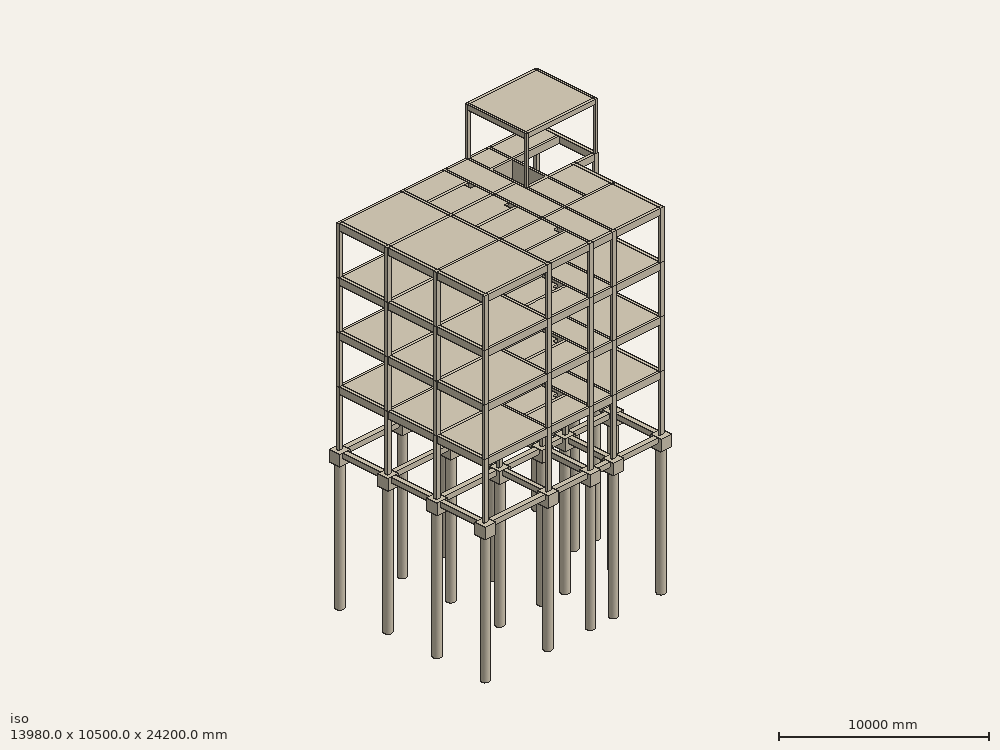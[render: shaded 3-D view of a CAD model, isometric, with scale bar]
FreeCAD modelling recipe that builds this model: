
FCSTD DOCUMENT  (FreeCAD 0.19R24276 (Git))
Label: 2021-02-05 Piloto estructural Metodo 1
License: All rights reserved
objects: Part::FeaturePython×395, Part::Part2DObjectPython×35, App::GeometryPython×28, TechDraw::DrawViewDimension×16, App::DocumentObjectGroup×3, TechDraw::DrawSVGTemplate×3, TechDraw::DrawViewPart×3, TechDraw::DrawPage×3, TechDraw::DrawViewSection×2, Spreadsheet::Sheet×1, App::MaterialObjectPython×1, App::DocumentObjectGroupPython×1, TechDraw::DrawViewAnnotation×1
note: 458 computed .brp shape members not serialized (recipe doc carries the construction recipe); baked Part::Feature solids carry a one-line shape summary decoded from their .brp

FEATURE [Part::FeaturePython] Axis  label="Vertical"  # WARN: FeaturePython — macro-defined, semantics opaque (R4)
  Angles = [0,0,0,0,0,0,0]
  Distances = [1930,4230,2850,1550,1450,1770,1430]
  Length = 11000
  Placement = pos=(0,-500,0) rot=(0,0,1;0rad)
FEATURE [Part::FeaturePython] Axis002  label="Horizontal larga"  # WARN: FeaturePython — macro-defined, semantics opaque (R4)
  Angles = [0,0,0,0,0,0]
  Distances = [100,3250,2620,670,1730,1530]
  Length = 32000
  Placement = pos=(31000,1.077e-12,0) rot=(0,0,1;1.5708rad)
FEATURE [Part::Part2DObjectPython] Rectangle001  label="Lote"  # Draft 2D object (typed FeaturePython)
  Area = 0
  ChamferSize = 0
  Columns = 1
  FilletRadius = 0
  Height = 10000
  Length = 30000
  MakeFace = false
  Rows = 1
FEATURE [Part::Part2DObjectPython] Rectangle002  # Draft 2D object (typed FeaturePython)
  Area = 0
  ChamferSize = 0
  Columns = 1
  FilletRadius = 0
  Height = 700
  Length = 700
  MakeFace = false
  Placement = pos=(14860,9550,0) rot=(0,0,1;0rad)
  Rows = 1
  expr: Height = <<Estructura>>.CabAncho
  expr: Length = <<Estructura>>.CabAncho
FEATURE [Part::Part2DObjectPython] Circle  # Draft 2D object (typed FeaturePython)
  Area = 0
  FirstAngle = 0
  LastAngle = 0
  MakeFace = false
  Placement = pos=(15210,9900,0) rot=(0,0,1;0rad)
  Radius = 250
  expr: Radius = <<Estructura>>.PilRad
FEATURE [Part::FeaturePython] Beam001  # Arch/BIM 7 (typed FeaturePython)
  Chamfer = 0
  DentHeight = 0
  DentLength = 0
  Height = 300
  HorizontalArea = 1059000
  IfcData = attributes={"GlobalId": {"name": "GlobalId", "type": "IfcGloballyUniqueId", "is_enum": false, "enum_values": []}, "Description": {"... (+475 chars omitted),+1 more (map truncated)
  IfcType = 7
  Length = 3530
  MoveBase = false
  MoveWithHost = false
  PerimeterLength = 7660
  Placement = pos=(2280,6490,-800) rot=(0,0,1;0rad)
  PredefinedType = 0
  VerticalArea = 2298000
  Width = 300
FEATURE [Part::FeaturePython] Structure041  label="Beam002"  # Arch/BIM 7 (typed FeaturePython)
  FaceMaker = 0
  Height = 300
  HorizontalArea = 768000
  IfcData = attributes={"GlobalId": {"name": "GlobalId", "type": "IfcGloballyUniqueId", "is_enum": false, "enum_values": []}, "Description": {"... (+475 chars omitted),+1 more (map truncated)
  IfcType = 7
  Length = 2560
  MoveBase = false
  MoveWithHost = false
  Nodes = (2) [(1.2326e-31,-1.51582e-15,5.55112e-16),(2560,-1.51582e-15,5.55112e-16)]
  NodesOffset = 0
  Normal = (0,0,0)
  PerimeterLength = 5720
  Placement = pos=(1930,9550,-650) rot=(0,0,-1;1.5708rad)
  PredefinedType = 0
  VerticalArea = 1.716e+06
  Width = 300
  expr: Height = <<Estructura>>.VRAlto
  expr: Width = <<Estructura>>.VRAncho
FEATURE [Part::FeaturePython] Structure042  label="Beam003"  # Arch/BIM 7 (typed FeaturePython)
  FaceMaker = 0
  Height = 300
  HorizontalArea = 777000
  IfcData = attributes={"GlobalId": {"name": "GlobalId", "type": "IfcGloballyUniqueId", "is_enum": false, "enum_values": []}, "Description": {"... (+475 chars omitted),+1 more (map truncated)
  IfcType = 7
  Length = 2590
  MoveBase = false
  MoveWithHost = false
  Nodes = (2) [(1.2326e-31,-1.51582e-15,5.55112e-16),(2590,-1.51582e-15,5.55112e-16)]
  NodesOffset = 0
  Normal = (0,0,0)
  PerimeterLength = 5780
  Placement = pos=(1930,6290,-650) rot=(0,0,-1;1.5708rad)
  PredefinedType = 0
  VerticalArea = 1.734e+06
  Width = 300
FEATURE [Part::FeaturePython] Structure043  label="Beam004"  # Arch/BIM 7 (typed FeaturePython)
  FaceMaker = 0
  Height = 300
  HorizontalArea = 765000
  IfcData = attributes={"GlobalId": {"name": "GlobalId", "type": "IfcGloballyUniqueId", "is_enum": false, "enum_values": []}, "Description": {"... (+475 chars omitted),+1 more (map truncated)
  IfcType = 7
  Length = 2550
  MoveBase = false
  MoveWithHost = false
  Nodes = (2) [(1.2326e-31,-1.51582e-15,5.55112e-16),(2550,-1.51582e-15,5.55112e-16)]
  NodesOffset = 0
  Normal = (0,0,0)
  PerimeterLength = 5700
  Placement = pos=(1930,3000,-650) rot=(0,0,-1;1.5708rad)
  PredefinedType = 0
  VerticalArea = 1.71e+06
  Width = 300
FEATURE [Part::FeaturePython] Structure044  label="Beam005"  # Arch/BIM 7 (typed FeaturePython)
  FaceMaker = 0
  Height = 300
  HorizontalArea = 768000
  IfcData = attributes={"GlobalId": {"name": "GlobalId", "type": "IfcGloballyUniqueId", "is_enum": false, "enum_values": []}, "Description": {"... (+475 chars omitted),+1 more (map truncated)
  IfcType = 7
  Length = 2560
  MoveBase = false
  MoveWithHost = false
  Nodes = (2) [(1.2326e-31,-1.51582e-15,5.55112e-16),(2560,-1.51582e-15,5.55112e-16)]
  NodesOffset = 0
  Normal = (0,0,0)
  PerimeterLength = 5720
  Placement = pos=(6160.36,9550,-650) rot=(0,0,-1;1.5708rad)
  PredefinedType = 0
  VerticalArea = 1.716e+06
  Width = 300
FEATURE [Part::FeaturePython] Structure045  label="Beam006"  # Arch/BIM 7 (typed FeaturePython)
  FaceMaker = 0
  Height = 300
  HorizontalArea = 777000
  IfcData = attributes={"GlobalId": {"name": "GlobalId", "type": "IfcGloballyUniqueId", "is_enum": false, "enum_values": []}, "Description": {"... (+475 chars omitted),+1 more (map truncated)
  IfcType = 7
  Length = 2590
  MoveBase = false
  MoveWithHost = false
  Nodes = (2) [(1.2326e-31,-1.51582e-15,5.55112e-16),(2590,-1.51582e-15,5.55112e-16)]
  NodesOffset = 0
  Normal = (0,0,0)
  PerimeterLength = 5780
  Placement = pos=(6160.36,6290,-650) rot=(0,0,-1;1.5708rad)
  PredefinedType = 0
  VerticalArea = 1.734e+06
  Width = 300
FEATURE [Part::FeaturePython] Structure046  label="Beam007"  # Arch/BIM 7 (typed FeaturePython)
  FaceMaker = 0
  Height = 300
  HorizontalArea = 765000
  IfcData = attributes={"GlobalId": {"name": "GlobalId", "type": "IfcGloballyUniqueId", "is_enum": false, "enum_values": []}, "Description": {"... (+475 chars omitted),+1 more (map truncated)
  IfcType = 7
  Length = 2550
  MoveBase = false
  MoveWithHost = false
  Nodes = (2) [(1.2326e-31,-1.51582e-15,5.55112e-16),(2550,-1.51582e-15,5.55112e-16)]
  NodesOffset = 0
  Normal = (0,0,0)
  PerimeterLength = 5700
  Placement = pos=(6160.36,3000,-650) rot=(0,0,-1;1.5708rad)
  PredefinedType = 0
  VerticalArea = 1.71e+06
  Width = 300
FEATURE [Part::FeaturePython] Structure048  label="Beam009"  # Arch/BIM 7 (typed FeaturePython)
  FaceMaker = 0
  Height = 300
  HorizontalArea = 777000
  IfcData = attributes={"GlobalId": {"name": "GlobalId", "type": "IfcGloballyUniqueId", "is_enum": false, "enum_values": []}, "Description": {"... (+475 chars omitted),+1 more (map truncated)
  IfcType = 7
  Length = 2590
  MoveBase = false
  MoveWithHost = false
  Nodes = (2) [(1.2326e-31,-1.51582e-15,5.55112e-16),(2590,-1.51582e-15,5.55112e-16)]
  NodesOffset = 0
  Normal = (0,0,0)
  PerimeterLength = 5780
  Placement = pos=(9010.18,6290,-650) rot=(0,0,-1;1.5708rad)
  PredefinedType = 0
  VerticalArea = 1.734e+06
  Width = 300
FEATURE [Part::FeaturePython] Structure049  label="Beam010"  # Arch/BIM 7 (typed FeaturePython)
  FaceMaker = 0
  Height = 300
  HorizontalArea = 765000
  IfcData = attributes={"GlobalId": {"name": "GlobalId", "type": "IfcGloballyUniqueId", "is_enum": false, "enum_values": []}, "Description": {"... (+475 chars omitted),+1 more (map truncated)
  IfcType = 7
  Length = 2550
  MoveBase = false
  MoveWithHost = false
  Nodes = (2) [(1.2326e-31,-1.51582e-15,5.55112e-16),(2550,-1.51582e-15,5.55112e-16)]
  NodesOffset = 0
  Normal = (0,0,0)
  PerimeterLength = 5700
  Placement = pos=(9010.18,3000,-650) rot=(0,0,-1;1.5708rad)
  PredefinedType = 0
  VerticalArea = 1.71e+06
  Width = 300
FEATURE [Part::FeaturePython] Structure053  label="Beam014"  # Arch/BIM 7 (typed FeaturePython)
  FaceMaker = 0
  Height = 300
  HorizontalArea = 765000
  IfcData = attributes={"GlobalId": {"name": "GlobalId", "type": "IfcGloballyUniqueId", "is_enum": false, "enum_values": []}, "Description": {"... (+475 chars omitted),+1 more (map truncated)
  IfcType = 7
  Length = 2550
  MoveBase = false
  MoveWithHost = false
  Nodes = (2) [(1.2326e-31,-1.51582e-15,5.55112e-16),(2550,-1.51582e-15,5.55112e-16)]
  NodesOffset = 0
  Normal = (0,0,0)
  PerimeterLength = 5700
  Placement = pos=(13778.3,3000,-650) rot=(0,0,-1;1.5708rad)
  PredefinedType = 0
  VerticalArea = 1.71e+06
  Width = 300
FEATURE [Part::FeaturePython] Structure056  label="Beam017"  # Arch/BIM 7 (typed FeaturePython)
  FaceMaker = 0
  Height = 300
  HorizontalArea = 765000
  IfcData = attributes={"GlobalId": {"name": "GlobalId", "type": "IfcGloballyUniqueId", "is_enum": false, "enum_values": []}, "Description": {"... (+475 chars omitted),+1 more (map truncated)
  IfcType = 7
  Length = 2550
  MoveBase = false
  MoveWithHost = false
  Nodes = (2) [(1.2326e-31,-1.51582e-15,5.55112e-16),(2550,-1.51582e-15,5.55112e-16)]
  NodesOffset = 0
  Normal = (0,0,0)
  PerimeterLength = 5700
  Placement = pos=(10560,3000,-650) rot=(0,0,-1;1.5708rad)
  PredefinedType = 0
  VerticalArea = 1.71e+06
  Width = 300
FEATURE [Part::FeaturePython] Structure059  label="Beam020"  # Arch/BIM 7 (typed FeaturePython)
  FaceMaker = 0
  Height = 300
  HorizontalArea = 645000
  IfcData = attributes={"GlobalId": {"name": "GlobalId", "type": "IfcGloballyUniqueId", "is_enum": false, "enum_values": []}, "Description": {"... (+475 chars omitted),+1 more (map truncated)
  IfcType = 7
  Length = 2150
  MoveBase = false
  MoveWithHost = false
  Nodes = (2) [(1.2326e-31,-1.51582e-15,5.55112e-16),(2150,-1.51582e-15,5.55112e-16)]
  NodesOffset = 0
  Normal = (0,0,0)
  PerimeterLength = 4900
  Placement = pos=(6510,9900,-650) rot=(0,0,1;0rad)
  PredefinedType = 0
  VerticalArea = 1.47e+06
  Width = 300
FEATURE [Part::FeaturePython] Structure060  label="Beam021"  # Arch/BIM 7 (typed FeaturePython)
  FaceMaker = 0
  Height = 300
  HorizontalArea = 690000
  IfcData = attributes={"GlobalId": {"name": "GlobalId", "type": "IfcGloballyUniqueId", "is_enum": false, "enum_values": []}, "Description": {"... (+475 chars omitted),+1 more (map truncated)
  IfcType = 7
  Length = 2300
  MoveBase = false
  MoveWithHost = false
  Nodes = (2) [(1.2326e-31,-1.51582e-15,5.55112e-16),(2300,-1.51582e-15,5.55112e-16)]
  NodesOffset = 0
  Normal = (0,0,0)
  PerimeterLength = 5200
  Placement = pos=(9360,9900,-650) rot=(0,0,1;0rad)
  PredefinedType = 0
  VerticalArea = 1.56e+06
  Width = 300
FEATURE [Part::FeaturePython] Structure061  label="Beam022"  # Arch/BIM 7 (typed FeaturePython)
  FaceMaker = 0
  Height = 300
  HorizontalArea = 750000
  IfcData = attributes={"GlobalId": {"name": "GlobalId", "type": "IfcGloballyUniqueId", "is_enum": false, "enum_values": []}, "Description": {"... (+475 chars omitted),+1 more (map truncated)
  IfcType = 7
  Length = 2500
  MoveBase = false
  MoveWithHost = false
  Nodes = (2) [(1.2326e-31,-1.51582e-15,5.55112e-16),(2500,-1.51582e-15,5.55112e-16)]
  NodesOffset = 0
  Normal = (0,0,0)
  PerimeterLength = 5600
  Placement = pos=(12360,9900,-650) rot=(0,0,1;0rad)
  PredefinedType = 0
  VerticalArea = 1680000
  Width = 300
FEATURE [Part::FeaturePython] Structure064  label="Beam025"  # Arch/BIM 7 (typed FeaturePython)
  FaceMaker = 0
  Height = 300
  HorizontalArea = 645000
  IfcData = attributes={"GlobalId": {"name": "GlobalId", "type": "IfcGloballyUniqueId", "is_enum": false, "enum_values": []}, "Description": {"... (+475 chars omitted),+1 more (map truncated)
  IfcType = 7
  Length = 2150
  MoveBase = false
  MoveWithHost = false
  Nodes = (2) [(1.2326e-31,-1.51582e-15,5.55112e-16),(2150,-1.51582e-15,5.55112e-16)]
  NodesOffset = 0
  Normal = (0,0,0)
  PerimeterLength = 4900
  Placement = pos=(6510,6640,-650) rot=(0,0,1;0rad)
  PredefinedType = 0
  VerticalArea = 1.47e+06
  Width = 300
FEATURE [Part::FeaturePython] Structure065  label="Beam026"  # Arch/BIM 7 (typed FeaturePython)
  FaceMaker = 0
  Height = 300
  HorizontalArea = 768000
  IfcData = attributes={"GlobalId": {"name": "GlobalId", "type": "IfcGloballyUniqueId", "is_enum": false, "enum_values": []}, "Description": {"... (+475 chars omitted),+1 more (map truncated)
  IfcType = 7
  Length = 2560
  MoveBase = false
  MoveWithHost = false
  Nodes = (2) [(1.2326e-31,-1.51582e-15,5.55112e-16),(2560,-1.51582e-15,5.55112e-16)]
  NodesOffset = 0
  Normal = (0,0,0)
  PerimeterLength = 5720
  Placement = pos=(9010,6990,-650) rot=(0,0,1;1.5708rad)
  PredefinedType = 0
  VerticalArea = 1.716e+06
  Width = 300
FEATURE [Part::FeaturePython] Structure066  label="Beam027"  # Arch/BIM 7 (typed FeaturePython)
  FaceMaker = 0
  Height = 300
  HorizontalArea = 1.059e+06
  IfcData = attributes={"GlobalId": {"name": "GlobalId", "type": "IfcGloballyUniqueId", "is_enum": false, "enum_values": []}, "Description": {"... (+475 chars omitted),+1 more (map truncated)
  IfcType = 7
  Length = 3530
  MoveBase = false
  MoveWithHost = false
  Nodes = (2) [(1.2326e-31,-1.51582e-15,5.55112e-16),(3530,-1.51582e-15,5.55112e-16)]
  NodesOffset = 0
  Normal = (0,0,0)
  PerimeterLength = 7660
  Placement = pos=(2280,3350,-650) rot=(0,0,1;0rad)
  PredefinedType = 0
  VerticalArea = 2.298e+06
  Width = 300
FEATURE [Part::FeaturePython] Structure067  label="Beam028"  # Arch/BIM 7 (typed FeaturePython)
  FaceMaker = 0
  Height = 300
  HorizontalArea = 645000
  IfcData = attributes={"GlobalId": {"name": "GlobalId", "type": "IfcGloballyUniqueId", "is_enum": false, "enum_values": []}, "Description": {"... (+475 chars omitted),+1 more (map truncated)
  IfcType = 7
  Length = 2150
  MoveBase = false
  MoveWithHost = false
  Nodes = (2) [(1.2326e-31,-1.51582e-15,5.55112e-16),(2150,-1.51582e-15,5.55112e-16)]
  NodesOffset = 0
  Normal = (0,0,0)
  PerimeterLength = 4900
  Placement = pos=(6510,3350,-650) rot=(0,0,1;0rad)
  PredefinedType = 0
  VerticalArea = 1.47e+06
  Width = 300
FEATURE [Part::FeaturePython] Structure068  label="Beam029"  # Arch/BIM 7 (typed FeaturePython)
  FaceMaker = 0
  Height = 300
  HorizontalArea = 1.059e+06
  IfcData = attributes={"GlobalId": {"name": "GlobalId", "type": "IfcGloballyUniqueId", "is_enum": false, "enum_values": []}, "Description": {"... (+475 chars omitted),+1 more (map truncated)
  IfcType = 7
  Length = 3530
  MoveBase = false
  MoveWithHost = false
  Nodes = (2) [(1.2326e-31,-1.51582e-15,5.55112e-16),(3530,-1.51582e-15,5.55112e-16)]
  NodesOffset = 0
  Normal = (0,0,0)
  PerimeterLength = 7660
  Placement = pos=(2280,100,-650) rot=(0,0,1;0rad)
  PredefinedType = 0
  VerticalArea = 2.298e+06
  Width = 300
FEATURE [Part::FeaturePython] Structure069  label="Beam030"  # Arch/BIM 7 (typed FeaturePython)
  FaceMaker = 0
  Height = 300
  HorizontalArea = 645000
  IfcData = attributes={"GlobalId": {"name": "GlobalId", "type": "IfcGloballyUniqueId", "is_enum": false, "enum_values": []}, "Description": {"... (+475 chars omitted),+1 more (map truncated)
  IfcType = 7
  Length = 2150
  MoveBase = false
  MoveWithHost = false
  Nodes = (2) [(1.2326e-31,-1.51582e-15,5.55112e-16),(2150,-1.51582e-15,5.55112e-16)]
  NodesOffset = 0
  Normal = (0,0,0)
  PerimeterLength = 4900
  Placement = pos=(6510,100,-650) rot=(0,0,1;0rad)
  PredefinedType = 0
  VerticalArea = 1.47e+06
  Width = 300
FEATURE [Part::FeaturePython] Structure070  label="Beam031"  # Arch/BIM 7 (typed FeaturePython)
  FaceMaker = 0
  Height = 300
  HorizontalArea = 255000
  IfcData = attributes={"GlobalId": {"name": "GlobalId", "type": "IfcGloballyUniqueId", "is_enum": false, "enum_values": []}, "Description": {"... (+475 chars omitted),+1 more (map truncated)
  IfcType = 7
  Length = 850
  MoveBase = false
  MoveWithHost = false
  Nodes = (2) [(1.2326e-31,-1.51582e-15,5.55112e-16),(850,-1.51582e-15,5.55112e-16)]
  NodesOffset = 0
  Normal = (0,0,0)
  PerimeterLength = 2300
  Placement = pos=(9360,100,-650) rot=(0,0,1;0rad)
  PredefinedType = 0
  VerticalArea = 690000
  Width = 300
FEATURE [Part::FeaturePython] Structure071  label="Beam032"  # Arch/BIM 7 (typed FeaturePython)
  FaceMaker = 0
  Height = 300
  HorizontalArea = 756000
  IfcData = attributes={"GlobalId": {"name": "GlobalId", "type": "IfcGloballyUniqueId", "is_enum": false, "enum_values": []}, "Description": {"... (+475 chars omitted),+1 more (map truncated)
  IfcType = 7
  Length = 2520
  MoveBase = false
  MoveWithHost = false
  Nodes = (2) [(1.2326e-31,-1.51582e-15,5.55112e-16),(2520,-1.51582e-15,5.55112e-16)]
  NodesOffset = 0
  Normal = (0,0,0)
  PerimeterLength = 5640
  Placement = pos=(10910,100,-650) rot=(0,0,1;0rad)
  PredefinedType = 0
  VerticalArea = 1.692e+06
  Width = 300
FEATURE [Part::FeaturePython] Structure072  label="Beam033"  # Arch/BIM 7 (typed FeaturePython)
  FaceMaker = 0
  Height = 300
  HorizontalArea = 255000
  IfcData = attributes={"GlobalId": {"name": "GlobalId", "type": "IfcGloballyUniqueId", "is_enum": false, "enum_values": []}, "Description": {"... (+475 chars omitted),+1 more (map truncated)
  IfcType = 7
  Length = 850
  MoveBase = false
  MoveWithHost = false
  Nodes = (2) [(1.2326e-31,-1.51582e-15,5.55112e-16),(850,-1.51582e-15,5.55112e-16)]
  NodesOffset = 0
  Normal = (0,0,0)
  PerimeterLength = 2300
  Placement = pos=(9360,3350,-650) rot=(0,0,1;0rad)
  PredefinedType = 0
  VerticalArea = 690000
  Width = 300
FEATURE [Part::FeaturePython] Structure073  label="Beam034"  # Arch/BIM 7 (typed FeaturePython)
  FaceMaker = 0
  Height = 300
  HorizontalArea = 756000
  IfcData = attributes={"GlobalId": {"name": "GlobalId", "type": "IfcGloballyUniqueId", "is_enum": false, "enum_values": []}, "Description": {"... (+475 chars omitted),+1 more (map truncated)
  IfcType = 7
  Length = 2520
  MoveBase = false
  MoveWithHost = false
  Nodes = (2) [(1.2326e-31,-1.51582e-15,5.55112e-16),(2520,-1.51582e-15,5.55112e-16)]
  NodesOffset = 0
  Normal = (0,0,0)
  PerimeterLength = 5640
  Placement = pos=(10910,3350,-650) rot=(0,0,1;0rad)
  PredefinedType = 0
  VerticalArea = 1.692e+06
  Width = 300
FEATURE [Part::FeaturePython] Structure074  label="Beam035"  # Arch/BIM 7 (typed FeaturePython)
  FaceMaker = 0
  Height = 300
  HorizontalArea = 969000
  IfcData = attributes={"GlobalId": {"name": "GlobalId", "type": "IfcGloballyUniqueId", "is_enum": false, "enum_values": []}, "Description": {"... (+475 chars omitted),+1 more (map truncated)
  IfcType = 7
  Length = 3230
  MoveBase = false
  MoveWithHost = false
  Nodes = (2) [(1.2326e-31,-1.51582e-15,5.55112e-16),(3230,-1.51582e-15,5.55112e-16)]
  NodesOffset = 0
  Normal = (0,0,0)
  PerimeterLength = 7060
  Placement = pos=(15210,9550,-650) rot=(0,0,-1;1.5708rad)
  PredefinedType = 0
  VerticalArea = 2.118e+06
  Width = 300
FEATURE [Part::FeaturePython] Structure075  label="Beam036"  # Arch/BIM 7 (typed FeaturePython)
  FaceMaker = 0
  Height = 300
  HorizontalArea = 576000
  IfcData = attributes={"GlobalId": {"name": "GlobalId", "type": "IfcGloballyUniqueId", "is_enum": false, "enum_values": []}, "Description": {"... (+475 chars omitted),+1 more (map truncated)
  IfcType = 7
  Length = 1920
  MoveBase = false
  MoveWithHost = false
  Nodes = (2) [(1.2326e-31,-1.51582e-15,5.55112e-16),(1920,-1.51582e-15,5.55112e-16)]
  NodesOffset = 0
  Normal = (0,0,0)
  PerimeterLength = 4440
  Placement = pos=(13780,3700,-650) rot=(0,0,1;1.5708rad)
  PredefinedType = 0
  VerticalArea = 1.332e+06
  Width = 300
FEATURE [Part::FeaturePython] Structure076  label="Beam037"  # Arch/BIM 7 (typed FeaturePython)
  FaceMaker = 0
  Height = 300
  HorizontalArea = 219000
  IfcData = attributes={"GlobalId": {"name": "GlobalId", "type": "IfcGloballyUniqueId", "is_enum": false, "enum_values": []}, "Description": {"... (+475 chars omitted),+1 more (map truncated)
  IfcType = 7
  Length = 730
  MoveBase = false
  MoveWithHost = false
  Nodes = (2) [(1.2326e-31,-1.51582e-15,5.55112e-16),(730,-1.51582e-15,5.55112e-16)]
  NodesOffset = 0
  Normal = (0,0,0)
  PerimeterLength = 2060
  Placement = pos=(14130,5970,-650) rot=(0,0,1;0rad)
  PredefinedType = 0
  VerticalArea = 618000
  Width = 300
FEATURE [Part::FeaturePython] Structure077  label="Beam038"  # Arch/BIM 7 (typed FeaturePython)
  FaceMaker = 0
  Height = 300
  HorizontalArea = 681000
  IfcData = attributes={"GlobalId": {"name": "GlobalId", "type": "IfcGloballyUniqueId", "is_enum": false, "enum_values": []}, "Description": {"... (+475 chars omitted),+1 more (map truncated)
  IfcType = 7
  Length = 2270
  MoveBase = false
  MoveWithHost = false
  Nodes = (2) [(1.2326e-31,-1.51582e-15,5.55112e-16),(2270,-1.51582e-15,5.55112e-16)]
  NodesOffset = 0
  Normal = (0,0,0)
  PerimeterLength = 5140
  Placement = pos=(10560,3700,-650) rot=(0,0,1;1.5708rad)
  PredefinedType = 0
  VerticalArea = 1.542e+06
  Width = 300
FEATURE [Part::FeaturePython] Structure078  label="Beam039"  # Arch/BIM 7 (typed FeaturePython)
  FaceMaker = 0
  Height = 300
  HorizontalArea = 414000
  IfcData = attributes={"GlobalId": {"name": "GlobalId", "type": "IfcGloballyUniqueId", "is_enum": false, "enum_values": []}, "Description": {"... (+475 chars omitted),+1 more (map truncated)
  IfcType = 7
  Length = 1380
  MoveBase = false
  MoveWithHost = false
  Nodes = (2) [(1.2326e-31,-1.51582e-15,5.55112e-16),(1380,-1.51582e-15,5.55112e-16)]
  NodesOffset = 0
  Normal = (0,0,0)
  PerimeterLength = 3360
  Placement = pos=(10560,9750,-650) rot=(0,0,-1;1.5708rad)
  PredefinedType = 0
  VerticalArea = 1.008e+06
  Width = 300
FEATURE [Part::FeaturePython] Structure079  label="Beam040"  # Arch/BIM 7 (typed FeaturePython)
  FaceMaker = 0
  Height = 300
  HorizontalArea = 354000
  IfcData = attributes={"GlobalId": {"name": "GlobalId", "type": "IfcGloballyUniqueId", "is_enum": false, "enum_values": []}, "Description": {"... (+475 chars omitted),+1 more (map truncated)
  IfcType = 7
  Length = 1180
  MoveBase = false
  MoveWithHost = false
  Nodes = (2) [(1.2326e-31,-1.51582e-15,5.55112e-16),(1180,-1.51582e-15,5.55112e-16)]
  NodesOffset = 0
  Normal = (0,0,0)
  PerimeterLength = 2960
  Placement = pos=(12010,9550,-650) rot=(0,0,-1;1.5708rad)
  PredefinedType = 0
  VerticalArea = 888000
  Width = 300
FEATURE [Part::FeaturePython] Structure080  label="Beam041"  # Arch/BIM 7 (typed FeaturePython)
  FaceMaker = 0
  Height = 300
  HorizontalArea = 426000
  IfcData = attributes={"GlobalId": {"name": "GlobalId", "type": "IfcGloballyUniqueId", "is_enum": false, "enum_values": []}, "Description": {"... (+475 chars omitted),+1 more (map truncated)
  IfcType = 7
  Length = 1420
  MoveBase = false
  MoveWithHost = false
  Nodes = (2) [(1.2326e-31,-1.51582e-15,5.55112e-16),(1420,-1.51582e-15,5.55112e-16)]
  NodesOffset = 0
  Normal = (0,0,0)
  PerimeterLength = 3440
  Placement = pos=(13430,5970,-650) rot=(0,0,1;3.14159rad)
  PredefinedType = 0
  VerticalArea = 1.032e+06
  Width = 300
FEATURE [Part::Part2DObjectPython] Rectangle  # Draft 2D object (typed FeaturePython)
  Area = 0
  ChamferSize = 0
  Columns = 1
  FilletRadius = 0
  Height = 2550
  Length = 1600
  MakeFace = false
  Placement = pos=(10485,5895,0) rot=(0,0,1;0rad)
  Rows = 1
FEATURE [Spreadsheet::Sheet] Spreadsheet  label="Estructura"
  cells = A1=MODELO ESTRUCTURAL; A2=Descripcion; B2=Alias; C2=Valor; D2=Unidad; A3=Cabezal Ancho; B3=CabAncho; C3(CabAncho)=700; D3=mm; A4=Cabezal Espesor; B4=CabEsp; C4(CabEsp)=700; D4=mm; A5=Pilote Radio; B5=PilRad; C5(PilRad)=250; D5=mm; A6=Pilote Profundidad; B6=PilProf; C6(PilProf)=8000; D6=mm; A7=Viga Riostra Ancho; B7=VRAncho; C7(VRAncho)=300; D7=mm; A8=Viga Riostra Alto; B8=VRAlto; C8(VRAlto)=300; D8=mm
FEATURE [Part::FeaturePython] Beam  # Arch/BIM 7 (typed FeaturePython)
  Chamfer = 0
  DentHeight = 0
  DentLength = 0
  Height = 300
  HorizontalArea = 1059000
  IfcData = attributes={"GlobalId": {"name": "GlobalId", "type": "IfcGloballyUniqueId", "is_enum": false, "enum_values": []}, "Description": {"... (+475 chars omitted),+1 more (map truncated)
  IfcType = 7
  Length = 3530
  MoveBase = false
  MoveWithHost = false
  PerimeterLength = 7660
  Placement = pos=(2280,9750,-800) rot=(0,0,1;0rad)
  PredefinedType = 0
  VerticalArea = 2298000
  Width = 300
FEATURE [Part::Part2DObjectPython] Rectangle003  # Draft 2D object (typed FeaturePython)
  Area = 0
  ChamferSize = 0
  Columns = 1
  FilletRadius = 0
  Height = 2550
  Length = 1600
  MakeFace = false
  Placement = pos=(10485,5895,0) rot=(0,0,1;0rad)
  Rows = 1
FEATURE [Part::FeaturePython] Structure142  label="V15x40 V133"  # Arch/BIM 7 (typed FeaturePython)
  FaceMaker = 0
  Height = 400
  HorizontalArea = 597000
  IfcData = attributes={"GlobalId": {"name": "GlobalId", "type": "IfcGloballyUniqueId", "is_enum": false, "enum_values": []}, "Description": {"... (+475 chars omitted),+1 more (map truncated)
  IfcType = 7
  Length = 3980
  MoveBase = false
  MoveWithHost = false
  Nodes = (2) [(-1.72563e-31,-1.42109e-15,-7.77156e-16),(3980,-1.42109e-15,-7.77156e-16)]
  NodesOffset = 0
  Normal = (0,0,0)
  PerimeterLength = 8260
  Placement = pos=(2055,9900,5800) rot=(0,0,1;0rad)
  PredefinedType = 0
  VerticalArea = 3.304e+06
  Width = 150
FEATURE [Part::FeaturePython] Structure143  label="V15x40 V134"  # Arch/BIM 7 (typed FeaturePython)
  FaceMaker = 0
  Height = 400
  HorizontalArea = 390000
  IfcData = attributes={"GlobalId": {"name": "GlobalId", "type": "IfcGloballyUniqueId", "is_enum": false, "enum_values": []}, "Description": {"... (+475 chars omitted),+1 more (map truncated)
  IfcType = 7
  Length = 2600
  MoveBase = false
  MoveWithHost = false
  Nodes = (2) [(-1.72563e-31,-1.42109e-15,-7.77156e-16),(2600,-1.42109e-15,-7.77156e-16)]
  NodesOffset = 0
  Normal = (0,0,0)
  PerimeterLength = 5500
  Placement = pos=(6285,9900,5800) rot=(0,0,1;0rad)
  PredefinedType = 0
  VerticalArea = 2200000
  Width = 150
FEATURE [Part::FeaturePython] Structure144  label="V15x40 V135"  # Arch/BIM 7 (typed FeaturePython)
  FaceMaker = 0
  Height = 400
  HorizontalArea = 412500
  IfcData = attributes={"GlobalId": {"name": "GlobalId", "type": "IfcGloballyUniqueId", "is_enum": false, "enum_values": []}, "Description": {"... (+475 chars omitted),+1 more (map truncated)
  IfcType = 7
  Length = 2750
  MoveBase = false
  MoveWithHost = false
  Nodes = (2) [(-1.72563e-31,-1.42109e-15,-7.77156e-16),(2750,-1.42109e-15,-7.77156e-16)]
  NodesOffset = 0
  Normal = (0,0,0)
  PerimeterLength = 5800
  Placement = pos=(9135,9900,5800) rot=(0,0,1;0rad)
  PredefinedType = 0
  VerticalArea = 2320000
  Width = 150
FEATURE [Part::FeaturePython] Structure145  label="V15x40 V136"  # Arch/BIM 7 (typed FeaturePython)
  FaceMaker = 0
  Height = 400
  HorizontalArea = 442500
  IfcData = attributes={"GlobalId": {"name": "GlobalId", "type": "IfcGloballyUniqueId", "is_enum": false, "enum_values": []}, "Description": {"... (+475 chars omitted),+1 more (map truncated)
  IfcType = 7
  Length = 2950
  MoveBase = false
  MoveWithHost = false
  Nodes = (2) [(-1.72563e-31,-1.42109e-15,-7.77156e-16),(2950,-1.42109e-15,-7.77156e-16)]
  NodesOffset = 0
  Normal = (0,0,0)
  PerimeterLength = 6200
  Placement = pos=(12135,9900,5800) rot=(0,0,1;0rad)
  PredefinedType = 0
  VerticalArea = 2.48e+06
  Width = 150
FEATURE [Part::FeaturePython] Structure146  label="V15x40 V137"  # Arch/BIM 7 (typed FeaturePython)
  FaceMaker = 0
  Height = 400
  HorizontalArea = 453750
  IfcData = attributes={"GlobalId": {"name": "GlobalId", "type": "IfcGloballyUniqueId", "is_enum": false, "enum_values": []}, "Description": {"... (+475 chars omitted),+1 more (map truncated)
  IfcType = 7
  Length = 3025
  MoveBase = false
  MoveWithHost = false
  Nodes = (2) [(-1.72563e-31,-1.42109e-15,-7.77156e-16),(3025,-1.42109e-15,-7.77156e-16)]
  NodesOffset = 0
  Normal = (0,0,0)
  PerimeterLength = 6350
  Placement = pos=(12085,8370,5800) rot=(0,0,1;0rad)
  PredefinedType = 0
  VerticalArea = 2.54e+06
  Width = 150
FEATURE [Part::FeaturePython] Structure147  label="V15x40 V138"  # Arch/BIM 7 (typed FeaturePython)
  FaceMaker = 0
  Height = 400
  HorizontalArea = 597000
  IfcData = attributes={"GlobalId": {"name": "GlobalId", "type": "IfcGloballyUniqueId", "is_enum": false, "enum_values": []}, "Description": {"... (+475 chars omitted),+1 more (map truncated)
  IfcType = 7
  Length = 3980
  MoveBase = false
  MoveWithHost = false
  Nodes = (2) [(-1.72563e-31,-1.42109e-15,-7.77156e-16),(3980,-1.42109e-15,-7.77156e-16)]
  NodesOffset = 0
  Normal = (0,0,0)
  PerimeterLength = 8260
  Placement = pos=(2055,6640,5800) rot=(0,0,1;0rad)
  PredefinedType = 0
  VerticalArea = 3.304e+06
  Width = 150
FEATURE [Part::FeaturePython] Structure148  label="V15x40 V139"  # Arch/BIM 7 (typed FeaturePython)
  FaceMaker = 0
  Height = 400
  HorizontalArea = 397500
  IfcData = attributes={"GlobalId": {"name": "GlobalId", "type": "IfcGloballyUniqueId", "is_enum": false, "enum_values": []}, "Description": {"... (+475 chars omitted),+1 more (map truncated)
  IfcType = 7
  Length = 2650
  MoveBase = false
  MoveWithHost = false
  Nodes = (2) [(-1.72563e-31,-1.42109e-15,-7.77156e-16),(2650,-1.42109e-15,-7.77156e-16)]
  NodesOffset = 0
  Normal = (0,0,0)
  PerimeterLength = 5600
  Placement = pos=(6285,6640,5800) rot=(0,0,1;0rad)
  PredefinedType = 0
  VerticalArea = 2240000
  Width = 150
FEATURE [Part::FeaturePython] Structure149  label="V15x40 V140"  # Arch/BIM 7 (typed FeaturePython)
  FaceMaker = 0
  Height = 400
  HorizontalArea = 210000
  IfcData = attributes={"GlobalId": {"name": "GlobalId", "type": "IfcGloballyUniqueId", "is_enum": false, "enum_values": []}, "Description": {"... (+475 chars omitted),+1 more (map truncated)
  IfcType = 7
  Length = 1400
  MoveBase = false
  MoveWithHost = false
  Nodes = (2) [(-1.72563e-31,-1.42109e-15,-7.77156e-16),(1400,-1.42109e-15,-7.77156e-16)]
  NodesOffset = 0
  Normal = (0,0,0)
  PerimeterLength = 3100
  Placement = pos=(9085,6640,5800) rot=(0,0,1;0rad)
  PredefinedType = 0
  VerticalArea = 1240000
  Width = 150
FEATURE [Part::FeaturePython] Structure150  label="V15x40 V141"  # Arch/BIM 7 (typed FeaturePython)
  FaceMaker = 0
  Height = 400
  HorizontalArea = 235500
  IfcData = attributes={"GlobalId": {"name": "GlobalId", "type": "IfcGloballyUniqueId", "is_enum": false, "enum_values": []}, "Description": {"... (+475 chars omitted),+1 more (map truncated)
  IfcType = 7
  Length = 1570
  MoveBase = false
  MoveWithHost = false
  Nodes = (2) [(-1.72563e-31,-1.42109e-15,-7.77156e-16),(1570,-1.42109e-15,-7.77156e-16)]
  NodesOffset = 0
  Normal = (0,0,0)
  PerimeterLength = 3440
  Placement = pos=(13655,5970,5800) rot=(0,0,1;3.14159rad)
  PredefinedType = 0
  VerticalArea = 1.376e+06
  Width = 150
FEATURE [Part::FeaturePython] Structure151  label="V15x40 V142"  # Arch/BIM 7 (typed FeaturePython)
  FaceMaker = 0
  Height = 400
  HorizontalArea = 177000
  IfcData = attributes={"GlobalId": {"name": "GlobalId", "type": "IfcGloballyUniqueId", "is_enum": false, "enum_values": []}, "Description": {"... (+475 chars omitted),+1 more (map truncated)
  IfcType = 7
  Length = 1180
  MoveBase = false
  MoveWithHost = false
  Nodes = (2) [(-1.72563e-31,-1.42109e-15,-7.77156e-16),(1180,-1.42109e-15,-7.77156e-16)]
  NodesOffset = 0
  Normal = (0,0,0)
  PerimeterLength = 2660
  Placement = pos=(13905,5970,5800) rot=(0,0,1;0rad)
  PredefinedType = 0
  VerticalArea = 1064000
  Width = 150
FEATURE [Part::FeaturePython] Structure152  label="V15x40 V143"  # Arch/BIM 7 (typed FeaturePython)
  FaceMaker = 0
  Height = 400
  HorizontalArea = 597000
  IfcData = attributes={"GlobalId": {"name": "GlobalId", "type": "IfcGloballyUniqueId", "is_enum": false, "enum_values": []}, "Description": {"... (+475 chars omitted),+1 more (map truncated)
  IfcType = 7
  Length = 3980
  MoveBase = false
  MoveWithHost = false
  Nodes = (2) [(-1.72563e-31,-1.42109e-15,-7.77156e-16),(3980,-1.42109e-15,-7.77156e-16)]
  NodesOffset = 0
  Normal = (0,0,0)
  PerimeterLength = 8260
  Placement = pos=(2055,3350,5800) rot=(0,0,1;0rad)
  PredefinedType = 0
  VerticalArea = 3.304e+06
  Width = 150
FEATURE [Part::FeaturePython] Structure153  label="V15x40 V144"  # Arch/BIM 7 (typed FeaturePython)
  FaceMaker = 0
  Height = 400
  HorizontalArea = 397500
  IfcData = attributes={"GlobalId": {"name": "GlobalId", "type": "IfcGloballyUniqueId", "is_enum": false, "enum_values": []}, "Description": {"... (+475 chars omitted),+1 more (map truncated)
  IfcType = 7
  Length = 2650
  MoveBase = false
  MoveWithHost = false
  Nodes = (2) [(-1.72563e-31,-1.42109e-15,-7.77156e-16),(2650,-1.42109e-15,-7.77156e-16)]
  NodesOffset = 0
  Normal = (0,0,0)
  PerimeterLength = 5600
  Placement = pos=(6285,3350,5800) rot=(0,0,1;0rad)
  PredefinedType = 0
  VerticalArea = 2240000
  Width = 150
FEATURE [Part::FeaturePython] Structure154  label="V15x40 V145"  # Arch/BIM 7 (typed FeaturePython)
  FaceMaker = 0
  Height = 400
  HorizontalArea = 210000
  IfcData = attributes={"GlobalId": {"name": "GlobalId", "type": "IfcGloballyUniqueId", "is_enum": false, "enum_values": []}, "Description": {"... (+475 chars omitted),+1 more (map truncated)
  IfcType = 7
  Length = 1400
  MoveBase = false
  MoveWithHost = false
  Nodes = (2) [(-1.72563e-31,-1.42109e-15,-7.77156e-16),(1400,-1.42109e-15,-7.77156e-16)]
  NodesOffset = 0
  Normal = (0,0,0)
  PerimeterLength = 3100
  Placement = pos=(9085,3350,5800) rot=(0,0,1;0rad)
  PredefinedType = 0
  VerticalArea = 1240000
  Width = 150
FEATURE [Part::FeaturePython] Structure155  label="V15x40 V146"  # Arch/BIM 7 (typed FeaturePython)
  FaceMaker = 0
  Height = 400
  HorizontalArea = 460500
  IfcData = attributes={"GlobalId": {"name": "GlobalId", "type": "IfcGloballyUniqueId", "is_enum": false, "enum_values": []}, "Description": {"... (+475 chars omitted),+1 more (map truncated)
  IfcType = 7
  Length = 3070
  MoveBase = false
  MoveWithHost = false
  Nodes = (2) [(-1.72563e-31,-1.42109e-15,-7.77156e-16),(3070,-1.42109e-15,-7.77156e-16)]
  NodesOffset = 0
  Normal = (0,0,0)
  PerimeterLength = 6440
  Placement = pos=(10635,3350,5800) rot=(0,0,1;0rad)
  PredefinedType = 0
  VerticalArea = 2.576e+06
  Width = 150
FEATURE [Part::FeaturePython] Structure156  label="V15x40 V147"  # Arch/BIM 7 (typed FeaturePython)
  FaceMaker = 0
  Height = 400
  HorizontalArea = 597000
  IfcData = attributes={"GlobalId": {"name": "GlobalId", "type": "IfcGloballyUniqueId", "is_enum": false, "enum_values": []}, "Description": {"... (+475 chars omitted),+1 more (map truncated)
  IfcType = 7
  Length = 3980
  MoveBase = false
  MoveWithHost = false
  Nodes = (2) [(-1.72563e-31,-1.42109e-15,-7.77156e-16),(3980,-1.42109e-15,-7.77156e-16)]
  NodesOffset = 0
  Normal = (0,0,0)
  PerimeterLength = 8260
  Placement = pos=(2055,100,5800) rot=(0,0,1;0rad)
  PredefinedType = 0
  VerticalArea = 3.304e+06
  Width = 150
FEATURE [Part::FeaturePython] Structure157  label="V15x40 V148"  # Arch/BIM 7 (typed FeaturePython)
  FaceMaker = 0
  Height = 400
  HorizontalArea = 390000
  IfcData = attributes={"GlobalId": {"name": "GlobalId", "type": "IfcGloballyUniqueId", "is_enum": false, "enum_values": []}, "Description": {"... (+475 chars omitted),+1 more (map truncated)
  IfcType = 7
  Length = 2600
  MoveBase = false
  MoveWithHost = false
  Nodes = (2) [(-1.72563e-31,-1.42109e-15,-7.77156e-16),(2600,-1.42109e-15,-7.77156e-16)]
  NodesOffset = 0
  Normal = (0,0,0)
  PerimeterLength = 5500
  Placement = pos=(6285,100,5800) rot=(0,0,1;0rad)
  PredefinedType = 0
  VerticalArea = 2200000
  Width = 150
FEATURE [Part::FeaturePython] Structure158  label="V15x40 V149"  # Arch/BIM 7 (typed FeaturePython)
  FaceMaker = 0
  Height = 400
  HorizontalArea = 195000
  IfcData = attributes={"GlobalId": {"name": "GlobalId", "type": "IfcGloballyUniqueId", "is_enum": false, "enum_values": []}, "Description": {"... (+475 chars omitted),+1 more (map truncated)
  IfcType = 7
  Length = 1300
  MoveBase = false
  MoveWithHost = false
  Nodes = (2) [(-1.72563e-31,-1.42109e-15,-7.77156e-16),(1300,-1.42109e-15,-7.77156e-16)]
  NodesOffset = 0
  Normal = (0,0,0)
  PerimeterLength = 2900
  Placement = pos=(9135,100,5800) rot=(0,0,1;0rad)
  PredefinedType = 0
  VerticalArea = 1160000
  Width = 150
FEATURE [Part::FeaturePython] Structure159  label="V15x40 V150"  # Arch/BIM 7 (typed FeaturePython)
  FaceMaker = 0
  Height = 400
  HorizontalArea = 445500
  IfcData = attributes={"GlobalId": {"name": "GlobalId", "type": "IfcGloballyUniqueId", "is_enum": false, "enum_values": []}, "Description": {"... (+475 chars omitted),+1 more (map truncated)
  IfcType = 7
  Length = 2970
  MoveBase = false
  MoveWithHost = false
  Nodes = (2) [(-1.72563e-31,-1.42109e-15,-7.77156e-16),(2970,-1.42109e-15,-7.77156e-16)]
  NodesOffset = 0
  Normal = (0,0,0)
  PerimeterLength = 6240
  Placement = pos=(10685,100,5800) rot=(0,0,1;0rad)
  PredefinedType = 0
  VerticalArea = 2.496e+06
  Width = 150
FEATURE [Part::FeaturePython] Structure160  label="V15x40 V151"  # Arch/BIM 7 (typed FeaturePython)
  FaceMaker = 0
  Height = 400
  HorizontalArea = 465000
  IfcData = attributes={"GlobalId": {"name": "GlobalId", "type": "IfcGloballyUniqueId", "is_enum": false, "enum_values": []}, "Description": {"... (+475 chars omitted),+1 more (map truncated)
  IfcType = 7
  Length = 3100
  MoveBase = false
  MoveWithHost = false
  Nodes = (2) [(-1.72563e-31,-1.42109e-15,-7.77156e-16),(3100,-1.42109e-15,-7.77156e-16)]
  NodesOffset = 0
  Normal = (0,0,0)
  PerimeterLength = 6500
  Placement = pos=(6160,3275,5800) rot=(0,0,-1;1.5708rad)
  PredefinedType = 0
  VerticalArea = 2.6e+06
  Width = 150
FEATURE [Part::FeaturePython] Structure161  label="V15x40 V152"  # Arch/BIM 7 (typed FeaturePython)
  FaceMaker = 0
  Height = 400
  HorizontalArea = 471000
  IfcData = attributes={"GlobalId": {"name": "GlobalId", "type": "IfcGloballyUniqueId", "is_enum": false, "enum_values": []}, "Description": {"... (+475 chars omitted),+1 more (map truncated)
  IfcType = 7
  Length = 3140
  MoveBase = false
  MoveWithHost = false
  Nodes = (2) [(-1.72563e-31,-1.42109e-15,-7.77156e-16),(3140,-1.42109e-15,-7.77156e-16)]
  NodesOffset = 0
  Normal = (0,0,0)
  PerimeterLength = 6580
  Placement = pos=(6160,6565,5800) rot=(0,0,-1;1.5708rad)
  PredefinedType = 0
  VerticalArea = 2.632e+06
  Width = 150
FEATURE [Part::FeaturePython] Structure162  label="V15x40 V153"  # Arch/BIM 7 (typed FeaturePython)
  FaceMaker = 0
  Height = 400
  HorizontalArea = 466500
  IfcData = attributes={"GlobalId": {"name": "GlobalId", "type": "IfcGloballyUniqueId", "is_enum": false, "enum_values": []}, "Description": {"... (+475 chars omitted),+1 more (map truncated)
  IfcType = 7
  Length = 3110
  MoveBase = false
  MoveWithHost = false
  Nodes = (2) [(-1.72563e-31,-1.42109e-15,-7.77156e-16),(3110,-1.42109e-15,-7.77156e-16)]
  NodesOffset = 0
  Normal = (0,0,0)
  PerimeterLength = 6520
  Placement = pos=(6160,9825,5800) rot=(0,0,-1;1.5708rad)
  PredefinedType = 0
  VerticalArea = 2.608e+06
  Width = 150
FEATURE [Part::FeaturePython] Structure163  label="V15x40 V154"  # Arch/BIM 7 (typed FeaturePython)
  FaceMaker = 0
  Height = 400
  HorizontalArea = 457500
  IfcData = attributes={"GlobalId": {"name": "GlobalId", "type": "IfcGloballyUniqueId", "is_enum": false, "enum_values": []}, "Description": {"... (+475 chars omitted),+1 more (map truncated)
  IfcType = 7
  Length = 3050
  MoveBase = false
  MoveWithHost = false
  Nodes = (2) [(-1.72563e-31,-1.42109e-15,-7.77156e-16),(3050,-1.42109e-15,-7.77156e-16)]
  NodesOffset = 0
  Normal = (0,0,0)
  PerimeterLength = 6400
  Placement = pos=(9010,3225,5800) rot=(0,0,-1;1.5708rad)
  PredefinedType = 0
  VerticalArea = 2.56e+06
  Width = 150
FEATURE [Part::FeaturePython] Structure164  label="V15x40 V155"  # Arch/BIM 7 (typed FeaturePython)
  FaceMaker = 0
  Height = 400
  HorizontalArea = 456000
  IfcData = attributes={"GlobalId": {"name": "GlobalId", "type": "IfcGloballyUniqueId", "is_enum": false, "enum_values": []}, "Description": {"... (+475 chars omitted),+1 more (map truncated)
  IfcType = 7
  Length = 3040
  MoveBase = false
  MoveWithHost = false
  Nodes = (2) [(-1.72563e-31,-1.42109e-15,-7.77156e-16),(3040,-1.42109e-15,-7.77156e-16)]
  NodesOffset = 0
  Normal = (0,0,0)
  PerimeterLength = 6380
  Placement = pos=(9010,6515,5800) rot=(0,0,-1;1.5708rad)
  PredefinedType = 0
  VerticalArea = 2.552e+06
  Width = 150
FEATURE [Part::FeaturePython] Structure165  label="V15x40 V156"  # Arch/BIM 7 (typed FeaturePython)
  FaceMaker = 0
  Height = 400
  HorizontalArea = 459000
  IfcData = attributes={"GlobalId": {"name": "GlobalId", "type": "IfcGloballyUniqueId", "is_enum": false, "enum_values": []}, "Description": {"... (+475 chars omitted),+1 more (map truncated)
  IfcType = 7
  Length = 3060
  MoveBase = false
  MoveWithHost = false
  Nodes = (2) [(-1.72563e-31,-1.42109e-15,-7.77156e-16),(3060,-1.42109e-15,-7.77156e-16)]
  NodesOffset = 0
  Normal = (0,0,0)
  PerimeterLength = 6420
  Placement = pos=(9010,9825,5800) rot=(0,0,-1;1.5708rad)
  PredefinedType = 0
  VerticalArea = 2.568e+06
  Width = 150
FEATURE [Part::FeaturePython] Structure166  label="V15x40 V157"  # Arch/BIM 7 (typed FeaturePython)
  FaceMaker = 0
  Height = 400
  HorizontalArea = 457500
  IfcData = attributes={"GlobalId": {"name": "GlobalId", "type": "IfcGloballyUniqueId", "is_enum": false, "enum_values": []}, "Description": {"... (+475 chars omitted),+1 more (map truncated)
  IfcType = 7
  Length = 3050
  MoveBase = false
  MoveWithHost = false
  Nodes = (2) [(-1.72563e-31,-1.42109e-15,-7.77156e-16),(3050,-1.42109e-15,-7.77156e-16)]
  NodesOffset = 0
  Normal = (0,0,0)
  PerimeterLength = 6400
  Placement = pos=(10560,3225,5800) rot=(0,0,-1;1.5708rad)
  PredefinedType = 0
  VerticalArea = 2.56e+06
  Width = 150
FEATURE [Part::FeaturePython] Structure167  label="V15x40 V158"  # Arch/BIM 7 (typed FeaturePython)
  FaceMaker = 0
  Height = 400
  HorizontalArea = 363000
  IfcData = attributes={"GlobalId": {"name": "GlobalId", "type": "IfcGloballyUniqueId", "is_enum": false, "enum_values": []}, "Description": {"... (+475 chars omitted),+1 more (map truncated)
  IfcType = 7
  Length = 2420
  MoveBase = false
  MoveWithHost = false
  Nodes = (2) [(-1.72563e-31,-1.42109e-15,-7.77156e-16),(2420,-1.42109e-15,-7.77156e-16)]
  NodesOffset = 0
  Normal = (0,0,0)
  PerimeterLength = 5140
  Placement = pos=(10560,3475,5800) rot=(0,0,1;1.5708rad)
  PredefinedType = 0
  VerticalArea = 2056000
  Width = 150
FEATURE [Part::FeaturePython] Structure168  label="V15x40 V159"  # Arch/BIM 7 (typed FeaturePython)
  FaceMaker = 0
  Height = 400
  HorizontalArea = 207000
  IfcData = attributes={"GlobalId": {"name": "GlobalId", "type": "IfcGloballyUniqueId", "is_enum": false, "enum_values": []}, "Description": {"... (+475 chars omitted),+1 more (map truncated)
  IfcType = 7
  Length = 1380
  MoveBase = false
  MoveWithHost = false
  Nodes = (2) [(-1.72563e-31,-1.42109e-15,-7.77156e-16),(1380,-1.42109e-15,-7.77156e-16)]
  NodesOffset = 0
  Normal = (0,0,0)
  PerimeterLength = 3060
  Placement = pos=(10560,8445,5800) rot=(0,0,1;1.5708rad)
  PredefinedType = 0
  VerticalArea = 1224000
  Width = 150
FEATURE [Part::FeaturePython] Structure169  label="V15x40 V160"  # Arch/BIM 7 (typed FeaturePython)
  FaceMaker = 0
  Height = 400
  HorizontalArea = 207000
  IfcData = attributes={"GlobalId": {"name": "GlobalId", "type": "IfcGloballyUniqueId", "is_enum": false, "enum_values": []}, "Description": {"... (+475 chars omitted),+1 more (map truncated)
  IfcType = 7
  Length = 1380
  MoveBase = false
  MoveWithHost = false
  Nodes = (2) [(-1.72563e-31,-1.42109e-15,-7.77156e-16),(1380,-1.42109e-15,-7.77156e-16)]
  NodesOffset = 0
  Normal = (0,0,0)
  PerimeterLength = 3060
  Placement = pos=(12010,9825,5800) rot=(0,0,-1;1.5708rad)
  PredefinedType = 0
  VerticalArea = 1224000
  Width = 150
FEATURE [Part::FeaturePython] Structure170  label="V20x40 V136"  # Arch/BIM 7 (typed FeaturePython)
  FaceMaker = 0
  Height = 400
  HorizontalArea = 615000
  IfcData = attributes={"GlobalId": {"name": "GlobalId", "type": "IfcGloballyUniqueId", "is_enum": false, "enum_values": []}, "Description": {"... (+475 chars omitted),+1 more (map truncated)
  IfcType = 7
  Length = 3075
  MoveBase = false
  MoveWithHost = false
  Nodes = (2) [(-1.72563e-31,0,-7.77156e-16),(3075,0,-7.77156e-16)]
  NodesOffset = 0
  Normal = (0,0,0)
  PerimeterLength = 6550
  Placement = pos=(1930,3250,5800) rot=(0,0,-1;1.5708rad)
  PredefinedType = 0
  VerticalArea = 2.62e+06
  Width = 200
FEATURE [Part::FeaturePython] Structure171  label="V20x40 V137"  # Arch/BIM 7 (typed FeaturePython)
  FaceMaker = 0
  Height = 400
  HorizontalArea = 618000
  IfcData = attributes={"GlobalId": {"name": "GlobalId", "type": "IfcGloballyUniqueId", "is_enum": false, "enum_values": []}, "Description": {"... (+475 chars omitted),+1 more (map truncated)
  IfcType = 7
  Length = 3090
  MoveBase = false
  MoveWithHost = false
  Nodes = (2) [(-1.72563e-31,0,-7.77156e-16),(3090,0,-7.77156e-16)]
  NodesOffset = 0
  Normal = (0,0,0)
  PerimeterLength = 6580
  Placement = pos=(1930,6540,5800) rot=(0,0,-1;1.5708rad)
  PredefinedType = 0
  VerticalArea = 2.632e+06
  Width = 200
FEATURE [Part::FeaturePython] Structure172  label="V20x40 V138"  # Arch/BIM 7 (typed FeaturePython)
  FaceMaker = 0
  Height = 400
  HorizontalArea = 617000
  IfcData = attributes={"GlobalId": {"name": "GlobalId", "type": "IfcGloballyUniqueId", "is_enum": false, "enum_values": []}, "Description": {"... (+475 chars omitted),+1 more (map truncated)
  IfcType = 7
  Length = 3085
  MoveBase = false
  MoveWithHost = false
  Nodes = (2) [(-1.72563e-31,0,-7.77156e-16),(3085,0,-7.77156e-16)]
  NodesOffset = 0
  Normal = (0,0,0)
  PerimeterLength = 6570
  Placement = pos=(1930,9825,5800) rot=(0,0,-1;1.5708rad)
  PredefinedType = 0
  VerticalArea = 2.628e+06
  Width = 200
FEATURE [Part::FeaturePython] Structure173  label="V20x40 V139"  # Arch/BIM 7 (typed FeaturePython)
  FaceMaker = 0
  Height = 400
  HorizontalArea = 635000
  IfcData = attributes={"GlobalId": {"name": "GlobalId", "type": "IfcGloballyUniqueId", "is_enum": false, "enum_values": []}, "Description": {"... (+475 chars omitted),+1 more (map truncated)
  IfcType = 7
  Length = 3175
  MoveBase = false
  MoveWithHost = false
  Nodes = (2) [(-1.72563e-31,0,-7.77156e-16),(3175,0,-7.77156e-16)]
  NodesOffset = 0
  Normal = (0,0,0)
  PerimeterLength = 6750
  Placement = pos=(13780,175,5800) rot=(0,0,1;1.5708rad)
  PredefinedType = 0
  VerticalArea = 2.7e+06
  Width = 200
FEATURE [Part::FeaturePython] Structure174  label="V20x40 V140"  # Arch/BIM 7 (typed FeaturePython)
  FaceMaker = 0
  Height = 400
  HorizontalArea = 509000
  IfcData = attributes={"GlobalId": {"name": "GlobalId", "type": "IfcGloballyUniqueId", "is_enum": false, "enum_values": []}, "Description": {"... (+475 chars omitted),+1 more (map truncated)
  IfcType = 7
  Length = 2545
  MoveBase = false
  MoveWithHost = false
  Nodes = (2) [(-1.72563e-31,0,-7.77156e-16),(2545,0,-7.77156e-16)]
  NodesOffset = 0
  Normal = (0,0,0)
  PerimeterLength = 5490
  Placement = pos=(13780,3350,5800) rot=(0,0,1;1.5708rad)
  PredefinedType = 0
  VerticalArea = 2196000
  Width = 200
FEATURE [Part::FeaturePython] Structure175  label="V20x40 V141"  # Arch/BIM 7 (typed FeaturePython)
  FaceMaker = 0
  Height = 400
  HorizontalArea = 756000
  IfcData = attributes={"GlobalId": {"name": "GlobalId", "type": "IfcGloballyUniqueId", "is_enum": false, "enum_values": []}, "Description": {"... (+475 chars omitted),+1 more (map truncated)
  IfcType = 7
  Length = 3780
  MoveBase = false
  MoveWithHost = false
  Nodes = (2) [(-1.72563e-31,0,-7.77156e-16),(3780,0,-7.77156e-16)]
  NodesOffset = 0
  Normal = (0,0,0)
  PerimeterLength = 7960
  Placement = pos=(15210,6045,5800) rot=(0,0,1;1.5708rad)
  PredefinedType = 0
  VerticalArea = 3.184e+06
  Width = 200
FEATURE [Part::FeaturePython] Structure176  label="25x15 C026"  # Arch/BIM 24 (typed FeaturePython)
  FaceMaker = 0
  Height = 3000
  HorizontalArea = 37500
  IfcData = attributes={"GlobalId": {"name": "GlobalId", "type": "IfcGloballyUniqueId", "is_enum": false, "enum_values": []}, "Description": {"... (+438 chars omitted),+1 more (map truncated)
  IfcType = 24
  Length = 250
  MoveBase = false
  MoveWithHost = false
  Nodes = (2) [(-1.05471e-15,1.36424e-15,0),(-1.05471e-15,1.36424e-15,3000)]
  NodesOffset = 0
  Normal = (0,0,0)
  PerimeterLength = 800
  Placement = pos=(1930,9900,3000) rot=(0,0,1;0rad)
  PredefinedType = 0
  VerticalArea = 2400000
  Width = 150
FEATURE [Part::FeaturePython] Structure177  label="25x15 C027"  # Arch/BIM 172 (typed FeaturePython)
  FaceMaker = 0
  Height = 3000
  HorizontalArea = 37500
  IfcData = attributes={"GlobalId": {"name": "GlobalId", "type": "IfcGloballyUniqueId", "is_enum": false, "enum_values": []}, "Description": {"... (+484 chars omitted),+1 more (map truncated)
  IfcType = 172
  Length = 250
  MoveBase = false
  MoveWithHost = false
  Nodes = (2) [(-1.05471e-15,1.36424e-15,0),(-1.05471e-15,1.36424e-15,3000)]
  NodesOffset = 0
  Normal = (0,0,0)
  PerimeterLength = 800
  Placement = pos=(1930,100,3000) rot=(0,0,1;0rad)
  PredefinedType = 0
  VerticalArea = 2400000
  Width = 150
FEATURE [Part::FeaturePython] Structure178  label="25x20 C008"  # Arch/BIM 24 (typed FeaturePython)
  FaceMaker = 0
  Height = 3000
  HorizontalArea = 50000
  IfcData = attributes={"GlobalId": {"name": "GlobalId", "type": "IfcGloballyUniqueId", "is_enum": false, "enum_values": []}, "Description": {"... (+438 chars omitted),+1 more (map truncated)
  IfcType = 24
  Length = 250
  MoveBase = false
  MoveWithHost = false
  Nodes = (2) [(-1.05471e-15,-1.81899e-15,0),(-1.05471e-15,-1.81899e-15,3000)]
  NodesOffset = 0
  Normal = (0,0,0)
  PerimeterLength = 900
  Placement = pos=(1930,6640,3000) rot=(0,0,1;0rad)
  PredefinedType = 0
  VerticalArea = 2700000
  Width = 200
FEATURE [Part::FeaturePython] Structure180  label="25x15 C028"  # Arch/BIM 24 (typed FeaturePython)
  FaceMaker = 0
  Height = 3000
  HorizontalArea = 37500
  IfcData = attributes={"GlobalId": {"name": "GlobalId", "type": "IfcGloballyUniqueId", "is_enum": false, "enum_values": []}, "Description": {"... (+438 chars omitted),+1 more (map truncated)
  IfcType = 24
  Length = 250
  MoveBase = false
  MoveWithHost = false
  Nodes = (2) [(-1.05471e-15,1.36424e-15,0),(-1.05471e-15,1.36424e-15,3000)]
  NodesOffset = 0
  Normal = (0,0,0)
  PerimeterLength = 800
  Placement = pos=(6160,6640,3000) rot=(0,0,1;0rad)
  PredefinedType = 0
  VerticalArea = 2400000
  Width = 150
FEATURE [Part::FeaturePython] Structure181  label="25x15 C029"  # Arch/BIM 24 (typed FeaturePython)
  FaceMaker = 0
  Height = 3000
  HorizontalArea = 37500
  IfcData = attributes={"GlobalId": {"name": "GlobalId", "type": "IfcGloballyUniqueId", "is_enum": false, "enum_values": []}, "Description": {"... (+438 chars omitted),+1 more (map truncated)
  IfcType = 24
  Length = 250
  MoveBase = false
  MoveWithHost = false
  Nodes = (2) [(-1.05471e-15,1.36424e-15,0),(-1.05471e-15,1.36424e-15,3000)]
  NodesOffset = 0
  Normal = (0,0,0)
  PerimeterLength = 800
  Placement = pos=(6160,3350,3000) rot=(0,0,1;0rad)
  PredefinedType = 0
  VerticalArea = 2400000
  Width = 150
FEATURE [Part::FeaturePython] Structure182  label="25x15 C030"  # Arch/BIM 24 (typed FeaturePython)
  FaceMaker = 0
  Height = 3000
  HorizontalArea = 37500
  IfcData = attributes={"GlobalId": {"name": "GlobalId", "type": "IfcGloballyUniqueId", "is_enum": false, "enum_values": []}, "Description": {"... (+438 chars omitted),+1 more (map truncated)
  IfcType = 24
  Length = 250
  MoveBase = false
  MoveWithHost = false
  Nodes = (2) [(-1.05471e-15,1.36424e-15,0),(-1.05471e-15,1.36424e-15,3000)]
  NodesOffset = 0
  Normal = (0,0,0)
  PerimeterLength = 800
  Placement = pos=(6160,100,3000) rot=(0,0,1;0rad)
  PredefinedType = 0
  VerticalArea = 2400000
  Width = 150
FEATURE [Part::FeaturePython] Structure183  label="25x15 C031"  # Arch/BIM 24 (typed FeaturePython)
  FaceMaker = 0
  Height = 3000
  HorizontalArea = 37500
  IfcData = attributes={"GlobalId": {"name": "GlobalId", "type": "IfcGloballyUniqueId", "is_enum": false, "enum_values": []}, "Description": {"... (+438 chars omitted),+1 more (map truncated)
  IfcType = 24
  Length = 250
  MoveBase = false
  MoveWithHost = false
  Nodes = (2) [(-1.05471e-15,1.36424e-15,0),(-1.05471e-15,1.36424e-15,3000)]
  NodesOffset = 0
  Normal = (0,0,0)
  PerimeterLength = 800
  Placement = pos=(9010,100,3000) rot=(0,0,1;0rad)
  PredefinedType = 0
  VerticalArea = 2400000
  Width = 150
FEATURE [Part::FeaturePython] Structure184  label="25x15 C032"  # Arch/BIM 24 (typed FeaturePython)
  FaceMaker = 0
  Height = 3000
  HorizontalArea = 37500
  IfcData = attributes={"GlobalId": {"name": "GlobalId", "type": "IfcGloballyUniqueId", "is_enum": false, "enum_values": []}, "Description": {"... (+438 chars omitted),+1 more (map truncated)
  IfcType = 24
  Length = 250
  MoveBase = false
  MoveWithHost = false
  Nodes = (2) [(-1.05471e-15,1.36424e-15,0),(-1.05471e-15,1.36424e-15,3000)]
  NodesOffset = 0
  Normal = (0,0,0)
  PerimeterLength = 800
  Placement = pos=(10560,100,3000) rot=(0,0,1;0rad)
  PredefinedType = 0
  VerticalArea = 2400000
  Width = 150
FEATURE [Part::FeaturePython] Structure185  label="25x15 C033"  # Arch/BIM 24 (typed FeaturePython)
  FaceMaker = 0
  Height = 3000
  HorizontalArea = 37500
  IfcData = attributes={"GlobalId": {"name": "GlobalId", "type": "IfcGloballyUniqueId", "is_enum": false, "enum_values": []}, "Description": {"... (+438 chars omitted),+1 more (map truncated)
  IfcType = 24
  Length = 250
  MoveBase = false
  MoveWithHost = false
  Nodes = (2) [(-1.05471e-15,1.36424e-15,0),(-1.05471e-15,1.36424e-15,3000)]
  NodesOffset = 0
  Normal = (0,0,0)
  PerimeterLength = 800
  Placement = pos=(13780,100,3000) rot=(0,0,1;0rad)
  PredefinedType = 0
  VerticalArea = 2400000
  Width = 150
FEATURE [Part::FeaturePython] Structure186  label="25x15 C034"  # Arch/BIM 24 (typed FeaturePython)
  FaceMaker = 0
  Height = 3000
  HorizontalArea = 37500
  IfcData = attributes={"GlobalId": {"name": "GlobalId", "type": "IfcGloballyUniqueId", "is_enum": false, "enum_values": []}, "Description": {"... (+438 chars omitted),+1 more (map truncated)
  IfcType = 24
  Length = 250
  MoveBase = false
  MoveWithHost = false
  Nodes = (2) [(-1.05471e-15,1.36424e-15,0),(-1.05471e-15,1.36424e-15,3000)]
  NodesOffset = 0
  Normal = (0,0,0)
  PerimeterLength = 800
  Placement = pos=(15210,5970,3000) rot=(0,0,1;0rad)
  PredefinedType = 0
  VerticalArea = 2400000
  Width = 150
FEATURE [Part::FeaturePython] Structure187  label="25x15 C035"  # Arch/BIM 24 (typed FeaturePython)
  FaceMaker = 0
  Height = 3000
  HorizontalArea = 37500
  IfcData = attributes={"GlobalId": {"name": "GlobalId", "type": "IfcGloballyUniqueId", "is_enum": false, "enum_values": []}, "Description": {"... (+438 chars omitted),+1 more (map truncated)
  IfcType = 24
  Length = 250
  MoveBase = false
  MoveWithHost = false
  Nodes = (2) [(-1.05471e-15,1.36424e-15,0),(-1.05471e-15,1.36424e-15,3000)]
  NodesOffset = 0
  Normal = (0,0,0)
  PerimeterLength = 800
  Placement = pos=(13780,5970,3000) rot=(0,0,1;0rad)
  PredefinedType = 0
  VerticalArea = 2400000
  Width = 150
FEATURE [Part::FeaturePython] Structure188  label="25x15 C036"  # Arch/BIM 172 (typed FeaturePython)
  FaceMaker = 0
  Height = 3000
  HorizontalArea = 37500
  IfcData = attributes={"GlobalId": {"name": "GlobalId", "type": "IfcGloballyUniqueId", "is_enum": false, "enum_values": []}, "Description": {"... (+484 chars omitted),+1 more (map truncated)
  IfcType = 172
  Length = 250
  MoveBase = false
  MoveWithHost = false
  Nodes = (2) [(-1.05471e-15,1.36424e-15,0),(-1.05471e-15,1.36424e-15,3000)]
  NodesOffset = 0
  Normal = (0,0,0)
  PerimeterLength = 800
  Placement = pos=(1930,9900,3000) rot=(0,0,1;0rad)
  PredefinedType = 0
  VerticalArea = 2400000
  Width = 150
FEATURE [Part::FeaturePython] Structure189  label="25x15 C037"  # Arch/BIM 172 (typed FeaturePython)
  FaceMaker = 0
  Height = 3000
  HorizontalArea = 37500
  IfcData = attributes={"GlobalId": {"name": "GlobalId", "type": "IfcGloballyUniqueId", "is_enum": false, "enum_values": []}, "Description": {"... (+484 chars omitted),+1 more (map truncated)
  IfcType = 172
  Length = 250
  MoveBase = false
  MoveWithHost = false
  Nodes = (2) [(-1.05471e-15,1.36424e-15,0),(-1.05471e-15,1.36424e-15,3000)]
  NodesOffset = 0
  Normal = (0,0,0)
  PerimeterLength = 800
  Placement = pos=(9010,6640,3000) rot=(0,0,1;1.5708rad)
  PredefinedType = 0
  VerticalArea = 2400000
  Width = 150
FEATURE [Part::FeaturePython] Structure190  label="25x15 C038"  # Arch/BIM 172 (typed FeaturePython)
  FaceMaker = 0
  Height = 3000
  HorizontalArea = 37500
  IfcData = attributes={"GlobalId": {"name": "GlobalId", "type": "IfcGloballyUniqueId", "is_enum": false, "enum_values": []}, "Description": {"... (+484 chars omitted),+1 more (map truncated)
  IfcType = 172
  Length = 250
  MoveBase = false
  MoveWithHost = false
  Nodes = (2) [(-1.05471e-15,1.36424e-15,0),(-1.05471e-15,1.36424e-15,3000)]
  NodesOffset = 0
  Normal = (0,0,0)
  PerimeterLength = 800
  Placement = pos=(9010,3350,3000) rot=(0,0,1;1.5708rad)
  PredefinedType = 0
  VerticalArea = 2400000
  Width = 150
FEATURE [Part::FeaturePython] Structure191  label="25x15 C039"  # Arch/BIM 172 (typed FeaturePython)
  FaceMaker = 0
  Height = 3000
  HorizontalArea = 37500
  IfcData = attributes={"GlobalId": {"name": "GlobalId", "type": "IfcGloballyUniqueId", "is_enum": false, "enum_values": []}, "Description": {"... (+484 chars omitted),+1 more (map truncated)
  IfcType = 172
  Length = 250
  MoveBase = false
  MoveWithHost = false
  Nodes = (2) [(-1.05471e-15,1.36424e-15,0),(-1.05471e-15,1.36424e-15,3000)]
  NodesOffset = 0
  Normal = (0,0,0)
  PerimeterLength = 800
  Placement = pos=(10560,3350,3000) rot=(0,0,1;1.5708rad)
  PredefinedType = 0
  VerticalArea = 2400000
  Width = 150
FEATURE [Part::FeaturePython] Structure192  label="25x15 C040"  # Arch/BIM 172 (typed FeaturePython)
  FaceMaker = 0
  Height = 3000
  HorizontalArea = 37500
  IfcData = attributes={"GlobalId": {"name": "GlobalId", "type": "IfcGloballyUniqueId", "is_enum": false, "enum_values": []}, "Description": {"... (+484 chars omitted),+1 more (map truncated)
  IfcType = 172
  Length = 250
  MoveBase = false
  MoveWithHost = false
  Nodes = (2) [(-1.05471e-15,1.36424e-15,0),(-1.05471e-15,1.36424e-15,3000)]
  NodesOffset = 0
  Normal = (0,0,0)
  PerimeterLength = 800
  Placement = pos=(13780,3350,3000) rot=(0,0,1;1.5708rad)
  PredefinedType = 0
  VerticalArea = 2400000
  Width = 150
FEATURE [Part::FeaturePython] Structure193  label="25x15 C041"  # Arch/BIM 172 (typed FeaturePython)
  FaceMaker = 0
  Height = 3000
  HorizontalArea = 37500
  IfcData = attributes={"GlobalId": {"name": "GlobalId", "type": "IfcGloballyUniqueId", "is_enum": false, "enum_values": []}, "Description": {"... (+484 chars omitted),+1 more (map truncated)
  IfcType = 172
  Length = 250
  MoveBase = false
  MoveWithHost = false
  Nodes = (2) [(-1.05471e-15,1.36424e-15,0),(-1.05471e-15,1.36424e-15,3000)]
  NodesOffset = 0
  Normal = (0,0,0)
  PerimeterLength = 800
  Placement = pos=(9010,9900,3000) rot=(0,0,1;0rad)
  PredefinedType = 0
  VerticalArea = 2400000
  Width = 150
FEATURE [Part::FeaturePython] Structure194  label="25x15 C042"  # Arch/BIM 172 (typed FeaturePython)
  FaceMaker = 0
  Height = 3000
  HorizontalArea = 37500
  IfcData = attributes={"GlobalId": {"name": "GlobalId", "type": "IfcGloballyUniqueId", "is_enum": false, "enum_values": []}, "Description": {"... (+484 chars omitted),+1 more (map truncated)
  IfcType = 172
  Length = 250
  MoveBase = false
  MoveWithHost = false
  Nodes = (2) [(-1.05471e-15,1.36424e-15,0),(-1.05471e-15,1.36424e-15,3000)]
  NodesOffset = 0
  Normal = (0,0,0)
  PerimeterLength = 800
  Placement = pos=(6160,9900,3000) rot=(0,0,1;0rad)
  PredefinedType = 0
  VerticalArea = 2400000
  Width = 150
FEATURE [Part::FeaturePython] Structure195  label="25x15 C043"  # Arch/BIM 172 (typed FeaturePython)
  FaceMaker = 0
  Height = 3000
  HorizontalArea = 37500
  IfcData = attributes={"GlobalId": {"name": "GlobalId", "type": "IfcGloballyUniqueId", "is_enum": false, "enum_values": []}, "Description": {"... (+484 chars omitted),+1 more (map truncated)
  IfcType = 172
  Length = 250
  MoveBase = false
  MoveWithHost = false
  Nodes = (2) [(-1.05471e-15,1.36424e-15,0),(-1.05471e-15,1.36424e-15,3000)]
  NodesOffset = 0
  Normal = (0,0,0)
  PerimeterLength = 800
  Placement = pos=(12010,9900,3000) rot=(0,0,1;0rad)
  PredefinedType = 0
  VerticalArea = 2400000
  Width = 150
FEATURE [Part::FeaturePython] Structure196  label="25x15 C044"  # Arch/BIM 172 (typed FeaturePython)
  FaceMaker = 0
  Height = 3000
  HorizontalArea = 37500
  IfcData = attributes={"GlobalId": {"name": "GlobalId", "type": "IfcGloballyUniqueId", "is_enum": false, "enum_values": []}, "Description": {"... (+484 chars omitted),+1 more (map truncated)
  IfcType = 172
  Length = 250
  MoveBase = false
  MoveWithHost = false
  Nodes = (2) [(-1.05471e-15,1.36424e-15,0),(-1.05471e-15,1.36424e-15,3000)]
  NodesOffset = 0
  Normal = (0,0,0)
  PerimeterLength = 800
  Placement = pos=(15210,9900,3000) rot=(0,0,1;0rad)
  PredefinedType = 0
  VerticalArea = 2400000
  Width = 150
FEATURE [Part::FeaturePython] Structure179  label="25x20 C009"  # Arch/BIM 172 (typed FeaturePython)
  FaceMaker = 0
  Height = 3000
  HorizontalArea = 50000
  IfcData = attributes={"GlobalId": {"name": "GlobalId", "type": "IfcGloballyUniqueId", "is_enum": false, "enum_values": []}, "Description": {"... (+484 chars omitted),+1 more (map truncated)
  IfcType = 172
  Length = 250
  MoveBase = false
  MoveWithHost = false
  Nodes = (2) [(-1.05471e-15,-1.81899e-15,0),(-1.05471e-15,-1.81899e-15,3000)]
  NodesOffset = 0
  Normal = (0,0,0)
  PerimeterLength = 900
  Placement = pos=(1930,3350,3000) rot=(0,0,1;0rad)
  PredefinedType = 0
  VerticalArea = 2700000
  Width = 200
FEATURE [App::GeometryPython] BuildingPart012  label="Columnas P1"  # Arch/BIM 172 (typed FeaturePython)
  Area = 0
  Group = -> [Structure176,Structure177,Structure180,Structure181,Structure182,Structure183,Structure184,Structure185,Structure186,Structure187,Structure188,Structure189,Structure190,Structure191,Structure192,Structure193,Structure194,Structure195,Structure196,Structure178,Structure179]
  Height = 0
  HeightPropagate = true
  IfcData = attributes={"GlobalId": {"name": "GlobalId", "type": "IfcGloballyUniqueId", "is_enum": false, "enum_values": []}, "Description": {"... (+484 chars omitted),+1 more (map truncated)
  IfcType = 172
  LevelOffset = 0
  PredefinedType = 0
FEATURE [Part::FeaturePython] Wall002  label="Tabique Ascensor P1"  # Arch/BIM 166 (typed FeaturePython)
  Align = 1
  Area = 24900000
  Base = -> Rectangle003
  BlockHeight = 0
  BlockLength = 0
  CountBroken = 0
  CountEntire = 0
  Face = 0
  Height = 3000
  HorizontalArea = 1155000
  IfcData = attributes={"GlobalId": {"name": "GlobalId", "type": "IfcGloballyUniqueId", "is_enum": false, "enum_values": []}, "Description": {"... (+533 chars omitted),+1 more (map truncated)
  IfcType = 166
  Joint = 0
  Length = 8300
  MakeBlocks = false
  MoveBase = false
  MoveWithHost = false
  Normal = (0,0,0)
  OffsetFirst = 0
  OffsetSecond = 0
  PerimeterLength = 8300
  Placement = pos=(0,0,3000) rot=(0,0,1;0rad)
  PredefinedType = 0
  VerticalArea = 46200000
  Width = 150
FEATURE [Part::Part2DObjectPython] Rectangle004  # Draft 2D object (typed FeaturePython)
  Area = 12611050
  ChamferSize = 0
  Columns = 1
  FilletRadius = 0
  Height = 3110
  Length = 4055
  MakeFace = true
  Placement = pos=(2030,6715,3000) rot=(0,0,1;0rad)
  Rows = 1
FEATURE [Part::Part2DObjectPython] Rectangle005  # Draft 2D object (typed FeaturePython)
  Area = 12732700
  ChamferSize = 0
  Columns = 1
  FilletRadius = 0
  Height = 3140
  Length = 4055
  MakeFace = true
  Placement = pos=(2030,3425,3000) rot=(0,0,1;0rad)
  Rows = 1
FEATURE [Part::Part2DObjectPython] Rectangle006  # Draft 2D object (typed FeaturePython)
  Area = 1.25705e+07
  ChamferSize = 0
  Columns = 1
  FilletRadius = 0
  Height = 3100
  Length = 4055
  MakeFace = true
  Placement = pos=(2030,175,3000) rot=(0,0,1;0rad)
  Rows = 1
FEATURE [Part::Part2DObjectPython] Rectangle008  # Draft 2D object (typed FeaturePython)
  Area = 4354000
  ChamferSize = 0
  Columns = 1
  FilletRadius = 0
  Height = 3110
  Length = 1400
  MakeFace = true
  Placement = pos=(9085,6715,3000) rot=(0,0,1;0rad)
  Rows = 1
FEATURE [Part::Part2DObjectPython] Rectangle009  # Draft 2D object (typed FeaturePython)
  Area = 1.794e+06
  ChamferSize = 0
  Columns = 1
  FilletRadius = 0
  Height = 1380
  Length = 1300
  MakeFace = true
  Placement = pos=(10635,8445,3000) rot=(0,0,1;0rad)
  Rows = 1
FEATURE [Part::Part2DObjectPython] Rectangle011  # Draft 2D object (typed FeaturePython)
  Area = 4396000
  ChamferSize = 0
  Columns = 1
  FilletRadius = 0
  Height = 3140
  Length = 1400
  MakeFace = true
  Placement = pos=(9085,3425,3000) rot=(0,0,1;0rad)
  Rows = 1
FEATURE [Part::Part2DObjectPython] Rectangle013  # Draft 2D object (typed FeaturePython)
  Area = 4.34e+06
  ChamferSize = 0
  Columns = 1
  FilletRadius = 0
  Height = 3100
  Length = 1400
  MakeFace = true
  Placement = pos=(9085,175,3000) rot=(0,0,1;0rad)
  Rows = 1
FEATURE [Part::Part2DObjectPython] Rectangle014  # Draft 2D object (typed FeaturePython)
  Area = 3928500
  ChamferSize = 0
  Columns = 1
  FilletRadius = 0
  Height = 1455
  Length = 2700
  MakeFace = true
  Placement = pos=(6235,8370,3000) rot=(0,0,1;0rad)
  Rows = 1
FEATURE [Part::Part2DObjectPython] Rectangle015  # Draft 2D object (typed FeaturePython)
  Area = 4.0365e+06
  ChamferSize = 0
  Columns = 1
  FilletRadius = 0
  Height = 1495
  Length = 2700
  MakeFace = true
  Placement = pos=(6235,3425,3000) rot=(0,0,1;0rad)
  Rows = 1
FEATURE [Part::Part2DObjectPython] Rectangle016  # Draft 2D object (typed FeaturePython)
  Area = 3.915e+06
  ChamferSize = 0
  Columns = 1
  FilletRadius = 0
  Height = 1450
  Length = 2700
  MakeFace = true
  Placement = pos=(6235,175,3000) rot=(0,0,1;0rad)
  Rows = 1
FEATURE [Part::Part2DObjectPython] Wire  # Draft 2D object (typed FeaturePython)
  Area = 3.9285e+06
  ChamferSize = 0
  Closed = true
  End = (8935,6715,3000)
  FilletRadius = 0
  Length = 8410
  MakeFace = true
  Placement = pos=(6235,6715,3000) rot=(0,0,1;0rad)
  Points = (6) [(0,0,0),(0,1505,0),(2400,1505,0),(2400,1055,0),(2700,1055,0),(2700,9.09495e-13,0)]
  Start = (6235,6715,3000)
  Subdivisions = 0
FEATURE [Part::Part2DObjectPython] Wire001  # Draft 2D object (typed FeaturePython)
  Area = 3.90134e+06
  ChamferSize = 0
  Closed = true
  End = (6235,5070,3000)
  FilletRadius = 0
  Length = 8389.89
  MakeFace = true
  Placement = pos=(6235,6565,3000) rot=(0,0,1;0rad)
  Points = (6) [(0,0,0),(2700,0,0),(2700,-1044.89,0),(2400,-1044.89,0),(2400,-1494.89,0),(0,-1495,0)]
  Start = (6235,6565,3000)
  Subdivisions = 0
FEATURE [Part::Part2DObjectPython] Wire002  # Draft 2D object (typed FeaturePython)
  Area = 3.91484e+06
  ChamferSize = 0
  Closed = true
  End = (6235,1775,3000)
  FilletRadius = 0
  Length = 8399.89
  MakeFace = true
  Placement = pos=(6235,3275,3000) rot=(0,0,1;0rad)
  Points = (6) [(0,0,0),(2700,-4.54747e-13,0),(2700,-1049.89,0),(2400,-1049.89,0),(2400,-1499.89,0),(0,-1500,0)]
  Start = (6235,3275,3000)
  Subdivisions = 0
FEATURE [Part::Part2DObjectPython] Rectangle017  # Draft 2D object (typed FeaturePython)
  Area = 4174500
  ChamferSize = 0
  Columns = 1
  FilletRadius = 0
  Height = 1380
  Length = 3025
  MakeFace = true
  Placement = pos=(12085,8445,3000) rot=(0,0,1;0rad)
  Rows = 1
FEATURE [Part::Part2DObjectPython] Rectangle018  # Draft 2D object (typed FeaturePython)
  Area = 3.211e+06
  ChamferSize = 0
  Columns = 1
  FilletRadius = 0
  Height = 2470
  Length = 1300
  MakeFace = true
  Placement = pos=(10635,3425,3000) rot=(0,0,1;0rad)
  Rows = 1
FEATURE [Part::Part2DObjectPython] Rectangle019  # Draft 2D object (typed FeaturePython)
  Area = 3.93965e+06
  ChamferSize = 0
  Columns = 1
  FilletRadius = 0
  Height = 2470
  Length = 1595
  MakeFace = true
  Placement = pos=(12085,3425,3000) rot=(0,0,1;0rad)
  Rows = 1
FEATURE [Part::Part2DObjectPython] Rectangle020  # Draft 2D object (typed FeaturePython)
  Area = 9439500
  ChamferSize = 0
  Columns = 1
  FilletRadius = 0
  Height = 3100
  Length = 3045
  MakeFace = true
  Placement = pos=(10635,175,3000) rot=(0,0,1;0rad)
  Rows = 1
FEATURE [Part::FeaturePython] Structure219  label="L118"  # Arch/BIM 172 (typed FeaturePython)
  Base = -> Rectangle004
  FaceMaker = 0
  Height = 150
  HorizontalArea = 12611050
  IfcData = attributes={"GlobalId": {"name": "GlobalId", "type": "IfcGloballyUniqueId", "is_enum": false, "enum_values": []}, "Description": {"... (+484 chars omitted),+1 more (map truncated)
  IfcType = 172
  Length = 0
  MoveBase = false
  MoveWithHost = false
  Nodes = (2) [(4057.5,8270,3000),(4057.5,8270,2850)]
  NodesOffset = 0
  Normal = (0,0,-1)
  PerimeterLength = 14330
  Placement = pos=(0,0,3000) rot=(0,0,1;0rad)
  PredefinedType = 0
  VerticalArea = 2149500
  Width = 150
FEATURE [Part::FeaturePython] Structure220  label="L119"  # Arch/BIM 172 (typed FeaturePython)
  Base = -> Rectangle005
  FaceMaker = 0
  Height = 150
  HorizontalArea = 12732700
  IfcData = attributes={"GlobalId": {"name": "GlobalId", "type": "IfcGloballyUniqueId", "is_enum": false, "enum_values": []}, "Description": {"... (+484 chars omitted),+1 more (map truncated)
  IfcType = 172
  Length = 0
  MoveBase = false
  MoveWithHost = false
  Nodes = (2) [(4057.5,4995,3000),(4057.5,4995,2850)]
  NodesOffset = 0
  Normal = (0,0,-1)
  PerimeterLength = 14390
  Placement = pos=(0,0,3000) rot=(0,0,1;0rad)
  PredefinedType = 0
  VerticalArea = 2158500
  Width = 150
FEATURE [Part::FeaturePython] Structure221  label="L120"  # Arch/BIM 172 (typed FeaturePython)
  Base = -> Rectangle006
  FaceMaker = 0
  Height = 150
  HorizontalArea = 1.25705e+07
  IfcData = attributes={"GlobalId": {"name": "GlobalId", "type": "IfcGloballyUniqueId", "is_enum": false, "enum_values": []}, "Description": {"... (+484 chars omitted),+1 more (map truncated)
  IfcType = 172
  Length = 0
  MoveBase = false
  MoveWithHost = false
  Nodes = (2) [(4057.5,1725,3000),(4057.5,1725,2850)]
  NodesOffset = 0
  Normal = (0,0,-1)
  PerimeterLength = 14310
  Placement = pos=(0,0,3000) rot=(0,0,1;0rad)
  PredefinedType = 0
  VerticalArea = 2146500
  Width = 150
FEATURE [Part::FeaturePython] Structure222  label="V15x40 V102a001"  # Arch/BIM 7 (typed FeaturePython)
  FaceMaker = 0
  Height = 400
  HorizontalArea = 405000
  IfcData = attributes={"GlobalId": {"name": "GlobalId", "type": "IfcGloballyUniqueId", "is_enum": false, "enum_values": []}, "Description": {"... (+475 chars omitted),+1 more (map truncated)
  IfcType = 7
  Length = 2700
  MoveBase = false
  MoveWithHost = false
  Nodes = (2) [(-1.72563e-31,-1.42109e-15,-7.77156e-16),(2700,-1.42109e-15,-7.77156e-16)]
  NodesOffset = 0
  Normal = (0,0,0)
  PerimeterLength = 5700
  Placement = pos=(8935,8295,5800) rot=(0,0,1;3.14159rad)
  PredefinedType = 0
  VerticalArea = 2.28e+06
  Width = 150
FEATURE [Part::FeaturePython] Structure223  label="V15x40 V107a001"  # Arch/BIM 7 (typed FeaturePython)
  FaceMaker = 0
  Height = 400
  HorizontalArea = 405000
  IfcData = attributes={"GlobalId": {"name": "GlobalId", "type": "IfcGloballyUniqueId", "is_enum": false, "enum_values": []}, "Description": {"... (+475 chars omitted),+1 more (map truncated)
  IfcType = 7
  Length = 2700
  MoveBase = false
  MoveWithHost = false
  Nodes = (2) [(-1.72563e-31,-1.42109e-15,-7.77156e-16),(2700,-1.42109e-15,-7.77156e-16)]
  NodesOffset = 0
  Normal = (0,0,0)
  PerimeterLength = 5700
  Placement = pos=(8935,4995,5800) rot=(0,0,1;3.14159rad)
  PredefinedType = 0
  VerticalArea = 2.28e+06
  Width = 150
FEATURE [Part::FeaturePython] Structure224  label="V15x40 V112a001"  # Arch/BIM 7 (typed FeaturePython)
  FaceMaker = 0
  Height = 400
  HorizontalArea = 405000
  IfcData = attributes={"GlobalId": {"name": "GlobalId", "type": "IfcGloballyUniqueId", "is_enum": false, "enum_values": []}, "Description": {"... (+475 chars omitted),+1 more (map truncated)
  IfcType = 7
  Length = 2700
  MoveBase = false
  MoveWithHost = false
  Nodes = (2) [(-1.72563e-31,-1.42109e-15,-7.77156e-16),(2700,-1.42109e-15,-7.77156e-16)]
  NodesOffset = 0
  Normal = (0,0,0)
  PerimeterLength = 5700
  Placement = pos=(8935,1700,5800) rot=(0,0,1;3.14159rad)
  PredefinedType = 0
  VerticalArea = 2.28e+06
  Width = 150
FEATURE [Part::FeaturePython] Structure225  label="V15x40 V130a001"  # Arch/BIM 7 (typed FeaturePython)
  FaceMaker = 0
  Height = 400
  HorizontalArea = 370500
  IfcData = attributes={"GlobalId": {"name": "GlobalId", "type": "IfcGloballyUniqueId", "is_enum": false, "enum_values": []}, "Description": {"... (+475 chars omitted),+1 more (map truncated)
  IfcType = 7
  Length = 2470
  MoveBase = false
  MoveWithHost = false
  Nodes = (2) [(-1.72563e-31,-1.42109e-15,-7.77156e-16),(2470,-1.42109e-15,-7.77156e-16)]
  NodesOffset = 0
  Normal = (0,0,0)
  PerimeterLength = 5240
  Placement = pos=(12010,3425,5800) rot=(0,0,1;1.5708rad)
  PredefinedType = 0
  VerticalArea = 2096000
  Width = 150
FEATURE [App::GeometryPython] BuildingPart011  label="Vigas sobre P1"  # Arch/BIM 172 (typed FeaturePython)
  Area = 0
  Group = -> [Structure222,Structure223,Structure224,Structure225,Structure142,Structure143,Structure144,Structure145,Structure146,Structure147,Structure148,Structure149,Structure150,Structure151,Structure152,Structure153,Structure154,Structure155,Structure156,Structure157,Structure158,Structure159,Structure160,Structure161,Structure162,Structure163,Structure164,Structure165,Structure166,Structure167,+8 more]
  Height = 0
  HeightPropagate = true
  IfcData = attributes={"GlobalId": {"name": "GlobalId", "type": "IfcGloballyUniqueId", "is_enum": false, "enum_values": []}, "Description": {"... (+484 chars omitted),+1 more (map truncated)
  IfcType = 172
  LevelOffset = 0
  PredefinedType = 0
FEATURE [Part::FeaturePython] Structure226  label="L121"  # Arch/BIM 172 (typed FeaturePython)
  Base = -> Rectangle014
  FaceMaker = 0
  Height = 150
  HorizontalArea = 3928500
  IfcData = attributes={"GlobalId": {"name": "GlobalId", "type": "IfcGloballyUniqueId", "is_enum": false, "enum_values": []}, "Description": {"... (+484 chars omitted),+1 more (map truncated)
  IfcType = 172
  Length = 0
  MoveBase = false
  MoveWithHost = false
  Nodes = (2) [(7585,9097.5,3000),(7585,9097.5,2850)]
  NodesOffset = 0
  Normal = (0,0,-1)
  PerimeterLength = 8310
  Placement = pos=(0,0,3000) rot=(0,0,1;0rad)
  PredefinedType = 0
  VerticalArea = 1246500
  Width = 150
FEATURE [Part::FeaturePython] Structure227  label="L122"  # Arch/BIM 172 (typed FeaturePython)
  Base = -> Wire
  FaceMaker = 0
  Height = 150
  HorizontalArea = 3.9285e+06
  IfcData = attributes={"GlobalId": {"name": "GlobalId", "type": "IfcGloballyUniqueId", "is_enum": false, "enum_values": []}, "Description": {"... (+484 chars omitted),+1 more (map truncated)
  IfcType = 172
  Length = 0
  MoveBase = false
  MoveWithHost = false
  Nodes = (2) [(7543.76,7449.37,3000),(7543.76,7449.37,2850)]
  NodesOffset = 0
  Normal = (0,0,-1)
  PerimeterLength = 8410
  Placement = pos=(0,0,2850) rot=(0,0,1;0rad)
  PredefinedType = 0
  VerticalArea = 1261500
  Width = 150
FEATURE [Part::FeaturePython] Structure228  label="L123"  # Arch/BIM 172 (typed FeaturePython)
  Base = -> Wire001
  FaceMaker = 0
  Height = 150
  HorizontalArea = 3.90134e+06
  IfcData = attributes={"GlobalId": {"name": "GlobalId", "type": "IfcGloballyUniqueId", "is_enum": false, "enum_values": []}, "Description": {"... (+484 chars omitted),+1 more (map truncated)
  IfcType = 172
  Length = 0
  MoveBase = false
  MoveWithHost = false
  Nodes = (2) [(7543.46,5835.61,3000),(7543.46,5835.61,2850)]
  NodesOffset = 0
  Normal = (0,0,-1)
  PerimeterLength = 8389.89
  Placement = pos=(0,0,2850) rot=(0,0,1;0rad)
  PredefinedType = 0
  VerticalArea = 1.25848e+06
  Width = 150
FEATURE [Part::FeaturePython] Structure229  label="L124"  # Arch/BIM 172 (typed FeaturePython)
  Base = -> Rectangle015
  FaceMaker = 0
  Height = 150
  HorizontalArea = 4.0365e+06
  IfcData = attributes={"GlobalId": {"name": "GlobalId", "type": "IfcGloballyUniqueId", "is_enum": false, "enum_values": []}, "Description": {"... (+484 chars omitted),+1 more (map truncated)
  IfcType = 172
  Length = 0
  MoveBase = false
  MoveWithHost = false
  Nodes = (2) [(7585,4172.5,3000),(7585,4172.5,2850)]
  NodesOffset = 0
  Normal = (0,0,-1)
  PerimeterLength = 8390
  Placement = pos=(0,0,3000) rot=(0,0,1;0rad)
  PredefinedType = 0
  VerticalArea = 1258500
  Width = 150
FEATURE [Part::FeaturePython] Structure230  label="L125"  # Arch/BIM 172 (typed FeaturePython)
  Base = -> Wire002
  FaceMaker = 0
  Height = 150
  HorizontalArea = 3.91484e+06
  IfcData = attributes={"GlobalId": {"name": "GlobalId", "type": "IfcGloballyUniqueId", "is_enum": false, "enum_values": []}, "Description": {"... (+484 chars omitted),+1 more (map truncated)
  IfcType = 172
  Length = 0
  MoveBase = false
  MoveWithHost = false
  Nodes = (2) [(7543.6,2543.13,3000),(7543.6,2543.13,2850)]
  NodesOffset = 0
  Normal = (0,0,-1)
  PerimeterLength = 8399.89
  Placement = pos=(0,0,2850) rot=(0,0,1;0rad)
  PredefinedType = 0
  VerticalArea = 1.25998e+06
  Width = 150
FEATURE [Part::FeaturePython] Structure231  label="L126"  # Arch/BIM 172 (typed FeaturePython)
  Base = -> Rectangle016
  FaceMaker = 0
  Height = 150
  HorizontalArea = 3.915e+06
  IfcData = attributes={"GlobalId": {"name": "GlobalId", "type": "IfcGloballyUniqueId", "is_enum": false, "enum_values": []}, "Description": {"... (+484 chars omitted),+1 more (map truncated)
  IfcType = 172
  Length = 0
  MoveBase = false
  MoveWithHost = false
  Nodes = (2) [(7585,900,3000),(7585,900,2850)]
  NodesOffset = 0
  Normal = (0,0,-1)
  PerimeterLength = 8300
  Placement = pos=(0,0,3000) rot=(0,0,1;0rad)
  PredefinedType = 0
  VerticalArea = 1.245e+06
  Width = 150
FEATURE [Part::FeaturePython] Structure232  label="L127"  # Arch/BIM 172 (typed FeaturePython)
  Base = -> Rectangle008
  FaceMaker = 0
  Height = 150
  HorizontalArea = 4354000
  IfcData = attributes={"GlobalId": {"name": "GlobalId", "type": "IfcGloballyUniqueId", "is_enum": false, "enum_values": []}, "Description": {"... (+484 chars omitted),+1 more (map truncated)
  IfcType = 172
  Length = 0
  MoveBase = false
  MoveWithHost = false
  Nodes = (2) [(9785,8270,3000),(9785,8270,2850)]
  NodesOffset = 0
  Normal = (0,0,-1)
  PerimeterLength = 9020
  Placement = pos=(0,0,3000) rot=(0,0,1;0rad)
  PredefinedType = 0
  VerticalArea = 1353000
  Width = 150
FEATURE [Part::FeaturePython] Structure233  label="L128"  # Arch/BIM 172 (typed FeaturePython)
  Base = -> Rectangle011
  FaceMaker = 0
  Height = 150
  HorizontalArea = 4396000
  IfcData = attributes={"GlobalId": {"name": "GlobalId", "type": "IfcGloballyUniqueId", "is_enum": false, "enum_values": []}, "Description": {"... (+484 chars omitted),+1 more (map truncated)
  IfcType = 172
  Length = 0
  MoveBase = false
  MoveWithHost = false
  Nodes = (2) [(9785,4995,3000),(9785,4995,2850)]
  NodesOffset = 0
  Normal = (0,0,-1)
  PerimeterLength = 9080
  Placement = pos=(0,0,3000) rot=(0,0,1;0rad)
  PredefinedType = 0
  VerticalArea = 1362000
  Width = 150
FEATURE [Part::FeaturePython] Structure234  label="L129"  # Arch/BIM 172 (typed FeaturePython)
  Base = -> Rectangle013
  FaceMaker = 0
  Height = 150
  HorizontalArea = 4.34e+06
  IfcData = attributes={"GlobalId": {"name": "GlobalId", "type": "IfcGloballyUniqueId", "is_enum": false, "enum_values": []}, "Description": {"... (+484 chars omitted),+1 more (map truncated)
  IfcType = 172
  Length = 0
  MoveBase = false
  MoveWithHost = false
  Nodes = (2) [(9785,1725,3000),(9785,1725,2850)]
  NodesOffset = 0
  Normal = (0,0,-1)
  PerimeterLength = 9000
  Placement = pos=(0,0,3000) rot=(0,0,1;0rad)
  PredefinedType = 0
  VerticalArea = 1350000
  Width = 150
FEATURE [Part::FeaturePython] Structure235  label="L130"  # Arch/BIM 172 (typed FeaturePython)
  Base = -> Rectangle009
  FaceMaker = 0
  Height = 150
  HorizontalArea = 1.794e+06
  IfcData = attributes={"GlobalId": {"name": "GlobalId", "type": "IfcGloballyUniqueId", "is_enum": false, "enum_values": []}, "Description": {"... (+484 chars omitted),+1 more (map truncated)
  IfcType = 172
  Length = 0
  MoveBase = false
  MoveWithHost = false
  Nodes = (2) [(11285,9135,3000),(11285,9135,2850)]
  NodesOffset = 0
  Normal = (0,0,-1)
  PerimeterLength = 5360
  Placement = pos=(0,0,3000) rot=(0,0,1;0rad)
  PredefinedType = 0
  VerticalArea = 804000
  Width = 150
FEATURE [Part::FeaturePython] Structure236  label="L131"  # Arch/BIM 172 (typed FeaturePython)
  Base = -> Rectangle018
  FaceMaker = 0
  Height = 150
  HorizontalArea = 3.211e+06
  IfcData = attributes={"GlobalId": {"name": "GlobalId", "type": "IfcGloballyUniqueId", "is_enum": false, "enum_values": []}, "Description": {"... (+484 chars omitted),+1 more (map truncated)
  IfcType = 172
  Length = 0
  MoveBase = false
  MoveWithHost = false
  Nodes = (2) [(11285,4660,3000),(11285,4660,2850)]
  NodesOffset = 0
  Normal = (0,0,-1)
  PerimeterLength = 7540
  Placement = pos=(0,0,3000) rot=(0,0,1;0rad)
  PredefinedType = 0
  VerticalArea = 1.131e+06
  Width = 150
FEATURE [Part::FeaturePython] Structure237  label="L132"  # Arch/BIM 172 (typed FeaturePython)
  Base = -> Rectangle020
  FaceMaker = 0
  Height = 150
  HorizontalArea = 9439500
  IfcData = attributes={"GlobalId": {"name": "GlobalId", "type": "IfcGloballyUniqueId", "is_enum": false, "enum_values": []}, "Description": {"... (+484 chars omitted),+1 more (map truncated)
  IfcType = 172
  Length = 0
  MoveBase = false
  MoveWithHost = false
  Nodes = (2) [(12157.5,1725,3000),(12157.5,1725,2850)]
  NodesOffset = 0
  Normal = (0,0,-1)
  PerimeterLength = 12290
  Placement = pos=(0,0,3000) rot=(0,0,1;0rad)
  PredefinedType = 0
  VerticalArea = 1843500
  Width = 150
FEATURE [Part::FeaturePython] Structure238  label="L133"  # Arch/BIM 172 (typed FeaturePython)
  Base = -> Rectangle019
  FaceMaker = 0
  Height = 150
  HorizontalArea = 3.93965e+06
  IfcData = attributes={"GlobalId": {"name": "GlobalId", "type": "IfcGloballyUniqueId", "is_enum": false, "enum_values": []}, "Description": {"... (+484 chars omitted),+1 more (map truncated)
  IfcType = 172
  Length = 0
  MoveBase = false
  MoveWithHost = false
  Nodes = (2) [(12882.5,4660,3000),(12882.5,4660,2850)]
  NodesOffset = 0
  Normal = (0,0,-1)
  PerimeterLength = 8130
  Placement = pos=(0,0,2850) rot=(0,0,1;0rad)
  PredefinedType = 0
  VerticalArea = 1.2195e+06
  Width = 150
FEATURE [Part::FeaturePython] Structure239  label="L134"  # Arch/BIM 172 (typed FeaturePython)
  Base = -> Rectangle017
  FaceMaker = 0
  Height = 150
  HorizontalArea = 4174500
  IfcData = attributes={"GlobalId": {"name": "GlobalId", "type": "IfcGloballyUniqueId", "is_enum": false, "enum_values": []}, "Description": {"... (+484 chars omitted),+1 more (map truncated)
  IfcType = 172
  Length = 0
  MoveBase = false
  MoveWithHost = false
  Nodes = (2) [(13597.5,9135,3000),(13597.5,9135,2850)]
  NodesOffset = 0
  Normal = (0,0,-1)
  PerimeterLength = 8810
  Placement = pos=(0,0,3000) rot=(0,0,1;0rad)
  PredefinedType = 0
  VerticalArea = 1321500
  Width = 150
FEATURE [App::GeometryPython] BuildingPart015  label="Losas sobre P1"  # Arch/BIM 172 (typed FeaturePython)
  Area = 0
  Group = -> [Structure219,Structure220,Structure221,Structure226,Structure227,Structure228,Structure229,Structure230,Structure231,Structure232,Structure233,Structure234,Structure235,Structure236,Structure237,Structure238,Structure239]
  Height = 0
  HeightPropagate = true
  IfcData = attributes={"GlobalId": {"name": "GlobalId", "type": "IfcGloballyUniqueId", "is_enum": false, "enum_values": []}, "Description": {"... (+484 chars omitted),+1 more (map truncated)
  IfcType = 172
  LevelOffset = 0
  PredefinedType = 0
FEATURE [App::GeometryPython] BuildingPart003  label="Piso 1"  # Arch/BIM 172 (typed FeaturePython)
  Area = 24900000
  Group = -> [BuildingPart012,BuildingPart015,Wall002,BuildingPart011]
  Height = 0
  HeightPropagate = true
  IfcData = attributes={"GlobalId": {"name": "GlobalId", "type": "IfcGloballyUniqueId", "is_enum": false, "enum_values": []}, "Description": {"... (+484 chars omitted),+1 more (map truncated)
  IfcType = 172
  LevelOffset = 0
  Placement = pos=(0,0,3000) rot=(0,0,1;0rad)
  PredefinedType = 0
FEATURE [Part::FeaturePython] Structure240  label="25x15 C045"  # Arch/BIM 24 (typed FeaturePython)
  FaceMaker = 0
  Height = 3000
  HorizontalArea = 37500
  IfcData = attributes={"GlobalId": {"name": "GlobalId", "type": "IfcGloballyUniqueId", "is_enum": false, "enum_values": []}, "Description": {"... (+438 chars omitted),+1 more (map truncated)
  IfcType = 24
  Length = 250
  MoveBase = false
  MoveWithHost = false
  Nodes = (2) [(-1.05471e-15,1.36424e-15,0),(-1.05471e-15,1.36424e-15,3000)]
  NodesOffset = 0
  Normal = (0,0,0)
  PerimeterLength = 800
  Placement = pos=(1930,9900,6000) rot=(0,0,1;0rad)
  PredefinedType = 0
  VerticalArea = 2400000
  Width = 150
FEATURE [Part::FeaturePython] Structure241  label="25x15 C046"  # Arch/BIM 172 (typed FeaturePython)
  FaceMaker = 0
  Height = 3000
  HorizontalArea = 37500
  IfcData = attributes={"GlobalId": {"name": "GlobalId", "type": "IfcGloballyUniqueId", "is_enum": false, "enum_values": []}, "Description": {"... (+484 chars omitted),+1 more (map truncated)
  IfcType = 172
  Length = 250
  MoveBase = false
  MoveWithHost = false
  Nodes = (2) [(-1.05471e-15,1.36424e-15,0),(-1.05471e-15,1.36424e-15,3000)]
  NodesOffset = 0
  Normal = (0,0,0)
  PerimeterLength = 800
  Placement = pos=(1930,100,6000) rot=(0,0,1;0rad)
  PredefinedType = 0
  VerticalArea = 2400000
  Width = 150
FEATURE [Part::FeaturePython] Structure242  label="25x20 C010"  # Arch/BIM 24 (typed FeaturePython)
  FaceMaker = 0
  Height = 3000
  HorizontalArea = 50000
  IfcData = attributes={"GlobalId": {"name": "GlobalId", "type": "IfcGloballyUniqueId", "is_enum": false, "enum_values": []}, "Description": {"... (+438 chars omitted),+1 more (map truncated)
  IfcType = 24
  Length = 250
  MoveBase = false
  MoveWithHost = false
  Nodes = (2) [(-1.05471e-15,-1.81899e-15,0),(-1.05471e-15,-1.81899e-15,3000)]
  NodesOffset = 0
  Normal = (0,0,0)
  PerimeterLength = 900
  Placement = pos=(1930,6640,6000) rot=(0,0,1;0rad)
  PredefinedType = 0
  VerticalArea = 2700000
  Width = 200
FEATURE [Part::FeaturePython] Structure243  label="25x20 C011"  # Arch/BIM 172 (typed FeaturePython)
  FaceMaker = 0
  Height = 3000
  HorizontalArea = 50000
  IfcData = attributes={"GlobalId": {"name": "GlobalId", "type": "IfcGloballyUniqueId", "is_enum": false, "enum_values": []}, "Description": {"... (+484 chars omitted),+1 more (map truncated)
  IfcType = 172
  Length = 250
  MoveBase = false
  MoveWithHost = false
  Nodes = (2) [(-1.05471e-15,-1.81899e-15,0),(-1.05471e-15,-1.81899e-15,3000)]
  NodesOffset = 0
  Normal = (0,0,0)
  PerimeterLength = 900
  Placement = pos=(1930,3350,6000) rot=(0,0,1;0rad)
  PredefinedType = 0
  VerticalArea = 2700000
  Width = 200
FEATURE [Part::FeaturePython] Structure244  label="25x15 C047"  # Arch/BIM 24 (typed FeaturePython)
  FaceMaker = 0
  Height = 3000
  HorizontalArea = 37500
  IfcData = attributes={"GlobalId": {"name": "GlobalId", "type": "IfcGloballyUniqueId", "is_enum": false, "enum_values": []}, "Description": {"... (+438 chars omitted),+1 more (map truncated)
  IfcType = 24
  Length = 250
  MoveBase = false
  MoveWithHost = false
  Nodes = (2) [(-1.05471e-15,1.36424e-15,0),(-1.05471e-15,1.36424e-15,3000)]
  NodesOffset = 0
  Normal = (0,0,0)
  PerimeterLength = 800
  Placement = pos=(6160,6640,6000) rot=(0,0,1;0rad)
  PredefinedType = 0
  VerticalArea = 2400000
  Width = 150
FEATURE [Part::FeaturePython] Structure245  label="25x15 C048"  # Arch/BIM 24 (typed FeaturePython)
  FaceMaker = 0
  Height = 3000
  HorizontalArea = 37500
  IfcData = attributes={"GlobalId": {"name": "GlobalId", "type": "IfcGloballyUniqueId", "is_enum": false, "enum_values": []}, "Description": {"... (+438 chars omitted),+1 more (map truncated)
  IfcType = 24
  Length = 250
  MoveBase = false
  MoveWithHost = false
  Nodes = (2) [(-1.05471e-15,1.36424e-15,0),(-1.05471e-15,1.36424e-15,3000)]
  NodesOffset = 0
  Normal = (0,0,0)
  PerimeterLength = 800
  Placement = pos=(6160,3350,6000) rot=(0,0,1;0rad)
  PredefinedType = 0
  VerticalArea = 2400000
  Width = 150
FEATURE [Part::FeaturePython] Structure246  label="25x15 C049"  # Arch/BIM 24 (typed FeaturePython)
  FaceMaker = 0
  Height = 3000
  HorizontalArea = 37500
  IfcData = attributes={"GlobalId": {"name": "GlobalId", "type": "IfcGloballyUniqueId", "is_enum": false, "enum_values": []}, "Description": {"... (+438 chars omitted),+1 more (map truncated)
  IfcType = 24
  Length = 250
  MoveBase = false
  MoveWithHost = false
  Nodes = (2) [(-1.05471e-15,1.36424e-15,0),(-1.05471e-15,1.36424e-15,3000)]
  NodesOffset = 0
  Normal = (0,0,0)
  PerimeterLength = 800
  Placement = pos=(6160,100,6000) rot=(0,0,1;0rad)
  PredefinedType = 0
  VerticalArea = 2400000
  Width = 150
FEATURE [Part::FeaturePython] Structure247  label="25x15 C050"  # Arch/BIM 24 (typed FeaturePython)
  FaceMaker = 0
  Height = 3000
  HorizontalArea = 37500
  IfcData = attributes={"GlobalId": {"name": "GlobalId", "type": "IfcGloballyUniqueId", "is_enum": false, "enum_values": []}, "Description": {"... (+438 chars omitted),+1 more (map truncated)
  IfcType = 24
  Length = 250
  MoveBase = false
  MoveWithHost = false
  Nodes = (2) [(-1.05471e-15,1.36424e-15,0),(-1.05471e-15,1.36424e-15,3000)]
  NodesOffset = 0
  Normal = (0,0,0)
  PerimeterLength = 800
  Placement = pos=(9010,100,6000) rot=(0,0,1;0rad)
  PredefinedType = 0
  VerticalArea = 2400000
  Width = 150
FEATURE [Part::FeaturePython] Structure248  label="25x15 C051"  # Arch/BIM 24 (typed FeaturePython)
  FaceMaker = 0
  Height = 3000
  HorizontalArea = 37500
  IfcData = attributes={"GlobalId": {"name": "GlobalId", "type": "IfcGloballyUniqueId", "is_enum": false, "enum_values": []}, "Description": {"... (+438 chars omitted),+1 more (map truncated)
  IfcType = 24
  Length = 250
  MoveBase = false
  MoveWithHost = false
  Nodes = (2) [(-1.05471e-15,1.36424e-15,0),(-1.05471e-15,1.36424e-15,3000)]
  NodesOffset = 0
  Normal = (0,0,0)
  PerimeterLength = 800
  Placement = pos=(10560,100,6000) rot=(0,0,1;0rad)
  PredefinedType = 0
  VerticalArea = 2400000
  Width = 150
FEATURE [Part::FeaturePython] Structure249  label="25x15 C052"  # Arch/BIM 24 (typed FeaturePython)
  FaceMaker = 0
  Height = 3000
  HorizontalArea = 37500
  IfcData = attributes={"GlobalId": {"name": "GlobalId", "type": "IfcGloballyUniqueId", "is_enum": false, "enum_values": []}, "Description": {"... (+438 chars omitted),+1 more (map truncated)
  IfcType = 24
  Length = 250
  MoveBase = false
  MoveWithHost = false
  Nodes = (2) [(-1.05471e-15,1.36424e-15,0),(-1.05471e-15,1.36424e-15,3000)]
  NodesOffset = 0
  Normal = (0,0,0)
  PerimeterLength = 800
  Placement = pos=(13780,100,6000) rot=(0,0,1;0rad)
  PredefinedType = 0
  VerticalArea = 2400000
  Width = 150
FEATURE [Part::FeaturePython] Structure250  label="25x15 C053"  # Arch/BIM 24 (typed FeaturePython)
  FaceMaker = 0
  Height = 3000
  HorizontalArea = 37500
  IfcData = attributes={"GlobalId": {"name": "GlobalId", "type": "IfcGloballyUniqueId", "is_enum": false, "enum_values": []}, "Description": {"... (+438 chars omitted),+1 more (map truncated)
  IfcType = 24
  Length = 250
  MoveBase = false
  MoveWithHost = false
  Nodes = (2) [(-1.05471e-15,1.36424e-15,0),(-1.05471e-15,1.36424e-15,3000)]
  NodesOffset = 0
  Normal = (0,0,0)
  PerimeterLength = 800
  Placement = pos=(15210,5970,6000) rot=(0,0,1;0rad)
  PredefinedType = 0
  VerticalArea = 2400000
  Width = 150
FEATURE [Part::FeaturePython] Structure251  label="25x15 C054"  # Arch/BIM 24 (typed FeaturePython)
  FaceMaker = 0
  Height = 3000
  HorizontalArea = 37500
  IfcData = attributes={"GlobalId": {"name": "GlobalId", "type": "IfcGloballyUniqueId", "is_enum": false, "enum_values": []}, "Description": {"... (+438 chars omitted),+1 more (map truncated)
  IfcType = 24
  Length = 250
  MoveBase = false
  MoveWithHost = false
  Nodes = (2) [(-1.05471e-15,1.36424e-15,0),(-1.05471e-15,1.36424e-15,3000)]
  NodesOffset = 0
  Normal = (0,0,0)
  PerimeterLength = 800
  Placement = pos=(13780,5970,6000) rot=(0,0,1;0rad)
  PredefinedType = 0
  VerticalArea = 2400000
  Width = 150
FEATURE [Part::FeaturePython] Structure252  label="25x15 C055"  # Arch/BIM 172 (typed FeaturePython)
  FaceMaker = 0
  Height = 3000
  HorizontalArea = 37500
  IfcData = attributes={"GlobalId": {"name": "GlobalId", "type": "IfcGloballyUniqueId", "is_enum": false, "enum_values": []}, "Description": {"... (+484 chars omitted),+1 more (map truncated)
  IfcType = 172
  Length = 250
  MoveBase = false
  MoveWithHost = false
  Nodes = (2) [(-1.05471e-15,1.36424e-15,0),(-1.05471e-15,1.36424e-15,3000)]
  NodesOffset = 0
  Normal = (0,0,0)
  PerimeterLength = 800
  Placement = pos=(1930,9900,6000) rot=(0,0,1;0rad)
  PredefinedType = 0
  VerticalArea = 2400000
  Width = 150
FEATURE [Part::FeaturePython] Structure253  label="25x15 C056"  # Arch/BIM 172 (typed FeaturePython)
  FaceMaker = 0
  Height = 3000
  HorizontalArea = 37500
  IfcData = attributes={"GlobalId": {"name": "GlobalId", "type": "IfcGloballyUniqueId", "is_enum": false, "enum_values": []}, "Description": {"... (+484 chars omitted),+1 more (map truncated)
  IfcType = 172
  Length = 250
  MoveBase = false
  MoveWithHost = false
  Nodes = (2) [(-1.05471e-15,1.36424e-15,0),(-1.05471e-15,1.36424e-15,3000)]
  NodesOffset = 0
  Normal = (0,0,0)
  PerimeterLength = 800
  Placement = pos=(9010,6640,6000) rot=(0,0,1;1.5708rad)
  PredefinedType = 0
  VerticalArea = 2400000
  Width = 150
FEATURE [Part::FeaturePython] Structure254  label="25x15 C057"  # Arch/BIM 172 (typed FeaturePython)
  FaceMaker = 0
  Height = 3000
  HorizontalArea = 37500
  IfcData = attributes={"GlobalId": {"name": "GlobalId", "type": "IfcGloballyUniqueId", "is_enum": false, "enum_values": []}, "Description": {"... (+484 chars omitted),+1 more (map truncated)
  IfcType = 172
  Length = 250
  MoveBase = false
  MoveWithHost = false
  Nodes = (2) [(-1.05471e-15,1.36424e-15,0),(-1.05471e-15,1.36424e-15,3000)]
  NodesOffset = 0
  Normal = (0,0,0)
  PerimeterLength = 800
  Placement = pos=(9010,3350,6000) rot=(0,0,1;1.5708rad)
  PredefinedType = 0
  VerticalArea = 2400000
  Width = 150
FEATURE [Part::FeaturePython] Structure255  label="25x15 C058"  # Arch/BIM 172 (typed FeaturePython)
  FaceMaker = 0
  Height = 3000
  HorizontalArea = 37500
  IfcData = attributes={"GlobalId": {"name": "GlobalId", "type": "IfcGloballyUniqueId", "is_enum": false, "enum_values": []}, "Description": {"... (+484 chars omitted),+1 more (map truncated)
  IfcType = 172
  Length = 250
  MoveBase = false
  MoveWithHost = false
  Nodes = (2) [(-1.05471e-15,1.36424e-15,0),(-1.05471e-15,1.36424e-15,3000)]
  NodesOffset = 0
  Normal = (0,0,0)
  PerimeterLength = 800
  Placement = pos=(10560,3350,6000) rot=(0,0,1;1.5708rad)
  PredefinedType = 0
  VerticalArea = 2400000
  Width = 150
FEATURE [Part::FeaturePython] Structure256  label="25x15 C059"  # Arch/BIM 172 (typed FeaturePython)
  FaceMaker = 0
  Height = 3000
  HorizontalArea = 37500
  IfcData = attributes={"GlobalId": {"name": "GlobalId", "type": "IfcGloballyUniqueId", "is_enum": false, "enum_values": []}, "Description": {"... (+484 chars omitted),+1 more (map truncated)
  IfcType = 172
  Length = 250
  MoveBase = false
  MoveWithHost = false
  Nodes = (2) [(-1.05471e-15,1.36424e-15,0),(-1.05471e-15,1.36424e-15,3000)]
  NodesOffset = 0
  Normal = (0,0,0)
  PerimeterLength = 800
  Placement = pos=(13780,3350,6000) rot=(0,0,1;1.5708rad)
  PredefinedType = 0
  VerticalArea = 2400000
  Width = 150
FEATURE [Part::FeaturePython] Structure257  label="25x15 C060"  # Arch/BIM 172 (typed FeaturePython)
  FaceMaker = 0
  Height = 3000
  HorizontalArea = 37500
  IfcData = attributes={"GlobalId": {"name": "GlobalId", "type": "IfcGloballyUniqueId", "is_enum": false, "enum_values": []}, "Description": {"... (+484 chars omitted),+1 more (map truncated)
  IfcType = 172
  Length = 250
  MoveBase = false
  MoveWithHost = false
  Nodes = (2) [(-1.05471e-15,1.36424e-15,0),(-1.05471e-15,1.36424e-15,3000)]
  NodesOffset = 0
  Normal = (0,0,0)
  PerimeterLength = 800
  Placement = pos=(9010,9900,6000) rot=(0,0,1;0rad)
  PredefinedType = 0
  VerticalArea = 2400000
  Width = 150
FEATURE [Part::FeaturePython] Structure258  label="25x15 C061"  # Arch/BIM 172 (typed FeaturePython)
  FaceMaker = 0
  Height = 3000
  HorizontalArea = 37500
  IfcData = attributes={"GlobalId": {"name": "GlobalId", "type": "IfcGloballyUniqueId", "is_enum": false, "enum_values": []}, "Description": {"... (+484 chars omitted),+1 more (map truncated)
  IfcType = 172
  Length = 250
  MoveBase = false
  MoveWithHost = false
  Nodes = (2) [(-1.05471e-15,1.36424e-15,0),(-1.05471e-15,1.36424e-15,3000)]
  NodesOffset = 0
  Normal = (0,0,0)
  PerimeterLength = 800
  Placement = pos=(6160,9900,6000) rot=(0,0,1;0rad)
  PredefinedType = 0
  VerticalArea = 2400000
  Width = 150
FEATURE [Part::FeaturePython] Structure259  label="25x15 C062"  # Arch/BIM 172 (typed FeaturePython)
  FaceMaker = 0
  Height = 3000
  HorizontalArea = 37500
  IfcData = attributes={"GlobalId": {"name": "GlobalId", "type": "IfcGloballyUniqueId", "is_enum": false, "enum_values": []}, "Description": {"... (+484 chars omitted),+1 more (map truncated)
  IfcType = 172
  Length = 250
  MoveBase = false
  MoveWithHost = false
  Nodes = (2) [(-1.05471e-15,1.36424e-15,0),(-1.05471e-15,1.36424e-15,3000)]
  NodesOffset = 0
  Normal = (0,0,0)
  PerimeterLength = 800
  Placement = pos=(12010,9900,6000) rot=(0,0,1;0rad)
  PredefinedType = 0
  VerticalArea = 2400000
  Width = 150
FEATURE [Part::FeaturePython] Structure260  label="25x15 C063"  # Arch/BIM 172 (typed FeaturePython)
  FaceMaker = 0
  Height = 3000
  HorizontalArea = 37500
  IfcData = attributes={"GlobalId": {"name": "GlobalId", "type": "IfcGloballyUniqueId", "is_enum": false, "enum_values": []}, "Description": {"... (+484 chars omitted),+1 more (map truncated)
  IfcType = 172
  Length = 250
  MoveBase = false
  MoveWithHost = false
  Nodes = (2) [(-1.05471e-15,1.36424e-15,0),(-1.05471e-15,1.36424e-15,3000)]
  NodesOffset = 0
  Normal = (0,0,0)
  PerimeterLength = 800
  Placement = pos=(15210,9900,6000) rot=(0,0,1;0rad)
  PredefinedType = 0
  VerticalArea = 2400000
  Width = 150
FEATURE [App::GeometryPython] BuildingPart016  label="Columnas P2"  # Arch/BIM 172 (typed FeaturePython)
  Area = 0
  Group = -> [Structure240,Structure241,Structure244,Structure245,Structure246,Structure247,Structure248,Structure249,Structure250,Structure251,Structure252,Structure253,Structure254,Structure255,Structure256,Structure257,Structure258,Structure259,Structure260,Structure242,Structure243]
  Height = 0
  HeightPropagate = true
  IfcData = attributes={"GlobalId": {"name": "GlobalId", "type": "IfcGloballyUniqueId", "is_enum": false, "enum_values": []}, "Description": {"... (+484 chars omitted),+1 more (map truncated)
  IfcType = 172
  LevelOffset = 0
  PredefinedType = 0
FEATURE [Part::FeaturePython] Wall003  label="Tabique Ascensor P2"  # Arch/BIM 166 (typed FeaturePython)
  Align = 1
  Area = 24900000
  Base = -> Rectangle003
  BlockHeight = 0
  BlockLength = 0
  CountBroken = 0
  CountEntire = 0
  Face = 0
  Height = 3000
  HorizontalArea = 1155000
  IfcData = attributes={"GlobalId": {"name": "GlobalId", "type": "IfcGloballyUniqueId", "is_enum": false, "enum_values": []}, "Description": {"... (+533 chars omitted),+1 more (map truncated)
  IfcType = 166
  Joint = 0
  Length = 8300
  MakeBlocks = false
  MoveBase = false
  MoveWithHost = false
  Normal = (0,0,0)
  OffsetFirst = 0
  OffsetSecond = 0
  PerimeterLength = 8300
  Placement = pos=(0,0,6000) rot=(0,0,1;0rad)
  PredefinedType = 0
  VerticalArea = 46200000
  Width = 150
FEATURE [Part::FeaturePython] Structure261  label="V15x40 V161"  # Arch/BIM 7 (typed FeaturePython)
  FaceMaker = 0
  Height = 400
  HorizontalArea = 597000
  IfcData = attributes={"GlobalId": {"name": "GlobalId", "type": "IfcGloballyUniqueId", "is_enum": false, "enum_values": []}, "Description": {"... (+475 chars omitted),+1 more (map truncated)
  IfcType = 7
  Length = 3980
  MoveBase = false
  MoveWithHost = false
  Nodes = (2) [(-1.72563e-31,-1.42109e-15,-7.77156e-16),(3980,-1.42109e-15,-7.77156e-16)]
  NodesOffset = 0
  Normal = (0,0,0)
  PerimeterLength = 8260
  Placement = pos=(2055,9900,8800) rot=(0,0,1;0rad)
  PredefinedType = 0
  VerticalArea = 3.304e+06
  Width = 150
FEATURE [Part::FeaturePython] Structure262  label="V15x40 V162"  # Arch/BIM 7 (typed FeaturePython)
  FaceMaker = 0
  Height = 400
  HorizontalArea = 390000
  IfcData = attributes={"GlobalId": {"name": "GlobalId", "type": "IfcGloballyUniqueId", "is_enum": false, "enum_values": []}, "Description": {"... (+475 chars omitted),+1 more (map truncated)
  IfcType = 7
  Length = 2600
  MoveBase = false
  MoveWithHost = false
  Nodes = (2) [(-1.72563e-31,-1.42109e-15,-7.77156e-16),(2600,-1.42109e-15,-7.77156e-16)]
  NodesOffset = 0
  Normal = (0,0,0)
  PerimeterLength = 5500
  Placement = pos=(6285,9900,8800) rot=(0,0,1;0rad)
  PredefinedType = 0
  VerticalArea = 2200000
  Width = 150
FEATURE [Part::FeaturePython] Structure263  label="V15x40 V163"  # Arch/BIM 7 (typed FeaturePython)
  FaceMaker = 0
  Height = 400
  HorizontalArea = 412500
  IfcData = attributes={"GlobalId": {"name": "GlobalId", "type": "IfcGloballyUniqueId", "is_enum": false, "enum_values": []}, "Description": {"... (+475 chars omitted),+1 more (map truncated)
  IfcType = 7
  Length = 2750
  MoveBase = false
  MoveWithHost = false
  Nodes = (2) [(-1.72563e-31,-1.42109e-15,-7.77156e-16),(2750,-1.42109e-15,-7.77156e-16)]
  NodesOffset = 0
  Normal = (0,0,0)
  PerimeterLength = 5800
  Placement = pos=(9135,9900,8800) rot=(0,0,1;0rad)
  PredefinedType = 0
  VerticalArea = 2320000
  Width = 150
FEATURE [Part::FeaturePython] Structure264  label="V15x40 V164"  # Arch/BIM 7 (typed FeaturePython)
  FaceMaker = 0
  Height = 400
  HorizontalArea = 442500
  IfcData = attributes={"GlobalId": {"name": "GlobalId", "type": "IfcGloballyUniqueId", "is_enum": false, "enum_values": []}, "Description": {"... (+475 chars omitted),+1 more (map truncated)
  IfcType = 7
  Length = 2950
  MoveBase = false
  MoveWithHost = false
  Nodes = (2) [(-1.72563e-31,-1.42109e-15,-7.77156e-16),(2950,-1.42109e-15,-7.77156e-16)]
  NodesOffset = 0
  Normal = (0,0,0)
  PerimeterLength = 6200
  Placement = pos=(12135,9900,8800) rot=(0,0,1;0rad)
  PredefinedType = 0
  VerticalArea = 2.48e+06
  Width = 150
FEATURE [Part::FeaturePython] Structure265  label="V15x40 V165"  # Arch/BIM 7 (typed FeaturePython)
  FaceMaker = 0
  Height = 400
  HorizontalArea = 453750
  IfcData = attributes={"GlobalId": {"name": "GlobalId", "type": "IfcGloballyUniqueId", "is_enum": false, "enum_values": []}, "Description": {"... (+475 chars omitted),+1 more (map truncated)
  IfcType = 7
  Length = 3025
  MoveBase = false
  MoveWithHost = false
  Nodes = (2) [(-1.72563e-31,-1.42109e-15,-7.77156e-16),(3025,-1.42109e-15,-7.77156e-16)]
  NodesOffset = 0
  Normal = (0,0,0)
  PerimeterLength = 6350
  Placement = pos=(12085,8370,8800) rot=(0,0,1;0rad)
  PredefinedType = 0
  VerticalArea = 2.54e+06
  Width = 150
FEATURE [Part::FeaturePython] Structure266  label="V15x40 V166"  # Arch/BIM 7 (typed FeaturePython)
  FaceMaker = 0
  Height = 400
  HorizontalArea = 597000
  IfcData = attributes={"GlobalId": {"name": "GlobalId", "type": "IfcGloballyUniqueId", "is_enum": false, "enum_values": []}, "Description": {"... (+475 chars omitted),+1 more (map truncated)
  IfcType = 7
  Length = 3980
  MoveBase = false
  MoveWithHost = false
  Nodes = (2) [(-1.72563e-31,-1.42109e-15,-7.77156e-16),(3980,-1.42109e-15,-7.77156e-16)]
  NodesOffset = 0
  Normal = (0,0,0)
  PerimeterLength = 8260
  Placement = pos=(2055,6640,8800) rot=(0,0,1;0rad)
  PredefinedType = 0
  VerticalArea = 3.304e+06
  Width = 150
FEATURE [Part::FeaturePython] Structure267  label="V15x40 V167"  # Arch/BIM 7 (typed FeaturePython)
  FaceMaker = 0
  Height = 400
  HorizontalArea = 397500
  IfcData = attributes={"GlobalId": {"name": "GlobalId", "type": "IfcGloballyUniqueId", "is_enum": false, "enum_values": []}, "Description": {"... (+475 chars omitted),+1 more (map truncated)
  IfcType = 7
  Length = 2650
  MoveBase = false
  MoveWithHost = false
  Nodes = (2) [(-1.72563e-31,-1.42109e-15,-7.77156e-16),(2650,-1.42109e-15,-7.77156e-16)]
  NodesOffset = 0
  Normal = (0,0,0)
  PerimeterLength = 5600
  Placement = pos=(6285,6640,8800) rot=(0,0,1;0rad)
  PredefinedType = 0
  VerticalArea = 2240000
  Width = 150
FEATURE [Part::FeaturePython] Structure268  label="V15x40 V168"  # Arch/BIM 7 (typed FeaturePython)
  FaceMaker = 0
  Height = 400
  HorizontalArea = 210000
  IfcData = attributes={"GlobalId": {"name": "GlobalId", "type": "IfcGloballyUniqueId", "is_enum": false, "enum_values": []}, "Description": {"... (+475 chars omitted),+1 more (map truncated)
  IfcType = 7
  Length = 1400
  MoveBase = false
  MoveWithHost = false
  Nodes = (2) [(-1.72563e-31,-1.42109e-15,-7.77156e-16),(1400,-1.42109e-15,-7.77156e-16)]
  NodesOffset = 0
  Normal = (0,0,0)
  PerimeterLength = 3100
  Placement = pos=(9085,6640,8800) rot=(0,0,1;0rad)
  PredefinedType = 0
  VerticalArea = 1240000
  Width = 150
FEATURE [Part::FeaturePython] Structure269  label="V15x40 V169"  # Arch/BIM 7 (typed FeaturePython)
  FaceMaker = 0
  Height = 400
  HorizontalArea = 235500
  IfcData = attributes={"GlobalId": {"name": "GlobalId", "type": "IfcGloballyUniqueId", "is_enum": false, "enum_values": []}, "Description": {"... (+475 chars omitted),+1 more (map truncated)
  IfcType = 7
  Length = 1570
  MoveBase = false
  MoveWithHost = false
  Nodes = (2) [(-1.72563e-31,-1.42109e-15,-7.77156e-16),(1570,-1.42109e-15,-7.77156e-16)]
  NodesOffset = 0
  Normal = (0,0,0)
  PerimeterLength = 3440
  Placement = pos=(13655,5970,8800) rot=(0,0,1;3.14159rad)
  PredefinedType = 0
  VerticalArea = 1.376e+06
  Width = 150
FEATURE [Part::FeaturePython] Structure270  label="V15x40 V170"  # Arch/BIM 7 (typed FeaturePython)
  FaceMaker = 0
  Height = 400
  HorizontalArea = 177000
  IfcData = attributes={"GlobalId": {"name": "GlobalId", "type": "IfcGloballyUniqueId", "is_enum": false, "enum_values": []}, "Description": {"... (+475 chars omitted),+1 more (map truncated)
  IfcType = 7
  Length = 1180
  MoveBase = false
  MoveWithHost = false
  Nodes = (2) [(-1.72563e-31,-1.42109e-15,-7.77156e-16),(1180,-1.42109e-15,-7.77156e-16)]
  NodesOffset = 0
  Normal = (0,0,0)
  PerimeterLength = 2660
  Placement = pos=(13905,5970,8800) rot=(0,0,1;0rad)
  PredefinedType = 0
  VerticalArea = 1064000
  Width = 150
FEATURE [Part::FeaturePython] Structure271  label="V15x40 V171"  # Arch/BIM 7 (typed FeaturePython)
  FaceMaker = 0
  Height = 400
  HorizontalArea = 597000
  IfcData = attributes={"GlobalId": {"name": "GlobalId", "type": "IfcGloballyUniqueId", "is_enum": false, "enum_values": []}, "Description": {"... (+475 chars omitted),+1 more (map truncated)
  IfcType = 7
  Length = 3980
  MoveBase = false
  MoveWithHost = false
  Nodes = (2) [(-1.72563e-31,-1.42109e-15,-7.77156e-16),(3980,-1.42109e-15,-7.77156e-16)]
  NodesOffset = 0
  Normal = (0,0,0)
  PerimeterLength = 8260
  Placement = pos=(2055,3350,8800) rot=(0,0,1;0rad)
  PredefinedType = 0
  VerticalArea = 3.304e+06
  Width = 150
FEATURE [Part::FeaturePython] Structure272  label="V15x40 V172"  # Arch/BIM 7 (typed FeaturePython)
  FaceMaker = 0
  Height = 400
  HorizontalArea = 397500
  IfcData = attributes={"GlobalId": {"name": "GlobalId", "type": "IfcGloballyUniqueId", "is_enum": false, "enum_values": []}, "Description": {"... (+475 chars omitted),+1 more (map truncated)
  IfcType = 7
  Length = 2650
  MoveBase = false
  MoveWithHost = false
  Nodes = (2) [(-1.72563e-31,-1.42109e-15,-7.77156e-16),(2650,-1.42109e-15,-7.77156e-16)]
  NodesOffset = 0
  Normal = (0,0,0)
  PerimeterLength = 5600
  Placement = pos=(6285,3350,8800) rot=(0,0,1;0rad)
  PredefinedType = 0
  VerticalArea = 2240000
  Width = 150
FEATURE [Part::FeaturePython] Structure273  label="V15x40 V173"  # Arch/BIM 7 (typed FeaturePython)
  FaceMaker = 0
  Height = 400
  HorizontalArea = 210000
  IfcData = attributes={"GlobalId": {"name": "GlobalId", "type": "IfcGloballyUniqueId", "is_enum": false, "enum_values": []}, "Description": {"... (+475 chars omitted),+1 more (map truncated)
  IfcType = 7
  Length = 1400
  MoveBase = false
  MoveWithHost = false
  Nodes = (2) [(-1.72563e-31,-1.42109e-15,-7.77156e-16),(1400,-1.42109e-15,-7.77156e-16)]
  NodesOffset = 0
  Normal = (0,0,0)
  PerimeterLength = 3100
  Placement = pos=(9085,3350,8800) rot=(0,0,1;0rad)
  PredefinedType = 0
  VerticalArea = 1240000
  Width = 150
FEATURE [Part::FeaturePython] Structure274  label="V15x40 V174"  # Arch/BIM 7 (typed FeaturePython)
  FaceMaker = 0
  Height = 400
  HorizontalArea = 460500
  IfcData = attributes={"GlobalId": {"name": "GlobalId", "type": "IfcGloballyUniqueId", "is_enum": false, "enum_values": []}, "Description": {"... (+475 chars omitted),+1 more (map truncated)
  IfcType = 7
  Length = 3070
  MoveBase = false
  MoveWithHost = false
  Nodes = (2) [(-1.72563e-31,-1.42109e-15,-7.77156e-16),(3070,-1.42109e-15,-7.77156e-16)]
  NodesOffset = 0
  Normal = (0,0,0)
  PerimeterLength = 6440
  Placement = pos=(10635,3350,8800) rot=(0,0,1;0rad)
  PredefinedType = 0
  VerticalArea = 2.576e+06
  Width = 150
FEATURE [Part::FeaturePython] Structure275  label="V15x40 V175"  # Arch/BIM 7 (typed FeaturePython)
  FaceMaker = 0
  Height = 400
  HorizontalArea = 597000
  IfcData = attributes={"GlobalId": {"name": "GlobalId", "type": "IfcGloballyUniqueId", "is_enum": false, "enum_values": []}, "Description": {"... (+475 chars omitted),+1 more (map truncated)
  IfcType = 7
  Length = 3980
  MoveBase = false
  MoveWithHost = false
  Nodes = (2) [(-1.72563e-31,-1.42109e-15,-7.77156e-16),(3980,-1.42109e-15,-7.77156e-16)]
  NodesOffset = 0
  Normal = (0,0,0)
  PerimeterLength = 8260
  Placement = pos=(2055,100,8800) rot=(0,0,1;0rad)
  PredefinedType = 0
  VerticalArea = 3.304e+06
  Width = 150
FEATURE [Part::FeaturePython] Structure276  label="V15x40 V176"  # Arch/BIM 7 (typed FeaturePython)
  FaceMaker = 0
  Height = 400
  HorizontalArea = 390000
  IfcData = attributes={"GlobalId": {"name": "GlobalId", "type": "IfcGloballyUniqueId", "is_enum": false, "enum_values": []}, "Description": {"... (+475 chars omitted),+1 more (map truncated)
  IfcType = 7
  Length = 2600
  MoveBase = false
  MoveWithHost = false
  Nodes = (2) [(-1.72563e-31,-1.42109e-15,-7.77156e-16),(2600,-1.42109e-15,-7.77156e-16)]
  NodesOffset = 0
  Normal = (0,0,0)
  PerimeterLength = 5500
  Placement = pos=(6285,100,8800) rot=(0,0,1;0rad)
  PredefinedType = 0
  VerticalArea = 2200000
  Width = 150
FEATURE [Part::FeaturePython] Structure277  label="V15x40 V177"  # Arch/BIM 7 (typed FeaturePython)
  FaceMaker = 0
  Height = 400
  HorizontalArea = 195000
  IfcData = attributes={"GlobalId": {"name": "GlobalId", "type": "IfcGloballyUniqueId", "is_enum": false, "enum_values": []}, "Description": {"... (+475 chars omitted),+1 more (map truncated)
  IfcType = 7
  Length = 1300
  MoveBase = false
  MoveWithHost = false
  Nodes = (2) [(-1.72563e-31,-1.42109e-15,-7.77156e-16),(1300,-1.42109e-15,-7.77156e-16)]
  NodesOffset = 0
  Normal = (0,0,0)
  PerimeterLength = 2900
  Placement = pos=(9135,100,8800) rot=(0,0,1;0rad)
  PredefinedType = 0
  VerticalArea = 1160000
  Width = 150
FEATURE [Part::FeaturePython] Structure278  label="V15x40 V178"  # Arch/BIM 7 (typed FeaturePython)
  FaceMaker = 0
  Height = 400
  HorizontalArea = 445500
  IfcData = attributes={"GlobalId": {"name": "GlobalId", "type": "IfcGloballyUniqueId", "is_enum": false, "enum_values": []}, "Description": {"... (+475 chars omitted),+1 more (map truncated)
  IfcType = 7
  Length = 2970
  MoveBase = false
  MoveWithHost = false
  Nodes = (2) [(-1.72563e-31,-1.42109e-15,-7.77156e-16),(2970,-1.42109e-15,-7.77156e-16)]
  NodesOffset = 0
  Normal = (0,0,0)
  PerimeterLength = 6240
  Placement = pos=(10685,100,8800) rot=(0,0,1;0rad)
  PredefinedType = 0
  VerticalArea = 2.496e+06
  Width = 150
FEATURE [Part::FeaturePython] Structure279  label="V15x40 V179"  # Arch/BIM 7 (typed FeaturePython)
  FaceMaker = 0
  Height = 400
  HorizontalArea = 465000
  IfcData = attributes={"GlobalId": {"name": "GlobalId", "type": "IfcGloballyUniqueId", "is_enum": false, "enum_values": []}, "Description": {"... (+475 chars omitted),+1 more (map truncated)
  IfcType = 7
  Length = 3100
  MoveBase = false
  MoveWithHost = false
  Nodes = (2) [(-1.72563e-31,-1.42109e-15,-7.77156e-16),(3100,-1.42109e-15,-7.77156e-16)]
  NodesOffset = 0
  Normal = (0,0,0)
  PerimeterLength = 6500
  Placement = pos=(6160,3275,8800) rot=(0,0,-1;1.5708rad)
  PredefinedType = 0
  VerticalArea = 2.6e+06
  Width = 150
FEATURE [Part::FeaturePython] Structure280  label="V15x40 V180"  # Arch/BIM 7 (typed FeaturePython)
  FaceMaker = 0
  Height = 400
  HorizontalArea = 471000
  IfcData = attributes={"GlobalId": {"name": "GlobalId", "type": "IfcGloballyUniqueId", "is_enum": false, "enum_values": []}, "Description": {"... (+475 chars omitted),+1 more (map truncated)
  IfcType = 7
  Length = 3140
  MoveBase = false
  MoveWithHost = false
  Nodes = (2) [(-1.72563e-31,-1.42109e-15,-7.77156e-16),(3140,-1.42109e-15,-7.77156e-16)]
  NodesOffset = 0
  Normal = (0,0,0)
  PerimeterLength = 6580
  Placement = pos=(6160,6565,8800) rot=(0,0,-1;1.5708rad)
  PredefinedType = 0
  VerticalArea = 2.632e+06
  Width = 150
FEATURE [Part::FeaturePython] Structure281  label="V15x40 V181"  # Arch/BIM 7 (typed FeaturePython)
  FaceMaker = 0
  Height = 400
  HorizontalArea = 466500
  IfcData = attributes={"GlobalId": {"name": "GlobalId", "type": "IfcGloballyUniqueId", "is_enum": false, "enum_values": []}, "Description": {"... (+475 chars omitted),+1 more (map truncated)
  IfcType = 7
  Length = 3110
  MoveBase = false
  MoveWithHost = false
  Nodes = (2) [(-1.72563e-31,-1.42109e-15,-7.77156e-16),(3110,-1.42109e-15,-7.77156e-16)]
  NodesOffset = 0
  Normal = (0,0,0)
  PerimeterLength = 6520
  Placement = pos=(6160,9825,8800) rot=(0,0,-1;1.5708rad)
  PredefinedType = 0
  VerticalArea = 2.608e+06
  Width = 150
FEATURE [Part::FeaturePython] Structure282  label="V15x40 V182"  # Arch/BIM 7 (typed FeaturePython)
  FaceMaker = 0
  Height = 400
  HorizontalArea = 457500
  IfcData = attributes={"GlobalId": {"name": "GlobalId", "type": "IfcGloballyUniqueId", "is_enum": false, "enum_values": []}, "Description": {"... (+475 chars omitted),+1 more (map truncated)
  IfcType = 7
  Length = 3050
  MoveBase = false
  MoveWithHost = false
  Nodes = (2) [(-1.72563e-31,-1.42109e-15,-7.77156e-16),(3050,-1.42109e-15,-7.77156e-16)]
  NodesOffset = 0
  Normal = (0,0,0)
  PerimeterLength = 6400
  Placement = pos=(9010,3225,8800) rot=(0,0,-1;1.5708rad)
  PredefinedType = 0
  VerticalArea = 2.56e+06
  Width = 150
FEATURE [Part::FeaturePython] Structure283  label="V15x40 V183"  # Arch/BIM 7 (typed FeaturePython)
  FaceMaker = 0
  Height = 400
  HorizontalArea = 456000
  IfcData = attributes={"GlobalId": {"name": "GlobalId", "type": "IfcGloballyUniqueId", "is_enum": false, "enum_values": []}, "Description": {"... (+475 chars omitted),+1 more (map truncated)
  IfcType = 7
  Length = 3040
  MoveBase = false
  MoveWithHost = false
  Nodes = (2) [(-1.72563e-31,-1.42109e-15,-7.77156e-16),(3040,-1.42109e-15,-7.77156e-16)]
  NodesOffset = 0
  Normal = (0,0,0)
  PerimeterLength = 6380
  Placement = pos=(9010,6515,8800) rot=(0,0,-1;1.5708rad)
  PredefinedType = 0
  VerticalArea = 2.552e+06
  Width = 150
FEATURE [Part::FeaturePython] Structure284  label="V15x40 V184"  # Arch/BIM 7 (typed FeaturePython)
  FaceMaker = 0
  Height = 400
  HorizontalArea = 459000
  IfcData = attributes={"GlobalId": {"name": "GlobalId", "type": "IfcGloballyUniqueId", "is_enum": false, "enum_values": []}, "Description": {"... (+475 chars omitted),+1 more (map truncated)
  IfcType = 7
  Length = 3060
  MoveBase = false
  MoveWithHost = false
  Nodes = (2) [(-1.72563e-31,-1.42109e-15,-7.77156e-16),(3060,-1.42109e-15,-7.77156e-16)]
  NodesOffset = 0
  Normal = (0,0,0)
  PerimeterLength = 6420
  Placement = pos=(9010,9825,8800) rot=(0,0,-1;1.5708rad)
  PredefinedType = 0
  VerticalArea = 2.568e+06
  Width = 150
FEATURE [Part::FeaturePython] Structure285  label="V15x40 V185"  # Arch/BIM 7 (typed FeaturePython)
  FaceMaker = 0
  Height = 400
  HorizontalArea = 457500
  IfcData = attributes={"GlobalId": {"name": "GlobalId", "type": "IfcGloballyUniqueId", "is_enum": false, "enum_values": []}, "Description": {"... (+475 chars omitted),+1 more (map truncated)
  IfcType = 7
  Length = 3050
  MoveBase = false
  MoveWithHost = false
  Nodes = (2) [(-1.72563e-31,-1.42109e-15,-7.77156e-16),(3050,-1.42109e-15,-7.77156e-16)]
  NodesOffset = 0
  Normal = (0,0,0)
  PerimeterLength = 6400
  Placement = pos=(10560,3225,8800) rot=(0,0,-1;1.5708rad)
  PredefinedType = 0
  VerticalArea = 2.56e+06
  Width = 150
FEATURE [Part::FeaturePython] Structure286  label="V15x40 V186"  # Arch/BIM 7 (typed FeaturePython)
  FaceMaker = 0
  Height = 400
  HorizontalArea = 363000
  IfcData = attributes={"GlobalId": {"name": "GlobalId", "type": "IfcGloballyUniqueId", "is_enum": false, "enum_values": []}, "Description": {"... (+475 chars omitted),+1 more (map truncated)
  IfcType = 7
  Length = 2420
  MoveBase = false
  MoveWithHost = false
  Nodes = (2) [(-1.72563e-31,-1.42109e-15,-7.77156e-16),(2420,-1.42109e-15,-7.77156e-16)]
  NodesOffset = 0
  Normal = (0,0,0)
  PerimeterLength = 5140
  Placement = pos=(10560,3475,8800) rot=(0,0,1;1.5708rad)
  PredefinedType = 0
  VerticalArea = 2056000
  Width = 150
FEATURE [Part::FeaturePython] Structure287  label="V15x40 V187"  # Arch/BIM 7 (typed FeaturePython)
  FaceMaker = 0
  Height = 400
  HorizontalArea = 207000
  IfcData = attributes={"GlobalId": {"name": "GlobalId", "type": "IfcGloballyUniqueId", "is_enum": false, "enum_values": []}, "Description": {"... (+475 chars omitted),+1 more (map truncated)
  IfcType = 7
  Length = 1380
  MoveBase = false
  MoveWithHost = false
  Nodes = (2) [(-1.72563e-31,-1.42109e-15,-7.77156e-16),(1380,-1.42109e-15,-7.77156e-16)]
  NodesOffset = 0
  Normal = (0,0,0)
  PerimeterLength = 3060
  Placement = pos=(10560,8445,8800) rot=(0,0,1;1.5708rad)
  PredefinedType = 0
  VerticalArea = 1224000
  Width = 150
FEATURE [Part::FeaturePython] Structure288  label="V15x40 V188"  # Arch/BIM 7 (typed FeaturePython)
  FaceMaker = 0
  Height = 400
  HorizontalArea = 207000
  IfcData = attributes={"GlobalId": {"name": "GlobalId", "type": "IfcGloballyUniqueId", "is_enum": false, "enum_values": []}, "Description": {"... (+475 chars omitted),+1 more (map truncated)
  IfcType = 7
  Length = 1380
  MoveBase = false
  MoveWithHost = false
  Nodes = (2) [(-1.72563e-31,-1.42109e-15,-7.77156e-16),(1380,-1.42109e-15,-7.77156e-16)]
  NodesOffset = 0
  Normal = (0,0,0)
  PerimeterLength = 3060
  Placement = pos=(12010,9825,8800) rot=(0,0,-1;1.5708rad)
  PredefinedType = 0
  VerticalArea = 1224000
  Width = 150
FEATURE [Part::FeaturePython] Structure289  label="V20x40 V142"  # Arch/BIM 7 (typed FeaturePython)
  FaceMaker = 0
  Height = 400
  HorizontalArea = 615000
  IfcData = attributes={"GlobalId": {"name": "GlobalId", "type": "IfcGloballyUniqueId", "is_enum": false, "enum_values": []}, "Description": {"... (+475 chars omitted),+1 more (map truncated)
  IfcType = 7
  Length = 3075
  MoveBase = false
  MoveWithHost = false
  Nodes = (2) [(-1.72563e-31,0,-7.77156e-16),(3075,0,-7.77156e-16)]
  NodesOffset = 0
  Normal = (0,0,0)
  PerimeterLength = 6550
  Placement = pos=(1930,3250,8800) rot=(0,0,-1;1.5708rad)
  PredefinedType = 0
  VerticalArea = 2.62e+06
  Width = 200
FEATURE [Part::FeaturePython] Structure290  label="V20x40 V143"  # Arch/BIM 7 (typed FeaturePython)
  FaceMaker = 0
  Height = 400
  HorizontalArea = 618000
  IfcData = attributes={"GlobalId": {"name": "GlobalId", "type": "IfcGloballyUniqueId", "is_enum": false, "enum_values": []}, "Description": {"... (+475 chars omitted),+1 more (map truncated)
  IfcType = 7
  Length = 3090
  MoveBase = false
  MoveWithHost = false
  Nodes = (2) [(-1.72563e-31,0,-7.77156e-16),(3090,0,-7.77156e-16)]
  NodesOffset = 0
  Normal = (0,0,0)
  PerimeterLength = 6580
  Placement = pos=(1930,6540,8800) rot=(0,0,-1;1.5708rad)
  PredefinedType = 0
  VerticalArea = 2.632e+06
  Width = 200
FEATURE [Part::FeaturePython] Structure291  label="V20x40 V144"  # Arch/BIM 7 (typed FeaturePython)
  FaceMaker = 0
  Height = 400
  HorizontalArea = 617000
  IfcData = attributes={"GlobalId": {"name": "GlobalId", "type": "IfcGloballyUniqueId", "is_enum": false, "enum_values": []}, "Description": {"... (+475 chars omitted),+1 more (map truncated)
  IfcType = 7
  Length = 3085
  MoveBase = false
  MoveWithHost = false
  Nodes = (2) [(-1.72563e-31,0,-7.77156e-16),(3085,0,-7.77156e-16)]
  NodesOffset = 0
  Normal = (0,0,0)
  PerimeterLength = 6570
  Placement = pos=(1930,9825,8800) rot=(0,0,-1;1.5708rad)
  PredefinedType = 0
  VerticalArea = 2.628e+06
  Width = 200
FEATURE [Part::FeaturePython] Structure292  label="V20x40 V145"  # Arch/BIM 7 (typed FeaturePython)
  FaceMaker = 0
  Height = 400
  HorizontalArea = 635000
  IfcData = attributes={"GlobalId": {"name": "GlobalId", "type": "IfcGloballyUniqueId", "is_enum": false, "enum_values": []}, "Description": {"... (+475 chars omitted),+1 more (map truncated)
  IfcType = 7
  Length = 3175
  MoveBase = false
  MoveWithHost = false
  Nodes = (2) [(-1.72563e-31,0,-7.77156e-16),(3175,0,-7.77156e-16)]
  NodesOffset = 0
  Normal = (0,0,0)
  PerimeterLength = 6750
  Placement = pos=(13780,175,8800) rot=(0,0,1;1.5708rad)
  PredefinedType = 0
  VerticalArea = 2.7e+06
  Width = 200
FEATURE [Part::FeaturePython] Structure293  label="V20x40 V146"  # Arch/BIM 7 (typed FeaturePython)
  FaceMaker = 0
  Height = 400
  HorizontalArea = 509000
  IfcData = attributes={"GlobalId": {"name": "GlobalId", "type": "IfcGloballyUniqueId", "is_enum": false, "enum_values": []}, "Description": {"... (+475 chars omitted),+1 more (map truncated)
  IfcType = 7
  Length = 2545
  MoveBase = false
  MoveWithHost = false
  Nodes = (2) [(-1.72563e-31,0,-7.77156e-16),(2545,0,-7.77156e-16)]
  NodesOffset = 0
  Normal = (0,0,0)
  PerimeterLength = 5490
  Placement = pos=(13780,3350,8800) rot=(0,0,1;1.5708rad)
  PredefinedType = 0
  VerticalArea = 2196000
  Width = 200
FEATURE [Part::FeaturePython] Structure294  label="V20x40 V147"  # Arch/BIM 7 (typed FeaturePython)
  FaceMaker = 0
  Height = 400
  HorizontalArea = 756000
  IfcData = attributes={"GlobalId": {"name": "GlobalId", "type": "IfcGloballyUniqueId", "is_enum": false, "enum_values": []}, "Description": {"... (+475 chars omitted),+1 more (map truncated)
  IfcType = 7
  Length = 3780
  MoveBase = false
  MoveWithHost = false
  Nodes = (2) [(-1.72563e-31,0,-7.77156e-16),(3780,0,-7.77156e-16)]
  NodesOffset = 0
  Normal = (0,0,0)
  PerimeterLength = 7960
  Placement = pos=(15210,6045,8800) rot=(0,0,1;1.5708rad)
  PredefinedType = 0
  VerticalArea = 3.184e+06
  Width = 200
FEATURE [Part::FeaturePython] Structure295  label="L135"  # Arch/BIM 172 (typed FeaturePython)
  Base = -> Rectangle004
  FaceMaker = 0
  Height = 150
  HorizontalArea = 12611050
  IfcData = attributes={"GlobalId": {"name": "GlobalId", "type": "IfcGloballyUniqueId", "is_enum": false, "enum_values": []}, "Description": {"... (+484 chars omitted),+1 more (map truncated)
  IfcType = 172
  Length = 0
  MoveBase = false
  MoveWithHost = false
  Nodes = (2) [(4057.5,8270,3000),(4057.5,8270,2850)]
  NodesOffset = 0
  Normal = (0,0,-1)
  PerimeterLength = 14330
  Placement = pos=(0,0,6000) rot=(0,0,1;0rad)
  PredefinedType = 0
  VerticalArea = 2149500
  Width = 150
FEATURE [Part::FeaturePython] Structure296  label="L136"  # Arch/BIM 172 (typed FeaturePython)
  Base = -> Rectangle005
  FaceMaker = 0
  Height = 150
  HorizontalArea = 12732700
  IfcData = attributes={"GlobalId": {"name": "GlobalId", "type": "IfcGloballyUniqueId", "is_enum": false, "enum_values": []}, "Description": {"... (+484 chars omitted),+1 more (map truncated)
  IfcType = 172
  Length = 0
  MoveBase = false
  MoveWithHost = false
  Nodes = (2) [(4057.5,4995,3000),(4057.5,4995,2850)]
  NodesOffset = 0
  Normal = (0,0,-1)
  PerimeterLength = 14390
  Placement = pos=(0,0,6000) rot=(0,0,1;0rad)
  PredefinedType = 0
  VerticalArea = 2158500
  Width = 150
FEATURE [Part::FeaturePython] Structure297  label="L137"  # Arch/BIM 172 (typed FeaturePython)
  Base = -> Rectangle006
  FaceMaker = 0
  Height = 150
  HorizontalArea = 1.25705e+07
  IfcData = attributes={"GlobalId": {"name": "GlobalId", "type": "IfcGloballyUniqueId", "is_enum": false, "enum_values": []}, "Description": {"... (+484 chars omitted),+1 more (map truncated)
  IfcType = 172
  Length = 0
  MoveBase = false
  MoveWithHost = false
  Nodes = (2) [(4057.5,1725,3000),(4057.5,1725,2850)]
  NodesOffset = 0
  Normal = (0,0,-1)
  PerimeterLength = 14310
  Placement = pos=(0,0,6000) rot=(0,0,1;0rad)
  PredefinedType = 0
  VerticalArea = 2146500
  Width = 150
FEATURE [Part::FeaturePython] Structure298  label="V15x40 V102a002"  # Arch/BIM 7 (typed FeaturePython)
  FaceMaker = 0
  Height = 400
  HorizontalArea = 405000
  IfcData = attributes={"GlobalId": {"name": "GlobalId", "type": "IfcGloballyUniqueId", "is_enum": false, "enum_values": []}, "Description": {"... (+475 chars omitted),+1 more (map truncated)
  IfcType = 7
  Length = 2700
  MoveBase = false
  MoveWithHost = false
  Nodes = (2) [(-1.72563e-31,-1.42109e-15,-7.77156e-16),(2700,-1.42109e-15,-7.77156e-16)]
  NodesOffset = 0
  Normal = (0,0,0)
  PerimeterLength = 5700
  Placement = pos=(8935,8295,8800) rot=(0,0,1;3.14159rad)
  PredefinedType = 0
  VerticalArea = 2.28e+06
  Width = 150
FEATURE [Part::FeaturePython] Structure299  label="V15x40 V107a002"  # Arch/BIM 7 (typed FeaturePython)
  FaceMaker = 0
  Height = 400
  HorizontalArea = 405000
  IfcData = attributes={"GlobalId": {"name": "GlobalId", "type": "IfcGloballyUniqueId", "is_enum": false, "enum_values": []}, "Description": {"... (+475 chars omitted),+1 more (map truncated)
  IfcType = 7
  Length = 2700
  MoveBase = false
  MoveWithHost = false
  Nodes = (2) [(-1.72563e-31,-1.42109e-15,-7.77156e-16),(2700,-1.42109e-15,-7.77156e-16)]
  NodesOffset = 0
  Normal = (0,0,0)
  PerimeterLength = 5700
  Placement = pos=(8935,4995,8800) rot=(0,0,1;3.14159rad)
  PredefinedType = 0
  VerticalArea = 2.28e+06
  Width = 150
FEATURE [Part::FeaturePython] Structure300  label="V15x40 V112a002"  # Arch/BIM 7 (typed FeaturePython)
  FaceMaker = 0
  Height = 400
  HorizontalArea = 405000
  IfcData = attributes={"GlobalId": {"name": "GlobalId", "type": "IfcGloballyUniqueId", "is_enum": false, "enum_values": []}, "Description": {"... (+475 chars omitted),+1 more (map truncated)
  IfcType = 7
  Length = 2700
  MoveBase = false
  MoveWithHost = false
  Nodes = (2) [(-1.72563e-31,-1.42109e-15,-7.77156e-16),(2700,-1.42109e-15,-7.77156e-16)]
  NodesOffset = 0
  Normal = (0,0,0)
  PerimeterLength = 5700
  Placement = pos=(8935,1700,8800) rot=(0,0,1;3.14159rad)
  PredefinedType = 0
  VerticalArea = 2.28e+06
  Width = 150
FEATURE [Part::FeaturePython] Structure301  label="V15x40 V130a002"  # Arch/BIM 7 (typed FeaturePython)
  FaceMaker = 0
  Height = 400
  HorizontalArea = 370500
  IfcData = attributes={"GlobalId": {"name": "GlobalId", "type": "IfcGloballyUniqueId", "is_enum": false, "enum_values": []}, "Description": {"... (+475 chars omitted),+1 more (map truncated)
  IfcType = 7
  Length = 2470
  MoveBase = false
  MoveWithHost = false
  Nodes = (2) [(-1.72563e-31,-1.42109e-15,-7.77156e-16),(2470,-1.42109e-15,-7.77156e-16)]
  NodesOffset = 0
  Normal = (0,0,0)
  PerimeterLength = 5240
  Placement = pos=(12010,3425,8800) rot=(0,0,1;1.5708rad)
  PredefinedType = 0
  VerticalArea = 2096000
  Width = 150
FEATURE [App::GeometryPython] BuildingPart017  label="Vigas sobre P2"  # Arch/BIM 172 (typed FeaturePython)
  Area = 0
  Group = -> [Structure298,Structure299,Structure300,Structure301,Structure261,Structure262,Structure263,Structure264,Structure265,Structure266,Structure267,Structure268,Structure269,Structure270,Structure271,Structure272,Structure273,Structure274,Structure275,Structure276,Structure277,Structure278,Structure279,Structure280,Structure281,Structure282,Structure283,Structure284,Structure285,Structure286,+8 more]
  Height = 0
  HeightPropagate = true
  IfcData = attributes={"GlobalId": {"name": "GlobalId", "type": "IfcGloballyUniqueId", "is_enum": false, "enum_values": []}, "Description": {"... (+484 chars omitted),+1 more (map truncated)
  IfcType = 172
  LevelOffset = 0
  PredefinedType = 0
FEATURE [Part::FeaturePython] Structure302  label="L138"  # Arch/BIM 172 (typed FeaturePython)
  Base = -> Rectangle014
  FaceMaker = 0
  Height = 150
  HorizontalArea = 3928500
  IfcData = attributes={"GlobalId": {"name": "GlobalId", "type": "IfcGloballyUniqueId", "is_enum": false, "enum_values": []}, "Description": {"... (+484 chars omitted),+1 more (map truncated)
  IfcType = 172
  Length = 0
  MoveBase = false
  MoveWithHost = false
  Nodes = (2) [(7585,9097.5,3000),(7585,9097.5,2850)]
  NodesOffset = 0
  Normal = (0,0,-1)
  PerimeterLength = 8310
  Placement = pos=(0,0,6000) rot=(0,0,1;0rad)
  PredefinedType = 0
  VerticalArea = 1246500
  Width = 150
FEATURE [Part::FeaturePython] Structure303  label="L139"  # Arch/BIM 172 (typed FeaturePython)
  Base = -> Wire
  FaceMaker = 0
  Height = 150
  HorizontalArea = 3.9285e+06
  IfcData = attributes={"GlobalId": {"name": "GlobalId", "type": "IfcGloballyUniqueId", "is_enum": false, "enum_values": []}, "Description": {"... (+484 chars omitted),+1 more (map truncated)
  IfcType = 172
  Length = 0
  MoveBase = false
  MoveWithHost = false
  Nodes = (2) [(7543.76,7449.37,3000),(7543.76,7449.37,2850)]
  NodesOffset = 0
  Normal = (0,0,-1)
  PerimeterLength = 8410
  Placement = pos=(0,0,5850) rot=(0,0,1;0rad)
  PredefinedType = 0
  VerticalArea = 1261500
  Width = 150
FEATURE [Part::FeaturePython] Structure304  label="L140"  # Arch/BIM 172 (typed FeaturePython)
  Base = -> Wire001
  FaceMaker = 0
  Height = 150
  HorizontalArea = 3.90134e+06
  IfcData = attributes={"GlobalId": {"name": "GlobalId", "type": "IfcGloballyUniqueId", "is_enum": false, "enum_values": []}, "Description": {"... (+484 chars omitted),+1 more (map truncated)
  IfcType = 172
  Length = 0
  MoveBase = false
  MoveWithHost = false
  Nodes = (2) [(7543.46,5835.61,3000),(7543.46,5835.61,2850)]
  NodesOffset = 0
  Normal = (0,0,-1)
  PerimeterLength = 8389.89
  Placement = pos=(0,0,5850) rot=(0,0,1;0rad)
  PredefinedType = 0
  VerticalArea = 1.25848e+06
  Width = 150
FEATURE [Part::FeaturePython] Structure305  label="L141"  # Arch/BIM 172 (typed FeaturePython)
  Base = -> Rectangle015
  FaceMaker = 0
  Height = 150
  HorizontalArea = 4.0365e+06
  IfcData = attributes={"GlobalId": {"name": "GlobalId", "type": "IfcGloballyUniqueId", "is_enum": false, "enum_values": []}, "Description": {"... (+484 chars omitted),+1 more (map truncated)
  IfcType = 172
  Length = 0
  MoveBase = false
  MoveWithHost = false
  Nodes = (2) [(7585,4172.5,3000),(7585,4172.5,2850)]
  NodesOffset = 0
  Normal = (0,0,-1)
  PerimeterLength = 8390
  Placement = pos=(0,0,6000) rot=(0,0,1;0rad)
  PredefinedType = 0
  VerticalArea = 1258500
  Width = 150
FEATURE [Part::FeaturePython] Structure306  label="L142"  # Arch/BIM 172 (typed FeaturePython)
  Base = -> Wire002
  FaceMaker = 0
  Height = 150
  HorizontalArea = 3.91484e+06
  IfcData = attributes={"GlobalId": {"name": "GlobalId", "type": "IfcGloballyUniqueId", "is_enum": false, "enum_values": []}, "Description": {"... (+484 chars omitted),+1 more (map truncated)
  IfcType = 172
  Length = 0
  MoveBase = false
  MoveWithHost = false
  Nodes = (2) [(7543.6,2543.13,3000),(7543.6,2543.13,2850)]
  NodesOffset = 0
  Normal = (0,0,-1)
  PerimeterLength = 8399.89
  Placement = pos=(0,0,5850) rot=(0,0,1;0rad)
  PredefinedType = 0
  VerticalArea = 1.25998e+06
  Width = 150
FEATURE [Part::FeaturePython] Structure307  label="L143"  # Arch/BIM 172 (typed FeaturePython)
  Base = -> Rectangle016
  FaceMaker = 0
  Height = 150
  HorizontalArea = 3.915e+06
  IfcData = attributes={"GlobalId": {"name": "GlobalId", "type": "IfcGloballyUniqueId", "is_enum": false, "enum_values": []}, "Description": {"... (+484 chars omitted),+1 more (map truncated)
  IfcType = 172
  Length = 0
  MoveBase = false
  MoveWithHost = false
  Nodes = (2) [(7585,900,3000),(7585,900,2850)]
  NodesOffset = 0
  Normal = (0,0,-1)
  PerimeterLength = 8300
  Placement = pos=(0,0,6000) rot=(0,0,1;0rad)
  PredefinedType = 0
  VerticalArea = 1.245e+06
  Width = 150
FEATURE [Part::FeaturePython] Structure308  label="L144"  # Arch/BIM 172 (typed FeaturePython)
  Base = -> Rectangle008
  FaceMaker = 0
  Height = 150
  HorizontalArea = 4354000
  IfcData = attributes={"GlobalId": {"name": "GlobalId", "type": "IfcGloballyUniqueId", "is_enum": false, "enum_values": []}, "Description": {"... (+484 chars omitted),+1 more (map truncated)
  IfcType = 172
  Length = 0
  MoveBase = false
  MoveWithHost = false
  Nodes = (2) [(9785,8270,3000),(9785,8270,2850)]
  NodesOffset = 0
  Normal = (0,0,-1)
  PerimeterLength = 9020
  Placement = pos=(0,0,6000) rot=(0,0,1;0rad)
  PredefinedType = 0
  VerticalArea = 1353000
  Width = 150
FEATURE [Part::FeaturePython] Structure309  label="L145"  # Arch/BIM 172 (typed FeaturePython)
  Base = -> Rectangle011
  FaceMaker = 0
  Height = 150
  HorizontalArea = 4396000
  IfcData = attributes={"GlobalId": {"name": "GlobalId", "type": "IfcGloballyUniqueId", "is_enum": false, "enum_values": []}, "Description": {"... (+484 chars omitted),+1 more (map truncated)
  IfcType = 172
  Length = 0
  MoveBase = false
  MoveWithHost = false
  Nodes = (2) [(9785,4995,3000),(9785,4995,2850)]
  NodesOffset = 0
  Normal = (0,0,-1)
  PerimeterLength = 9080
  Placement = pos=(0,0,6000) rot=(0,0,1;0rad)
  PredefinedType = 0
  VerticalArea = 1362000
  Width = 150
FEATURE [Part::FeaturePython] Structure310  label="L146"  # Arch/BIM 172 (typed FeaturePython)
  Base = -> Rectangle013
  FaceMaker = 0
  Height = 150
  HorizontalArea = 4.34e+06
  IfcData = attributes={"GlobalId": {"name": "GlobalId", "type": "IfcGloballyUniqueId", "is_enum": false, "enum_values": []}, "Description": {"... (+484 chars omitted),+1 more (map truncated)
  IfcType = 172
  Length = 0
  MoveBase = false
  MoveWithHost = false
  Nodes = (2) [(9785,1725,3000),(9785,1725,2850)]
  NodesOffset = 0
  Normal = (0,0,-1)
  PerimeterLength = 9000
  Placement = pos=(0,0,6000) rot=(0,0,1;0rad)
  PredefinedType = 0
  VerticalArea = 1350000
  Width = 150
FEATURE [Part::FeaturePython] Structure311  label="L147"  # Arch/BIM 172 (typed FeaturePython)
  Base = -> Rectangle009
  FaceMaker = 0
  Height = 150
  HorizontalArea = 1.794e+06
  IfcData = attributes={"GlobalId": {"name": "GlobalId", "type": "IfcGloballyUniqueId", "is_enum": false, "enum_values": []}, "Description": {"... (+484 chars omitted),+1 more (map truncated)
  IfcType = 172
  Length = 0
  MoveBase = false
  MoveWithHost = false
  Nodes = (2) [(11285,9135,3000),(11285,9135,2850)]
  NodesOffset = 0
  Normal = (0,0,-1)
  PerimeterLength = 5360
  Placement = pos=(0,0,6000) rot=(0,0,1;0rad)
  PredefinedType = 0
  VerticalArea = 804000
  Width = 150
FEATURE [Part::FeaturePython] Structure312  label="L148"  # Arch/BIM 172 (typed FeaturePython)
  Base = -> Rectangle018
  FaceMaker = 0
  Height = 150
  HorizontalArea = 3.211e+06
  IfcData = attributes={"GlobalId": {"name": "GlobalId", "type": "IfcGloballyUniqueId", "is_enum": false, "enum_values": []}, "Description": {"... (+484 chars omitted),+1 more (map truncated)
  IfcType = 172
  Length = 0
  MoveBase = false
  MoveWithHost = false
  Nodes = (2) [(11285,4660,3000),(11285,4660,2850)]
  NodesOffset = 0
  Normal = (0,0,-1)
  PerimeterLength = 7540
  Placement = pos=(0,0,6000) rot=(0,0,1;0rad)
  PredefinedType = 0
  VerticalArea = 1.131e+06
  Width = 150
FEATURE [Part::FeaturePython] Structure313  label="L149"  # Arch/BIM 172 (typed FeaturePython)
  Base = -> Rectangle020
  FaceMaker = 0
  Height = 150
  HorizontalArea = 9439500
  IfcData = attributes={"GlobalId": {"name": "GlobalId", "type": "IfcGloballyUniqueId", "is_enum": false, "enum_values": []}, "Description": {"... (+484 chars omitted),+1 more (map truncated)
  IfcType = 172
  Length = 0
  MoveBase = false
  MoveWithHost = false
  Nodes = (2) [(12157.5,1725,3000),(12157.5,1725,2850)]
  NodesOffset = 0
  Normal = (0,0,-1)
  PerimeterLength = 12290
  Placement = pos=(0,0,6000) rot=(0,0,1;0rad)
  PredefinedType = 0
  VerticalArea = 1843500
  Width = 150
FEATURE [Part::FeaturePython] Structure314  label="L150"  # Arch/BIM 172 (typed FeaturePython)
  Base = -> Rectangle019
  FaceMaker = 0
  Height = 150
  HorizontalArea = 3.93965e+06
  IfcData = attributes={"GlobalId": {"name": "GlobalId", "type": "IfcGloballyUniqueId", "is_enum": false, "enum_values": []}, "Description": {"... (+484 chars omitted),+1 more (map truncated)
  IfcType = 172
  Length = 0
  MoveBase = false
  MoveWithHost = false
  Nodes = (2) [(12882.5,4660,3000),(12882.5,4660,2850)]
  NodesOffset = 0
  Normal = (0,0,-1)
  PerimeterLength = 8130
  Placement = pos=(0,0,5850) rot=(0,0,1;0rad)
  PredefinedType = 0
  VerticalArea = 1.2195e+06
  Width = 150
FEATURE [Part::FeaturePython] Structure315  label="L151"  # Arch/BIM 172 (typed FeaturePython)
  Base = -> Rectangle017
  FaceMaker = 0
  Height = 150
  HorizontalArea = 4174500
  IfcData = attributes={"GlobalId": {"name": "GlobalId", "type": "IfcGloballyUniqueId", "is_enum": false, "enum_values": []}, "Description": {"... (+484 chars omitted),+1 more (map truncated)
  IfcType = 172
  Length = 0
  MoveBase = false
  MoveWithHost = false
  Nodes = (2) [(13597.5,9135,3000),(13597.5,9135,2850)]
  NodesOffset = 0
  Normal = (0,0,-1)
  PerimeterLength = 8810
  Placement = pos=(0,0,6000) rot=(0,0,1;0rad)
  PredefinedType = 0
  VerticalArea = 1321500
  Width = 150
FEATURE [App::GeometryPython] BuildingPart018  label="Losas sobre P2"  # Arch/BIM 172 (typed FeaturePython)
  Area = 0
  Group = -> [Structure295,Structure296,Structure297,Structure302,Structure303,Structure304,Structure305,Structure306,Structure307,Structure308,Structure309,Structure310,Structure311,Structure312,Structure313,Structure314,Structure315]
  Height = 0
  HeightPropagate = true
  IfcData = attributes={"GlobalId": {"name": "GlobalId", "type": "IfcGloballyUniqueId", "is_enum": false, "enum_values": []}, "Description": {"... (+484 chars omitted),+1 more (map truncated)
  IfcType = 172
  LevelOffset = 0
  PredefinedType = 0
FEATURE [App::GeometryPython] BuildingPart010  label="Piso 2"  # Arch/BIM 172 (typed FeaturePython)
  Area = 24900000
  Group = -> [BuildingPart016,BuildingPart018,Wall003,BuildingPart017]
  Height = 0
  HeightPropagate = true
  IfcData = attributes={"GlobalId": {"name": "GlobalId", "type": "IfcGloballyUniqueId", "is_enum": false, "enum_values": []}, "Description": {"... (+484 chars omitted),+1 more (map truncated)
  IfcType = 172
  LevelOffset = 0
  Placement = pos=(0,0,6000) rot=(0,0,1;0rad)
  PredefinedType = 0
FEATURE [Part::FeaturePython] Structure316  label="25x15 C064"  # Arch/BIM 24 (typed FeaturePython)
  FaceMaker = 0
  Height = 3000
  HorizontalArea = 37500
  IfcData = attributes={"GlobalId": {"name": "GlobalId", "type": "IfcGloballyUniqueId", "is_enum": false, "enum_values": []}, "Description": {"... (+438 chars omitted),+1 more (map truncated)
  IfcType = 24
  Length = 250
  MoveBase = false
  MoveWithHost = false
  Nodes = (2) [(-1.05471e-15,1.36424e-15,0),(-1.05471e-15,1.36424e-15,3000)]
  NodesOffset = 0
  Normal = (0,0,0)
  PerimeterLength = 800
  Placement = pos=(1930,9900,9000) rot=(0,0,1;0rad)
  PredefinedType = 0
  VerticalArea = 2400000
  Width = 150
FEATURE [Part::FeaturePython] Structure317  label="25x15 C065"  # Arch/BIM 172 (typed FeaturePython)
  FaceMaker = 0
  Height = 3000
  HorizontalArea = 37500
  IfcData = attributes={"GlobalId": {"name": "GlobalId", "type": "IfcGloballyUniqueId", "is_enum": false, "enum_values": []}, "Description": {"... (+484 chars omitted),+1 more (map truncated)
  IfcType = 172
  Length = 250
  MoveBase = false
  MoveWithHost = false
  Nodes = (2) [(-1.05471e-15,1.36424e-15,0),(-1.05471e-15,1.36424e-15,3000)]
  NodesOffset = 0
  Normal = (0,0,0)
  PerimeterLength = 800
  Placement = pos=(1930,100,9000) rot=(0,0,1;0rad)
  PredefinedType = 0
  VerticalArea = 2400000
  Width = 150
FEATURE [Part::FeaturePython] Structure318  label="25x15 C066"  # Arch/BIM 24 (typed FeaturePython)
  FaceMaker = 0
  Height = 3000
  HorizontalArea = 37500
  IfcData = attributes={"GlobalId": {"name": "GlobalId", "type": "IfcGloballyUniqueId", "is_enum": false, "enum_values": []}, "Description": {"... (+438 chars omitted),+1 more (map truncated)
  IfcType = 24
  Length = 250
  MoveBase = false
  MoveWithHost = false
  Nodes = (2) [(-1.05471e-15,1.36424e-15,0),(-1.05471e-15,1.36424e-15,3000)]
  NodesOffset = 0
  Normal = (0,0,0)
  PerimeterLength = 800
  Placement = pos=(6160,6640,9000) rot=(0,0,1;0rad)
  PredefinedType = 0
  VerticalArea = 2400000
  Width = 150
FEATURE [Part::FeaturePython] Structure319  label="25x15 C067"  # Arch/BIM 24 (typed FeaturePython)
  FaceMaker = 0
  Height = 3000
  HorizontalArea = 37500
  IfcData = attributes={"GlobalId": {"name": "GlobalId", "type": "IfcGloballyUniqueId", "is_enum": false, "enum_values": []}, "Description": {"... (+438 chars omitted),+1 more (map truncated)
  IfcType = 24
  Length = 250
  MoveBase = false
  MoveWithHost = false
  Nodes = (2) [(-1.05471e-15,1.36424e-15,0),(-1.05471e-15,1.36424e-15,3000)]
  NodesOffset = 0
  Normal = (0,0,0)
  PerimeterLength = 800
  Placement = pos=(6160,3350,9000) rot=(0,0,1;0rad)
  PredefinedType = 0
  VerticalArea = 2400000
  Width = 150
FEATURE [Part::FeaturePython] Structure320  label="25x15 C068"  # Arch/BIM 24 (typed FeaturePython)
  FaceMaker = 0
  Height = 3000
  HorizontalArea = 37500
  IfcData = attributes={"GlobalId": {"name": "GlobalId", "type": "IfcGloballyUniqueId", "is_enum": false, "enum_values": []}, "Description": {"... (+438 chars omitted),+1 more (map truncated)
  IfcType = 24
  Length = 250
  MoveBase = false
  MoveWithHost = false
  Nodes = (2) [(-1.05471e-15,1.36424e-15,0),(-1.05471e-15,1.36424e-15,3000)]
  NodesOffset = 0
  Normal = (0,0,0)
  PerimeterLength = 800
  Placement = pos=(6160,100,9000) rot=(0,0,1;0rad)
  PredefinedType = 0
  VerticalArea = 2400000
  Width = 150
FEATURE [Part::FeaturePython] Structure321  label="25x15 C069"  # Arch/BIM 24 (typed FeaturePython)
  FaceMaker = 0
  Height = 3000
  HorizontalArea = 37500
  IfcData = attributes={"GlobalId": {"name": "GlobalId", "type": "IfcGloballyUniqueId", "is_enum": false, "enum_values": []}, "Description": {"... (+438 chars omitted),+1 more (map truncated)
  IfcType = 24
  Length = 250
  MoveBase = false
  MoveWithHost = false
  Nodes = (2) [(-1.05471e-15,1.36424e-15,0),(-1.05471e-15,1.36424e-15,3000)]
  NodesOffset = 0
  Normal = (0,0,0)
  PerimeterLength = 800
  Placement = pos=(9010,100,9000) rot=(0,0,1;0rad)
  PredefinedType = 0
  VerticalArea = 2400000
  Width = 150
FEATURE [Part::FeaturePython] Structure322  label="25x15 C070"  # Arch/BIM 24 (typed FeaturePython)
  FaceMaker = 0
  Height = 3000
  HorizontalArea = 37500
  IfcData = attributes={"GlobalId": {"name": "GlobalId", "type": "IfcGloballyUniqueId", "is_enum": false, "enum_values": []}, "Description": {"... (+438 chars omitted),+1 more (map truncated)
  IfcType = 24
  Length = 250
  MoveBase = false
  MoveWithHost = false
  Nodes = (2) [(-1.05471e-15,1.36424e-15,0),(-1.05471e-15,1.36424e-15,3000)]
  NodesOffset = 0
  Normal = (0,0,0)
  PerimeterLength = 800
  Placement = pos=(10560,100,9000) rot=(0,0,1;0rad)
  PredefinedType = 0
  VerticalArea = 2400000
  Width = 150
FEATURE [Part::FeaturePython] Structure323  label="25x15 C071"  # Arch/BIM 24 (typed FeaturePython)
  FaceMaker = 0
  Height = 3000
  HorizontalArea = 37500
  IfcData = attributes={"GlobalId": {"name": "GlobalId", "type": "IfcGloballyUniqueId", "is_enum": false, "enum_values": []}, "Description": {"... (+438 chars omitted),+1 more (map truncated)
  IfcType = 24
  Length = 250
  MoveBase = false
  MoveWithHost = false
  Nodes = (2) [(-1.05471e-15,1.36424e-15,0),(-1.05471e-15,1.36424e-15,3000)]
  NodesOffset = 0
  Normal = (0,0,0)
  PerimeterLength = 800
  Placement = pos=(13780,100,9000) rot=(0,0,1;0rad)
  PredefinedType = 0
  VerticalArea = 2400000
  Width = 150
FEATURE [Part::FeaturePython] Structure324  label="25x15 C072"  # Arch/BIM 24 (typed FeaturePython)
  FaceMaker = 0
  Height = 3000
  HorizontalArea = 37500
  IfcData = attributes={"GlobalId": {"name": "GlobalId", "type": "IfcGloballyUniqueId", "is_enum": false, "enum_values": []}, "Description": {"... (+438 chars omitted),+1 more (map truncated)
  IfcType = 24
  Length = 250
  MoveBase = false
  MoveWithHost = false
  Nodes = (2) [(-1.05471e-15,1.36424e-15,0),(-1.05471e-15,1.36424e-15,3000)]
  NodesOffset = 0
  Normal = (0,0,0)
  PerimeterLength = 800
  Placement = pos=(15210,5970,9000) rot=(0,0,1;0rad)
  PredefinedType = 0
  VerticalArea = 2400000
  Width = 150
FEATURE [Part::FeaturePython] Structure325  label="25x15 C073"  # Arch/BIM 24 (typed FeaturePython)
  FaceMaker = 0
  Height = 3000
  HorizontalArea = 37500
  IfcData = attributes={"GlobalId": {"name": "GlobalId", "type": "IfcGloballyUniqueId", "is_enum": false, "enum_values": []}, "Description": {"... (+438 chars omitted),+1 more (map truncated)
  IfcType = 24
  Length = 250
  MoveBase = false
  MoveWithHost = false
  Nodes = (2) [(-1.05471e-15,1.36424e-15,0),(-1.05471e-15,1.36424e-15,3000)]
  NodesOffset = 0
  Normal = (0,0,0)
  PerimeterLength = 800
  Placement = pos=(13780,5970,9000) rot=(0,0,1;0rad)
  PredefinedType = 0
  VerticalArea = 2400000
  Width = 150
FEATURE [Part::FeaturePython] Structure326  label="25x15 C074"  # Arch/BIM 172 (typed FeaturePython)
  FaceMaker = 0
  Height = 3000
  HorizontalArea = 37500
  IfcData = attributes={"GlobalId": {"name": "GlobalId", "type": "IfcGloballyUniqueId", "is_enum": false, "enum_values": []}, "Description": {"... (+484 chars omitted),+1 more (map truncated)
  IfcType = 172
  Length = 250
  MoveBase = false
  MoveWithHost = false
  Nodes = (2) [(-1.05471e-15,1.36424e-15,0),(-1.05471e-15,1.36424e-15,3000)]
  NodesOffset = 0
  Normal = (0,0,0)
  PerimeterLength = 800
  Placement = pos=(1930,9900,9000) rot=(0,0,1;0rad)
  PredefinedType = 0
  VerticalArea = 2400000
  Width = 150
FEATURE [Part::FeaturePython] Structure327  label="25x15 C075"  # Arch/BIM 172 (typed FeaturePython)
  FaceMaker = 0
  Height = 3000
  HorizontalArea = 37500
  IfcData = attributes={"GlobalId": {"name": "GlobalId", "type": "IfcGloballyUniqueId", "is_enum": false, "enum_values": []}, "Description": {"... (+484 chars omitted),+1 more (map truncated)
  IfcType = 172
  Length = 250
  MoveBase = false
  MoveWithHost = false
  Nodes = (2) [(-1.05471e-15,1.36424e-15,0),(-1.05471e-15,1.36424e-15,3000)]
  NodesOffset = 0
  Normal = (0,0,0)
  PerimeterLength = 800
  Placement = pos=(9010,6640,9000) rot=(0,0,1;1.5708rad)
  PredefinedType = 0
  VerticalArea = 2400000
  Width = 150
FEATURE [Part::FeaturePython] Structure328  label="25x15 C076"  # Arch/BIM 172 (typed FeaturePython)
  FaceMaker = 0
  Height = 3000
  HorizontalArea = 37500
  IfcData = attributes={"GlobalId": {"name": "GlobalId", "type": "IfcGloballyUniqueId", "is_enum": false, "enum_values": []}, "Description": {"... (+484 chars omitted),+1 more (map truncated)
  IfcType = 172
  Length = 250
  MoveBase = false
  MoveWithHost = false
  Nodes = (2) [(-1.05471e-15,1.36424e-15,0),(-1.05471e-15,1.36424e-15,3000)]
  NodesOffset = 0
  Normal = (0,0,0)
  PerimeterLength = 800
  Placement = pos=(9010,3350,9000) rot=(0,0,1;1.5708rad)
  PredefinedType = 0
  VerticalArea = 2400000
  Width = 150
FEATURE [Part::FeaturePython] Structure329  label="25x15 C077"  # Arch/BIM 172 (typed FeaturePython)
  FaceMaker = 0
  Height = 3000
  HorizontalArea = 37500
  IfcData = attributes={"GlobalId": {"name": "GlobalId", "type": "IfcGloballyUniqueId", "is_enum": false, "enum_values": []}, "Description": {"... (+484 chars omitted),+1 more (map truncated)
  IfcType = 172
  Length = 250
  MoveBase = false
  MoveWithHost = false
  Nodes = (2) [(-1.05471e-15,1.36424e-15,0),(-1.05471e-15,1.36424e-15,3000)]
  NodesOffset = 0
  Normal = (0,0,0)
  PerimeterLength = 800
  Placement = pos=(10560,3350,9000) rot=(0,0,1;1.5708rad)
  PredefinedType = 0
  VerticalArea = 2400000
  Width = 150
FEATURE [Part::FeaturePython] Structure330  label="25x15 C078"  # Arch/BIM 172 (typed FeaturePython)
  FaceMaker = 0
  Height = 3000
  HorizontalArea = 37500
  IfcData = attributes={"GlobalId": {"name": "GlobalId", "type": "IfcGloballyUniqueId", "is_enum": false, "enum_values": []}, "Description": {"... (+484 chars omitted),+1 more (map truncated)
  IfcType = 172
  Length = 250
  MoveBase = false
  MoveWithHost = false
  Nodes = (2) [(-1.05471e-15,1.36424e-15,0),(-1.05471e-15,1.36424e-15,3000)]
  NodesOffset = 0
  Normal = (0,0,0)
  PerimeterLength = 800
  Placement = pos=(13780,3350,9000) rot=(0,0,1;1.5708rad)
  PredefinedType = 0
  VerticalArea = 2400000
  Width = 150
FEATURE [Part::FeaturePython] Structure331  label="25x15 C079"  # Arch/BIM 172 (typed FeaturePython)
  FaceMaker = 0
  Height = 3000
  HorizontalArea = 37500
  IfcData = attributes={"GlobalId": {"name": "GlobalId", "type": "IfcGloballyUniqueId", "is_enum": false, "enum_values": []}, "Description": {"... (+484 chars omitted),+1 more (map truncated)
  IfcType = 172
  Length = 250
  MoveBase = false
  MoveWithHost = false
  Nodes = (2) [(-1.05471e-15,1.36424e-15,0),(-1.05471e-15,1.36424e-15,3000)]
  NodesOffset = 0
  Normal = (0,0,0)
  PerimeterLength = 800
  Placement = pos=(9010,9900,9000) rot=(0,0,1;0rad)
  PredefinedType = 0
  VerticalArea = 2400000
  Width = 150
FEATURE [Part::FeaturePython] Structure332  label="25x15 C080"  # Arch/BIM 172 (typed FeaturePython)
  FaceMaker = 0
  Height = 3000
  HorizontalArea = 37500
  IfcData = attributes={"GlobalId": {"name": "GlobalId", "type": "IfcGloballyUniqueId", "is_enum": false, "enum_values": []}, "Description": {"... (+484 chars omitted),+1 more (map truncated)
  IfcType = 172
  Length = 250
  MoveBase = false
  MoveWithHost = false
  Nodes = (2) [(-1.05471e-15,1.36424e-15,0),(-1.05471e-15,1.36424e-15,3000)]
  NodesOffset = 0
  Normal = (0,0,0)
  PerimeterLength = 800
  Placement = pos=(6160,9900,9000) rot=(0,0,1;0rad)
  PredefinedType = 0
  VerticalArea = 2400000
  Width = 150
FEATURE [Part::FeaturePython] Structure333  label="25x15 C081"  # Arch/BIM 172 (typed FeaturePython)
  FaceMaker = 0
  Height = 3000
  HorizontalArea = 37500
  IfcData = attributes={"GlobalId": {"name": "GlobalId", "type": "IfcGloballyUniqueId", "is_enum": false, "enum_values": []}, "Description": {"... (+484 chars omitted),+1 more (map truncated)
  IfcType = 172
  Length = 250
  MoveBase = false
  MoveWithHost = false
  Nodes = (2) [(-1.05471e-15,1.36424e-15,0),(-1.05471e-15,1.36424e-15,3000)]
  NodesOffset = 0
  Normal = (0,0,0)
  PerimeterLength = 800
  Placement = pos=(12010,9900,9000) rot=(0,0,1;0rad)
  PredefinedType = 0
  VerticalArea = 2400000
  Width = 150
FEATURE [Part::FeaturePython] Structure334  label="25x15 C082"  # Arch/BIM 172 (typed FeaturePython)
  FaceMaker = 0
  Height = 3000
  HorizontalArea = 37500
  IfcData = attributes={"GlobalId": {"name": "GlobalId", "type": "IfcGloballyUniqueId", "is_enum": false, "enum_values": []}, "Description": {"... (+484 chars omitted),+1 more (map truncated)
  IfcType = 172
  Length = 250
  MoveBase = false
  MoveWithHost = false
  Nodes = (2) [(-1.05471e-15,1.36424e-15,0),(-1.05471e-15,1.36424e-15,3000)]
  NodesOffset = 0
  Normal = (0,0,0)
  PerimeterLength = 800
  Placement = pos=(15210,9900,9000) rot=(0,0,1;0rad)
  PredefinedType = 0
  VerticalArea = 2400000
  Width = 150
FEATURE [Part::FeaturePython] Structure335  label="25x20 C012"  # Arch/BIM 24 (typed FeaturePython)
  FaceMaker = 0
  Height = 3000
  HorizontalArea = 50000
  IfcData = attributes={"GlobalId": {"name": "GlobalId", "type": "IfcGloballyUniqueId", "is_enum": false, "enum_values": []}, "Description": {"... (+438 chars omitted),+1 more (map truncated)
  IfcType = 24
  Length = 250
  MoveBase = false
  MoveWithHost = false
  Nodes = (2) [(-1.05471e-15,-1.81899e-15,0),(-1.05471e-15,-1.81899e-15,3000)]
  NodesOffset = 0
  Normal = (0,0,0)
  PerimeterLength = 900
  Placement = pos=(1930,6640,9000) rot=(0,0,1;0rad)
  PredefinedType = 0
  VerticalArea = 2700000
  Width = 200
FEATURE [Part::FeaturePython] Structure336  label="25x20 C013"  # Arch/BIM 172 (typed FeaturePython)
  FaceMaker = 0
  Height = 3000
  HorizontalArea = 50000
  IfcData = attributes={"GlobalId": {"name": "GlobalId", "type": "IfcGloballyUniqueId", "is_enum": false, "enum_values": []}, "Description": {"... (+484 chars omitted),+1 more (map truncated)
  IfcType = 172
  Length = 250
  MoveBase = false
  MoveWithHost = false
  Nodes = (2) [(-1.05471e-15,-1.81899e-15,0),(-1.05471e-15,-1.81899e-15,3000)]
  NodesOffset = 0
  Normal = (0,0,0)
  PerimeterLength = 900
  Placement = pos=(1930,3350,9000) rot=(0,0,1;0rad)
  PredefinedType = 0
  VerticalArea = 2700000
  Width = 200
FEATURE [App::GeometryPython] BuildingPart020  label="Columnas sobre P3"  # Arch/BIM 172 (typed FeaturePython)
  Area = 0
  Group = -> [Structure316,Structure317,Structure318,Structure319,Structure320,Structure321,Structure322,Structure323,Structure324,Structure325,Structure326,Structure327,Structure328,Structure329,Structure330,Structure331,Structure332,Structure333,Structure334,Structure335,Structure336]
  Height = 0
  HeightPropagate = true
  IfcData = attributes={"GlobalId": {"name": "GlobalId", "type": "IfcGloballyUniqueId", "is_enum": false, "enum_values": []}, "Description": {"... (+484 chars omitted),+1 more (map truncated)
  IfcType = 172
  LevelOffset = 0
  PredefinedType = 0
FEATURE [Part::FeaturePython] Structure337  label="L152"  # Arch/BIM 172 (typed FeaturePython)
  Base = -> Rectangle004
  FaceMaker = 0
  Height = 150
  HorizontalArea = 12611050
  IfcData = attributes={"GlobalId": {"name": "GlobalId", "type": "IfcGloballyUniqueId", "is_enum": false, "enum_values": []}, "Description": {"... (+484 chars omitted),+1 more (map truncated)
  IfcType = 172
  Length = 0
  MoveBase = false
  MoveWithHost = false
  Nodes = (2) [(4057.5,8270,3000),(4057.5,8270,2850)]
  NodesOffset = 0
  Normal = (0,0,-1)
  PerimeterLength = 14330
  Placement = pos=(0,0,9000) rot=(0,0,1;0rad)
  PredefinedType = 0
  VerticalArea = 2149500
  Width = 150
FEATURE [Part::FeaturePython] Structure338  label="L153"  # Arch/BIM 172 (typed FeaturePython)
  Base = -> Rectangle005
  FaceMaker = 0
  Height = 150
  HorizontalArea = 12732700
  IfcData = attributes={"GlobalId": {"name": "GlobalId", "type": "IfcGloballyUniqueId", "is_enum": false, "enum_values": []}, "Description": {"... (+484 chars omitted),+1 more (map truncated)
  IfcType = 172
  Length = 0
  MoveBase = false
  MoveWithHost = false
  Nodes = (2) [(4057.5,4995,3000),(4057.5,4995,2850)]
  NodesOffset = 0
  Normal = (0,0,-1)
  PerimeterLength = 14390
  Placement = pos=(0,0,9000) rot=(0,0,1;0rad)
  PredefinedType = 0
  VerticalArea = 2158500
  Width = 150
FEATURE [Part::FeaturePython] Structure339  label="L154"  # Arch/BIM 172 (typed FeaturePython)
  Base = -> Rectangle006
  FaceMaker = 0
  Height = 150
  HorizontalArea = 1.25705e+07
  IfcData = attributes={"GlobalId": {"name": "GlobalId", "type": "IfcGloballyUniqueId", "is_enum": false, "enum_values": []}, "Description": {"... (+484 chars omitted),+1 more (map truncated)
  IfcType = 172
  Length = 0
  MoveBase = false
  MoveWithHost = false
  Nodes = (2) [(4057.5,1725,3000),(4057.5,1725,2850)]
  NodesOffset = 0
  Normal = (0,0,-1)
  PerimeterLength = 14310
  Placement = pos=(0,0,9000) rot=(0,0,1;0rad)
  PredefinedType = 0
  VerticalArea = 2146500
  Width = 150
FEATURE [Part::FeaturePython] Structure340  label="L155"  # Arch/BIM 172 (typed FeaturePython)
  Base = -> Rectangle014
  FaceMaker = 0
  Height = 150
  HorizontalArea = 3928500
  IfcData = attributes={"GlobalId": {"name": "GlobalId", "type": "IfcGloballyUniqueId", "is_enum": false, "enum_values": []}, "Description": {"... (+484 chars omitted),+1 more (map truncated)
  IfcType = 172
  Length = 0
  MoveBase = false
  MoveWithHost = false
  Nodes = (2) [(7585,9097.5,3000),(7585,9097.5,2850)]
  NodesOffset = 0
  Normal = (0,0,-1)
  PerimeterLength = 8310
  Placement = pos=(0,0,9000) rot=(0,0,1;0rad)
  PredefinedType = 0
  VerticalArea = 1246500
  Width = 150
FEATURE [Part::FeaturePython] Structure341  label="L156"  # Arch/BIM 172 (typed FeaturePython)
  Base = -> Wire
  FaceMaker = 0
  Height = 150
  HorizontalArea = 3.9285e+06
  IfcData = attributes={"GlobalId": {"name": "GlobalId", "type": "IfcGloballyUniqueId", "is_enum": false, "enum_values": []}, "Description": {"... (+484 chars omitted),+1 more (map truncated)
  IfcType = 172
  Length = 0
  MoveBase = false
  MoveWithHost = false
  Nodes = (2) [(7543.76,7449.37,3000),(7543.76,7449.37,2850)]
  NodesOffset = 0
  Normal = (0,0,-1)
  PerimeterLength = 8410
  Placement = pos=(0,0,9000) rot=(0,0,1;0rad)
  PredefinedType = 0
  VerticalArea = 1261500
  Width = 150
FEATURE [Part::FeaturePython] Structure342  label="L157"  # Arch/BIM 172 (typed FeaturePython)
  Base = -> Wire001
  FaceMaker = 0
  Height = 150
  HorizontalArea = 3.90134e+06
  IfcData = attributes={"GlobalId": {"name": "GlobalId", "type": "IfcGloballyUniqueId", "is_enum": false, "enum_values": []}, "Description": {"... (+484 chars omitted),+1 more (map truncated)
  IfcType = 172
  Length = 0
  MoveBase = false
  MoveWithHost = false
  Nodes = (2) [(7543.46,5835.61,3000),(7543.46,5835.61,2850)]
  NodesOffset = 0
  Normal = (0,0,-1)
  PerimeterLength = 8389.89
  Placement = pos=(0,0,9000) rot=(0,0,1;0rad)
  PredefinedType = 0
  VerticalArea = 1.25848e+06
  Width = 150
FEATURE [Part::FeaturePython] Structure343  label="L158"  # Arch/BIM 172 (typed FeaturePython)
  Base = -> Rectangle015
  FaceMaker = 0
  Height = 150
  HorizontalArea = 4.0365e+06
  IfcData = attributes={"GlobalId": {"name": "GlobalId", "type": "IfcGloballyUniqueId", "is_enum": false, "enum_values": []}, "Description": {"... (+484 chars omitted),+1 more (map truncated)
  IfcType = 172
  Length = 0
  MoveBase = false
  MoveWithHost = false
  Nodes = (2) [(7585,4172.5,3000),(7585,4172.5,2850)]
  NodesOffset = 0
  Normal = (0,0,-1)
  PerimeterLength = 8390
  Placement = pos=(0,0,9000) rot=(0,0,1;0rad)
  PredefinedType = 0
  VerticalArea = 1258500
  Width = 150
FEATURE [Part::FeaturePython] Structure344  label="L159"  # Arch/BIM 172 (typed FeaturePython)
  Base = -> Wire002
  FaceMaker = 0
  Height = 150
  HorizontalArea = 3.91484e+06
  IfcData = attributes={"GlobalId": {"name": "GlobalId", "type": "IfcGloballyUniqueId", "is_enum": false, "enum_values": []}, "Description": {"... (+484 chars omitted),+1 more (map truncated)
  IfcType = 172
  Length = 0
  MoveBase = false
  MoveWithHost = false
  Nodes = (2) [(7543.6,2543.13,3000),(7543.6,2543.13,2850)]
  NodesOffset = 0
  Normal = (0,0,-1)
  PerimeterLength = 8399.89
  Placement = pos=(0,0,9000) rot=(0,0,1;0rad)
  PredefinedType = 0
  VerticalArea = 1.25998e+06
  Width = 150
FEATURE [Part::FeaturePython] Structure345  label="L160"  # Arch/BIM 172 (typed FeaturePython)
  Base = -> Rectangle016
  FaceMaker = 0
  Height = 150
  HorizontalArea = 3.915e+06
  IfcData = attributes={"GlobalId": {"name": "GlobalId", "type": "IfcGloballyUniqueId", "is_enum": false, "enum_values": []}, "Description": {"... (+484 chars omitted),+1 more (map truncated)
  IfcType = 172
  Length = 0
  MoveBase = false
  MoveWithHost = false
  Nodes = (2) [(7585,900,3000),(7585,900,2850)]
  NodesOffset = 0
  Normal = (0,0,-1)
  PerimeterLength = 8300
  Placement = pos=(0,0,9000) rot=(0,0,1;0rad)
  PredefinedType = 0
  VerticalArea = 1.245e+06
  Width = 150
FEATURE [Part::FeaturePython] Structure346  label="L161"  # Arch/BIM 172 (typed FeaturePython)
  Base = -> Rectangle008
  FaceMaker = 0
  Height = 150
  HorizontalArea = 4354000
  IfcData = attributes={"GlobalId": {"name": "GlobalId", "type": "IfcGloballyUniqueId", "is_enum": false, "enum_values": []}, "Description": {"... (+484 chars omitted),+1 more (map truncated)
  IfcType = 172
  Length = 0
  MoveBase = false
  MoveWithHost = false
  Nodes = (2) [(9785,8270,3000),(9785,8270,2850)]
  NodesOffset = 0
  Normal = (0,0,-1)
  PerimeterLength = 9020
  Placement = pos=(0,0,9000) rot=(0,0,1;0rad)
  PredefinedType = 0
  VerticalArea = 1353000
  Width = 150
FEATURE [Part::FeaturePython] Structure347  label="L162"  # Arch/BIM 172 (typed FeaturePython)
  Base = -> Rectangle011
  FaceMaker = 0
  Height = 150
  HorizontalArea = 4396000
  IfcData = attributes={"GlobalId": {"name": "GlobalId", "type": "IfcGloballyUniqueId", "is_enum": false, "enum_values": []}, "Description": {"... (+484 chars omitted),+1 more (map truncated)
  IfcType = 172
  Length = 0
  MoveBase = false
  MoveWithHost = false
  Nodes = (2) [(9785,4995,3000),(9785,4995,2850)]
  NodesOffset = 0
  Normal = (0,0,-1)
  PerimeterLength = 9080
  Placement = pos=(0,0,9000) rot=(0,0,1;0rad)
  PredefinedType = 0
  VerticalArea = 1362000
  Width = 150
FEATURE [Part::FeaturePython] Structure348  label="L163"  # Arch/BIM 172 (typed FeaturePython)
  Base = -> Rectangle013
  FaceMaker = 0
  Height = 150
  HorizontalArea = 4.34e+06
  IfcData = attributes={"GlobalId": {"name": "GlobalId", "type": "IfcGloballyUniqueId", "is_enum": false, "enum_values": []}, "Description": {"... (+484 chars omitted),+1 more (map truncated)
  IfcType = 172
  Length = 0
  MoveBase = false
  MoveWithHost = false
  Nodes = (2) [(9785,1725,3000),(9785,1725,2850)]
  NodesOffset = 0
  Normal = (0,0,-1)
  PerimeterLength = 9000
  Placement = pos=(0,0,9000) rot=(0,0,1;0rad)
  PredefinedType = 0
  VerticalArea = 1350000
  Width = 150
FEATURE [Part::FeaturePython] Structure349  label="L164"  # Arch/BIM 172 (typed FeaturePython)
  Base = -> Rectangle009
  FaceMaker = 0
  Height = 150
  HorizontalArea = 1.794e+06
  IfcData = attributes={"GlobalId": {"name": "GlobalId", "type": "IfcGloballyUniqueId", "is_enum": false, "enum_values": []}, "Description": {"... (+484 chars omitted),+1 more (map truncated)
  IfcType = 172
  Length = 0
  MoveBase = false
  MoveWithHost = false
  Nodes = (2) [(11285,9135,3000),(11285,9135,2850)]
  NodesOffset = 0
  Normal = (0,0,-1)
  PerimeterLength = 5360
  Placement = pos=(0,0,9000) rot=(0,0,1;0rad)
  PredefinedType = 0
  VerticalArea = 804000
  Width = 150
FEATURE [Part::FeaturePython] Structure350  label="L165"  # Arch/BIM 172 (typed FeaturePython)
  Base = -> Rectangle018
  FaceMaker = 0
  Height = 150
  HorizontalArea = 3.211e+06
  IfcData = attributes={"GlobalId": {"name": "GlobalId", "type": "IfcGloballyUniqueId", "is_enum": false, "enum_values": []}, "Description": {"... (+484 chars omitted),+1 more (map truncated)
  IfcType = 172
  Length = 0
  MoveBase = false
  MoveWithHost = false
  Nodes = (2) [(11285,4660,3000),(11285,4660,2850)]
  NodesOffset = 0
  Normal = (0,0,-1)
  PerimeterLength = 7540
  Placement = pos=(0,0,9000) rot=(0,0,1;0rad)
  PredefinedType = 0
  VerticalArea = 1.131e+06
  Width = 150
FEATURE [Part::FeaturePython] Structure351  label="L166"  # Arch/BIM 172 (typed FeaturePython)
  Base = -> Rectangle020
  FaceMaker = 0
  Height = 150
  HorizontalArea = 9439500
  IfcData = attributes={"GlobalId": {"name": "GlobalId", "type": "IfcGloballyUniqueId", "is_enum": false, "enum_values": []}, "Description": {"... (+484 chars omitted),+1 more (map truncated)
  IfcType = 172
  Length = 0
  MoveBase = false
  MoveWithHost = false
  Nodes = (2) [(12157.5,1725,3000),(12157.5,1725,2850)]
  NodesOffset = 0
  Normal = (0,0,-1)
  PerimeterLength = 12290
  Placement = pos=(0,0,9000) rot=(0,0,1;0rad)
  PredefinedType = 0
  VerticalArea = 1843500
  Width = 150
FEATURE [Part::FeaturePython] Structure352  label="L167"  # Arch/BIM 172 (typed FeaturePython)
  Base = -> Rectangle019
  FaceMaker = 0
  Height = 150
  HorizontalArea = 3.93965e+06
  IfcData = attributes={"GlobalId": {"name": "GlobalId", "type": "IfcGloballyUniqueId", "is_enum": false, "enum_values": []}, "Description": {"... (+484 chars omitted),+1 more (map truncated)
  IfcType = 172
  Length = 0
  MoveBase = false
  MoveWithHost = false
  Nodes = (2) [(12882.5,4660,3000),(12882.5,4660,2850)]
  NodesOffset = 0
  Normal = (0,0,-1)
  PerimeterLength = 8130
  Placement = pos=(0,0,9000) rot=(0,0,1;0rad)
  PredefinedType = 0
  VerticalArea = 1.2195e+06
  Width = 150
FEATURE [Part::FeaturePython] Structure353  label="L168"  # Arch/BIM 172 (typed FeaturePython)
  Base = -> Rectangle017
  FaceMaker = 0
  Height = 150
  HorizontalArea = 4174500
  IfcData = attributes={"GlobalId": {"name": "GlobalId", "type": "IfcGloballyUniqueId", "is_enum": false, "enum_values": []}, "Description": {"... (+484 chars omitted),+1 more (map truncated)
  IfcType = 172
  Length = 0
  MoveBase = false
  MoveWithHost = false
  Nodes = (2) [(13597.5,9135,3000),(13597.5,9135,2850)]
  NodesOffset = 0
  Normal = (0,0,-1)
  PerimeterLength = 8810
  Placement = pos=(0,0,9000) rot=(0,0,1;0rad)
  PredefinedType = 0
  VerticalArea = 1321500
  Width = 150
FEATURE [App::GeometryPython] BuildingPart021  label="Losas sobre P3"  # Arch/BIM 172 (typed FeaturePython)
  Area = 0
  Group = -> [Structure337,Structure338,Structure339,Structure340,Structure341,Structure342,Structure343,Structure344,Structure345,Structure346,Structure347,Structure348,Structure349,Structure350,Structure351,Structure352,Structure353]
  Height = 0
  HeightPropagate = true
  IfcData = attributes={"GlobalId": {"name": "GlobalId", "type": "IfcGloballyUniqueId", "is_enum": false, "enum_values": []}, "Description": {"... (+484 chars omitted),+1 more (map truncated)
  IfcType = 172
  LevelOffset = 0
  PredefinedType = 0
FEATURE [Part::FeaturePython] Wall004  label="Tabique Ascensor P3"  # Arch/BIM 166 (typed FeaturePython)
  Align = 1
  Area = 24900000
  Base = -> Rectangle003
  BlockHeight = 0
  BlockLength = 0
  CountBroken = 0
  CountEntire = 0
  Face = 0
  Height = 3000
  HorizontalArea = 1155000
  IfcData = attributes={"GlobalId": {"name": "GlobalId", "type": "IfcGloballyUniqueId", "is_enum": false, "enum_values": []}, "Description": {"... (+533 chars omitted),+1 more (map truncated)
  IfcType = 166
  Joint = 0
  Length = 8300
  MakeBlocks = false
  MoveBase = false
  MoveWithHost = false
  Normal = (0,0,0)
  OffsetFirst = 0
  OffsetSecond = 0
  PerimeterLength = 8300
  Placement = pos=(0,0,9000) rot=(0,0,1;0rad)
  PredefinedType = 0
  VerticalArea = 46200000
  Width = 150
FEATURE [Part::FeaturePython] Structure354  label="V15x40 V102a003"  # Arch/BIM 7 (typed FeaturePython)
  FaceMaker = 0
  Height = 400
  HorizontalArea = 405000
  IfcData = attributes={"GlobalId": {"name": "GlobalId", "type": "IfcGloballyUniqueId", "is_enum": false, "enum_values": []}, "Description": {"... (+475 chars omitted),+1 more (map truncated)
  IfcType = 7
  Length = 2700
  MoveBase = false
  MoveWithHost = false
  Nodes = (2) [(-1.72563e-31,-1.42109e-15,-7.77156e-16),(2700,-1.42109e-15,-7.77156e-16)]
  NodesOffset = 0
  Normal = (0,0,0)
  PerimeterLength = 5700
  Placement = pos=(8935,8295,11800) rot=(0,0,1;3.14159rad)
  PredefinedType = 0
  VerticalArea = 2.28e+06
  Width = 150
FEATURE [Part::FeaturePython] Structure355  label="V15x40 V107a003"  # Arch/BIM 7 (typed FeaturePython)
  FaceMaker = 0
  Height = 400
  HorizontalArea = 405000
  IfcData = attributes={"GlobalId": {"name": "GlobalId", "type": "IfcGloballyUniqueId", "is_enum": false, "enum_values": []}, "Description": {"... (+475 chars omitted),+1 more (map truncated)
  IfcType = 7
  Length = 2700
  MoveBase = false
  MoveWithHost = false
  Nodes = (2) [(-1.72563e-31,-1.42109e-15,-7.77156e-16),(2700,-1.42109e-15,-7.77156e-16)]
  NodesOffset = 0
  Normal = (0,0,0)
  PerimeterLength = 5700
  Placement = pos=(8935,4995,11800) rot=(0,0,1;3.14159rad)
  PredefinedType = 0
  VerticalArea = 2.28e+06
  Width = 150
FEATURE [Part::FeaturePython] Structure356  label="V15x40 V112a003"  # Arch/BIM 7 (typed FeaturePython)
  FaceMaker = 0
  Height = 400
  HorizontalArea = 405000
  IfcData = attributes={"GlobalId": {"name": "GlobalId", "type": "IfcGloballyUniqueId", "is_enum": false, "enum_values": []}, "Description": {"... (+475 chars omitted),+1 more (map truncated)
  IfcType = 7
  Length = 2700
  MoveBase = false
  MoveWithHost = false
  Nodes = (2) [(-1.72563e-31,-1.42109e-15,-7.77156e-16),(2700,-1.42109e-15,-7.77156e-16)]
  NodesOffset = 0
  Normal = (0,0,0)
  PerimeterLength = 5700
  Placement = pos=(8935,1700,11800) rot=(0,0,1;3.14159rad)
  PredefinedType = 0
  VerticalArea = 2.28e+06
  Width = 150
FEATURE [Part::FeaturePython] Structure357  label="V15x40 V130a003"  # Arch/BIM 7 (typed FeaturePython)
  FaceMaker = 0
  Height = 400
  HorizontalArea = 370500
  IfcData = attributes={"GlobalId": {"name": "GlobalId", "type": "IfcGloballyUniqueId", "is_enum": false, "enum_values": []}, "Description": {"... (+475 chars omitted),+1 more (map truncated)
  IfcType = 7
  Length = 2470
  MoveBase = false
  MoveWithHost = false
  Nodes = (2) [(-1.72563e-31,-1.42109e-15,-7.77156e-16),(2470,-1.42109e-15,-7.77156e-16)]
  NodesOffset = 0
  Normal = (0,0,0)
  PerimeterLength = 5240
  Placement = pos=(12010,3425,11800) rot=(0,0,1;1.5708rad)
  PredefinedType = 0
  VerticalArea = 2096000
  Width = 150
FEATURE [Part::FeaturePython] Structure358  label="V15x40 V189"  # Arch/BIM 7 (typed FeaturePython)
  FaceMaker = 0
  Height = 400
  HorizontalArea = 597000
  IfcData = attributes={"GlobalId": {"name": "GlobalId", "type": "IfcGloballyUniqueId", "is_enum": false, "enum_values": []}, "Description": {"... (+475 chars omitted),+1 more (map truncated)
  IfcType = 7
  Length = 3980
  MoveBase = false
  MoveWithHost = false
  Nodes = (2) [(-1.72563e-31,-1.42109e-15,-7.77156e-16),(3980,-1.42109e-15,-7.77156e-16)]
  NodesOffset = 0
  Normal = (0,0,0)
  PerimeterLength = 8260
  Placement = pos=(2055,9900,11800) rot=(0,0,1;0rad)
  PredefinedType = 0
  VerticalArea = 3.304e+06
  Width = 150
FEATURE [Part::FeaturePython] Structure359  label="V15x40 V190"  # Arch/BIM 7 (typed FeaturePython)
  FaceMaker = 0
  Height = 400
  HorizontalArea = 390000
  IfcData = attributes={"GlobalId": {"name": "GlobalId", "type": "IfcGloballyUniqueId", "is_enum": false, "enum_values": []}, "Description": {"... (+475 chars omitted),+1 more (map truncated)
  IfcType = 7
  Length = 2600
  MoveBase = false
  MoveWithHost = false
  Nodes = (2) [(-1.72563e-31,-1.42109e-15,-7.77156e-16),(2600,-1.42109e-15,-7.77156e-16)]
  NodesOffset = 0
  Normal = (0,0,0)
  PerimeterLength = 5500
  Placement = pos=(6285,9900,11800) rot=(0,0,1;0rad)
  PredefinedType = 0
  VerticalArea = 2200000
  Width = 150
FEATURE [Part::FeaturePython] Structure360  label="V15x40 V191"  # Arch/BIM 7 (typed FeaturePython)
  FaceMaker = 0
  Height = 400
  HorizontalArea = 412500
  IfcData = attributes={"GlobalId": {"name": "GlobalId", "type": "IfcGloballyUniqueId", "is_enum": false, "enum_values": []}, "Description": {"... (+475 chars omitted),+1 more (map truncated)
  IfcType = 7
  Length = 2750
  MoveBase = false
  MoveWithHost = false
  Nodes = (2) [(-1.72563e-31,-1.42109e-15,-7.77156e-16),(2750,-1.42109e-15,-7.77156e-16)]
  NodesOffset = 0
  Normal = (0,0,0)
  PerimeterLength = 5800
  Placement = pos=(9135,9900,11800) rot=(0,0,1;0rad)
  PredefinedType = 0
  VerticalArea = 2320000
  Width = 150
FEATURE [Part::FeaturePython] Structure361  label="V15x40 V192"  # Arch/BIM 7 (typed FeaturePython)
  FaceMaker = 0
  Height = 400
  HorizontalArea = 442500
  IfcData = attributes={"GlobalId": {"name": "GlobalId", "type": "IfcGloballyUniqueId", "is_enum": false, "enum_values": []}, "Description": {"... (+475 chars omitted),+1 more (map truncated)
  IfcType = 7
  Length = 2950
  MoveBase = false
  MoveWithHost = false
  Nodes = (2) [(-1.72563e-31,-1.42109e-15,-7.77156e-16),(2950,-1.42109e-15,-7.77156e-16)]
  NodesOffset = 0
  Normal = (0,0,0)
  PerimeterLength = 6200
  Placement = pos=(12135,9900,11800) rot=(0,0,1;0rad)
  PredefinedType = 0
  VerticalArea = 2.48e+06
  Width = 150
FEATURE [Part::FeaturePython] Structure362  label="V15x40 V193"  # Arch/BIM 7 (typed FeaturePython)
  FaceMaker = 0
  Height = 400
  HorizontalArea = 453750
  IfcData = attributes={"GlobalId": {"name": "GlobalId", "type": "IfcGloballyUniqueId", "is_enum": false, "enum_values": []}, "Description": {"... (+475 chars omitted),+1 more (map truncated)
  IfcType = 7
  Length = 3025
  MoveBase = false
  MoveWithHost = false
  Nodes = (2) [(-1.72563e-31,-1.42109e-15,-7.77156e-16),(3025,-1.42109e-15,-7.77156e-16)]
  NodesOffset = 0
  Normal = (0,0,0)
  PerimeterLength = 6350
  Placement = pos=(12085,8370,11800) rot=(0,0,1;0rad)
  PredefinedType = 0
  VerticalArea = 2.54e+06
  Width = 150
FEATURE [Part::FeaturePython] Structure363  label="V15x40 V194"  # Arch/BIM 7 (typed FeaturePython)
  FaceMaker = 0
  Height = 400
  HorizontalArea = 597000
  IfcData = attributes={"GlobalId": {"name": "GlobalId", "type": "IfcGloballyUniqueId", "is_enum": false, "enum_values": []}, "Description": {"... (+475 chars omitted),+1 more (map truncated)
  IfcType = 7
  Length = 3980
  MoveBase = false
  MoveWithHost = false
  Nodes = (2) [(-1.72563e-31,-1.42109e-15,-7.77156e-16),(3980,-1.42109e-15,-7.77156e-16)]
  NodesOffset = 0
  Normal = (0,0,0)
  PerimeterLength = 8260
  Placement = pos=(2055,6640,11800) rot=(0,0,1;0rad)
  PredefinedType = 0
  VerticalArea = 3.304e+06
  Width = 150
FEATURE [Part::FeaturePython] Structure364  label="V15x40 V195"  # Arch/BIM 7 (typed FeaturePython)
  FaceMaker = 0
  Height = 400
  HorizontalArea = 397500
  IfcData = attributes={"GlobalId": {"name": "GlobalId", "type": "IfcGloballyUniqueId", "is_enum": false, "enum_values": []}, "Description": {"... (+475 chars omitted),+1 more (map truncated)
  IfcType = 7
  Length = 2650
  MoveBase = false
  MoveWithHost = false
  Nodes = (2) [(-1.72563e-31,-1.42109e-15,-7.77156e-16),(2650,-1.42109e-15,-7.77156e-16)]
  NodesOffset = 0
  Normal = (0,0,0)
  PerimeterLength = 5600
  Placement = pos=(6285,6640,11800) rot=(0,0,1;0rad)
  PredefinedType = 0
  VerticalArea = 2240000
  Width = 150
FEATURE [Part::FeaturePython] Structure365  label="V15x40 V196"  # Arch/BIM 7 (typed FeaturePython)
  FaceMaker = 0
  Height = 400
  HorizontalArea = 210000
  IfcData = attributes={"GlobalId": {"name": "GlobalId", "type": "IfcGloballyUniqueId", "is_enum": false, "enum_values": []}, "Description": {"... (+475 chars omitted),+1 more (map truncated)
  IfcType = 7
  Length = 1400
  MoveBase = false
  MoveWithHost = false
  Nodes = (2) [(-1.72563e-31,-1.42109e-15,-7.77156e-16),(1400,-1.42109e-15,-7.77156e-16)]
  NodesOffset = 0
  Normal = (0,0,0)
  PerimeterLength = 3100
  Placement = pos=(9085,6640,11800) rot=(0,0,1;0rad)
  PredefinedType = 0
  VerticalArea = 1240000
  Width = 150
FEATURE [Part::FeaturePython] Structure366  label="V15x40 V197"  # Arch/BIM 7 (typed FeaturePython)
  FaceMaker = 0
  Height = 400
  HorizontalArea = 235500
  IfcData = attributes={"GlobalId": {"name": "GlobalId", "type": "IfcGloballyUniqueId", "is_enum": false, "enum_values": []}, "Description": {"... (+475 chars omitted),+1 more (map truncated)
  IfcType = 7
  Length = 1570
  MoveBase = false
  MoveWithHost = false
  Nodes = (2) [(-1.72563e-31,-1.42109e-15,-7.77156e-16),(1570,-1.42109e-15,-7.77156e-16)]
  NodesOffset = 0
  Normal = (0,0,0)
  PerimeterLength = 3440
  Placement = pos=(13655,5970,11800) rot=(0,0,1;3.14159rad)
  PredefinedType = 0
  VerticalArea = 1.376e+06
  Width = 150
FEATURE [Part::FeaturePython] Structure367  label="V15x40 V198"  # Arch/BIM 7 (typed FeaturePython)
  FaceMaker = 0
  Height = 400
  HorizontalArea = 177000
  IfcData = attributes={"GlobalId": {"name": "GlobalId", "type": "IfcGloballyUniqueId", "is_enum": false, "enum_values": []}, "Description": {"... (+475 chars omitted),+1 more (map truncated)
  IfcType = 7
  Length = 1180
  MoveBase = false
  MoveWithHost = false
  Nodes = (2) [(-1.72563e-31,-1.42109e-15,-7.77156e-16),(1180,-1.42109e-15,-7.77156e-16)]
  NodesOffset = 0
  Normal = (0,0,0)
  PerimeterLength = 2660
  Placement = pos=(13905,5970,11800) rot=(0,0,1;0rad)
  PredefinedType = 0
  VerticalArea = 1064000
  Width = 150
FEATURE [Part::FeaturePython] Structure368  label="V15x40 V199"  # Arch/BIM 7 (typed FeaturePython)
  FaceMaker = 0
  Height = 400
  HorizontalArea = 597000
  IfcData = attributes={"GlobalId": {"name": "GlobalId", "type": "IfcGloballyUniqueId", "is_enum": false, "enum_values": []}, "Description": {"... (+475 chars omitted),+1 more (map truncated)
  IfcType = 7
  Length = 3980
  MoveBase = false
  MoveWithHost = false
  Nodes = (2) [(-1.72563e-31,-1.42109e-15,-7.77156e-16),(3980,-1.42109e-15,-7.77156e-16)]
  NodesOffset = 0
  Normal = (0,0,0)
  PerimeterLength = 8260
  Placement = pos=(2055,3350,11800) rot=(0,0,1;0rad)
  PredefinedType = 0
  VerticalArea = 3.304e+06
  Width = 150
FEATURE [Part::FeaturePython] Structure369  label="V15x40 V200"  # Arch/BIM 7 (typed FeaturePython)
  FaceMaker = 0
  Height = 400
  HorizontalArea = 397500
  IfcData = attributes={"GlobalId": {"name": "GlobalId", "type": "IfcGloballyUniqueId", "is_enum": false, "enum_values": []}, "Description": {"... (+475 chars omitted),+1 more (map truncated)
  IfcType = 7
  Length = 2650
  MoveBase = false
  MoveWithHost = false
  Nodes = (2) [(-1.72563e-31,-1.42109e-15,-7.77156e-16),(2650,-1.42109e-15,-7.77156e-16)]
  NodesOffset = 0
  Normal = (0,0,0)
  PerimeterLength = 5600
  Placement = pos=(6285,3350,11800) rot=(0,0,1;0rad)
  PredefinedType = 0
  VerticalArea = 2240000
  Width = 150
FEATURE [Part::FeaturePython] Structure370  label="V15x40 V201"  # Arch/BIM 7 (typed FeaturePython)
  FaceMaker = 0
  Height = 400
  HorizontalArea = 210000
  IfcData = attributes={"GlobalId": {"name": "GlobalId", "type": "IfcGloballyUniqueId", "is_enum": false, "enum_values": []}, "Description": {"... (+475 chars omitted),+1 more (map truncated)
  IfcType = 7
  Length = 1400
  MoveBase = false
  MoveWithHost = false
  Nodes = (2) [(-1.72563e-31,-1.42109e-15,-7.77156e-16),(1400,-1.42109e-15,-7.77156e-16)]
  NodesOffset = 0
  Normal = (0,0,0)
  PerimeterLength = 3100
  Placement = pos=(9085,3350,11800) rot=(0,0,1;0rad)
  PredefinedType = 0
  VerticalArea = 1240000
  Width = 150
FEATURE [Part::FeaturePython] Structure371  label="V15x40 V202"  # Arch/BIM 7 (typed FeaturePython)
  FaceMaker = 0
  Height = 400
  HorizontalArea = 460500
  IfcData = attributes={"GlobalId": {"name": "GlobalId", "type": "IfcGloballyUniqueId", "is_enum": false, "enum_values": []}, "Description": {"... (+475 chars omitted),+1 more (map truncated)
  IfcType = 7
  Length = 3070
  MoveBase = false
  MoveWithHost = false
  Nodes = (2) [(-1.72563e-31,-1.42109e-15,-7.77156e-16),(3070,-1.42109e-15,-7.77156e-16)]
  NodesOffset = 0
  Normal = (0,0,0)
  PerimeterLength = 6440
  Placement = pos=(10635,3350,11800) rot=(0,0,1;0rad)
  PredefinedType = 0
  VerticalArea = 2.576e+06
  Width = 150
FEATURE [Part::FeaturePython] Structure372  label="V15x40 V203"  # Arch/BIM 7 (typed FeaturePython)
  FaceMaker = 0
  Height = 400
  HorizontalArea = 597000
  IfcData = attributes={"GlobalId": {"name": "GlobalId", "type": "IfcGloballyUniqueId", "is_enum": false, "enum_values": []}, "Description": {"... (+475 chars omitted),+1 more (map truncated)
  IfcType = 7
  Length = 3980
  MoveBase = false
  MoveWithHost = false
  Nodes = (2) [(-1.72563e-31,-1.42109e-15,-7.77156e-16),(3980,-1.42109e-15,-7.77156e-16)]
  NodesOffset = 0
  Normal = (0,0,0)
  PerimeterLength = 8260
  Placement = pos=(2055,100,11800) rot=(0,0,1;0rad)
  PredefinedType = 0
  VerticalArea = 3.304e+06
  Width = 150
FEATURE [Part::FeaturePython] Structure373  label="V15x40 V204"  # Arch/BIM 7 (typed FeaturePython)
  FaceMaker = 0
  Height = 400
  HorizontalArea = 390000
  IfcData = attributes={"GlobalId": {"name": "GlobalId", "type": "IfcGloballyUniqueId", "is_enum": false, "enum_values": []}, "Description": {"... (+475 chars omitted),+1 more (map truncated)
  IfcType = 7
  Length = 2600
  MoveBase = false
  MoveWithHost = false
  Nodes = (2) [(-1.72563e-31,-1.42109e-15,-7.77156e-16),(2600,-1.42109e-15,-7.77156e-16)]
  NodesOffset = 0
  Normal = (0,0,0)
  PerimeterLength = 5500
  Placement = pos=(6285,100,11800) rot=(0,0,1;0rad)
  PredefinedType = 0
  VerticalArea = 2200000
  Width = 150
FEATURE [Part::FeaturePython] Structure374  label="V15x40 V205"  # Arch/BIM 7 (typed FeaturePython)
  FaceMaker = 0
  Height = 400
  HorizontalArea = 195000
  IfcData = attributes={"GlobalId": {"name": "GlobalId", "type": "IfcGloballyUniqueId", "is_enum": false, "enum_values": []}, "Description": {"... (+475 chars omitted),+1 more (map truncated)
  IfcType = 7
  Length = 1300
  MoveBase = false
  MoveWithHost = false
  Nodes = (2) [(-1.72563e-31,-1.42109e-15,-7.77156e-16),(1300,-1.42109e-15,-7.77156e-16)]
  NodesOffset = 0
  Normal = (0,0,0)
  PerimeterLength = 2900
  Placement = pos=(9135,100,11800) rot=(0,0,1;0rad)
  PredefinedType = 0
  VerticalArea = 1160000
  Width = 150
FEATURE [Part::FeaturePython] Structure375  label="V15x40 V206"  # Arch/BIM 7 (typed FeaturePython)
  FaceMaker = 0
  Height = 400
  HorizontalArea = 445500
  IfcData = attributes={"GlobalId": {"name": "GlobalId", "type": "IfcGloballyUniqueId", "is_enum": false, "enum_values": []}, "Description": {"... (+475 chars omitted),+1 more (map truncated)
  IfcType = 7
  Length = 2970
  MoveBase = false
  MoveWithHost = false
  Nodes = (2) [(-1.72563e-31,-1.42109e-15,-7.77156e-16),(2970,-1.42109e-15,-7.77156e-16)]
  NodesOffset = 0
  Normal = (0,0,0)
  PerimeterLength = 6240
  Placement = pos=(10685,100,11800) rot=(0,0,1;0rad)
  PredefinedType = 0
  VerticalArea = 2.496e+06
  Width = 150
FEATURE [Part::FeaturePython] Structure376  label="V15x40 V207"  # Arch/BIM 7 (typed FeaturePython)
  FaceMaker = 0
  Height = 400
  HorizontalArea = 465000
  IfcData = attributes={"GlobalId": {"name": "GlobalId", "type": "IfcGloballyUniqueId", "is_enum": false, "enum_values": []}, "Description": {"... (+475 chars omitted),+1 more (map truncated)
  IfcType = 7
  Length = 3100
  MoveBase = false
  MoveWithHost = false
  Nodes = (2) [(-1.72563e-31,-1.42109e-15,-7.77156e-16),(3100,-1.42109e-15,-7.77156e-16)]
  NodesOffset = 0
  Normal = (0,0,0)
  PerimeterLength = 6500
  Placement = pos=(6160,3275,11800) rot=(0,0,-1;1.5708rad)
  PredefinedType = 0
  VerticalArea = 2.6e+06
  Width = 150
FEATURE [Part::FeaturePython] Structure377  label="V15x40 V208"  # Arch/BIM 7 (typed FeaturePython)
  FaceMaker = 0
  Height = 400
  HorizontalArea = 471000
  IfcData = attributes={"GlobalId": {"name": "GlobalId", "type": "IfcGloballyUniqueId", "is_enum": false, "enum_values": []}, "Description": {"... (+475 chars omitted),+1 more (map truncated)
  IfcType = 7
  Length = 3140
  MoveBase = false
  MoveWithHost = false
  Nodes = (2) [(-1.72563e-31,-1.42109e-15,-7.77156e-16),(3140,-1.42109e-15,-7.77156e-16)]
  NodesOffset = 0
  Normal = (0,0,0)
  PerimeterLength = 6580
  Placement = pos=(6160,6565,11800) rot=(0,0,-1;1.5708rad)
  PredefinedType = 0
  VerticalArea = 2.632e+06
  Width = 150
FEATURE [Part::FeaturePython] Structure378  label="V15x40 V209"  # Arch/BIM 7 (typed FeaturePython)
  FaceMaker = 0
  Height = 400
  HorizontalArea = 466500
  IfcData = attributes={"GlobalId": {"name": "GlobalId", "type": "IfcGloballyUniqueId", "is_enum": false, "enum_values": []}, "Description": {"... (+475 chars omitted),+1 more (map truncated)
  IfcType = 7
  Length = 3110
  MoveBase = false
  MoveWithHost = false
  Nodes = (2) [(-1.72563e-31,-1.42109e-15,-7.77156e-16),(3110,-1.42109e-15,-7.77156e-16)]
  NodesOffset = 0
  Normal = (0,0,0)
  PerimeterLength = 6520
  Placement = pos=(6160,9825,11800) rot=(0,0,-1;1.5708rad)
  PredefinedType = 0
  VerticalArea = 2.608e+06
  Width = 150
FEATURE [Part::FeaturePython] Structure379  label="V15x40 V210"  # Arch/BIM 7 (typed FeaturePython)
  FaceMaker = 0
  Height = 400
  HorizontalArea = 457500
  IfcData = attributes={"GlobalId": {"name": "GlobalId", "type": "IfcGloballyUniqueId", "is_enum": false, "enum_values": []}, "Description": {"... (+475 chars omitted),+1 more (map truncated)
  IfcType = 7
  Length = 3050
  MoveBase = false
  MoveWithHost = false
  Nodes = (2) [(-1.72563e-31,-1.42109e-15,-7.77156e-16),(3050,-1.42109e-15,-7.77156e-16)]
  NodesOffset = 0
  Normal = (0,0,0)
  PerimeterLength = 6400
  Placement = pos=(9010,3225,11800) rot=(0,0,-1;1.5708rad)
  PredefinedType = 0
  VerticalArea = 2.56e+06
  Width = 150
FEATURE [Part::FeaturePython] Structure380  label="V15x40 V211"  # Arch/BIM 7 (typed FeaturePython)
  FaceMaker = 0
  Height = 400
  HorizontalArea = 456000
  IfcData = attributes={"GlobalId": {"name": "GlobalId", "type": "IfcGloballyUniqueId", "is_enum": false, "enum_values": []}, "Description": {"... (+475 chars omitted),+1 more (map truncated)
  IfcType = 7
  Length = 3040
  MoveBase = false
  MoveWithHost = false
  Nodes = (2) [(-1.72563e-31,-1.42109e-15,-7.77156e-16),(3040,-1.42109e-15,-7.77156e-16)]
  NodesOffset = 0
  Normal = (0,0,0)
  PerimeterLength = 6380
  Placement = pos=(9010,6515,11800) rot=(0,0,-1;1.5708rad)
  PredefinedType = 0
  VerticalArea = 2.552e+06
  Width = 150
FEATURE [Part::FeaturePython] Structure381  label="V15x40 V212"  # Arch/BIM 7 (typed FeaturePython)
  FaceMaker = 0
  Height = 400
  HorizontalArea = 459000
  IfcData = attributes={"GlobalId": {"name": "GlobalId", "type": "IfcGloballyUniqueId", "is_enum": false, "enum_values": []}, "Description": {"... (+475 chars omitted),+1 more (map truncated)
  IfcType = 7
  Length = 3060
  MoveBase = false
  MoveWithHost = false
  Nodes = (2) [(-1.72563e-31,-1.42109e-15,-7.77156e-16),(3060,-1.42109e-15,-7.77156e-16)]
  NodesOffset = 0
  Normal = (0,0,0)
  PerimeterLength = 6420
  Placement = pos=(9010,9825,11800) rot=(0,0,-1;1.5708rad)
  PredefinedType = 0
  VerticalArea = 2.568e+06
  Width = 150
FEATURE [Part::FeaturePython] Structure382  label="V15x40 V213"  # Arch/BIM 7 (typed FeaturePython)
  FaceMaker = 0
  Height = 400
  HorizontalArea = 457500
  IfcData = attributes={"GlobalId": {"name": "GlobalId", "type": "IfcGloballyUniqueId", "is_enum": false, "enum_values": []}, "Description": {"... (+475 chars omitted),+1 more (map truncated)
  IfcType = 7
  Length = 3050
  MoveBase = false
  MoveWithHost = false
  Nodes = (2) [(-1.72563e-31,-1.42109e-15,-7.77156e-16),(3050,-1.42109e-15,-7.77156e-16)]
  NodesOffset = 0
  Normal = (0,0,0)
  PerimeterLength = 6400
  Placement = pos=(10560,3225,11800) rot=(0,0,-1;1.5708rad)
  PredefinedType = 0
  VerticalArea = 2.56e+06
  Width = 150
FEATURE [Part::FeaturePython] Structure383  label="V15x40 V214"  # Arch/BIM 7 (typed FeaturePython)
  FaceMaker = 0
  Height = 400
  HorizontalArea = 363000
  IfcData = attributes={"GlobalId": {"name": "GlobalId", "type": "IfcGloballyUniqueId", "is_enum": false, "enum_values": []}, "Description": {"... (+475 chars omitted),+1 more (map truncated)
  IfcType = 7
  Length = 2420
  MoveBase = false
  MoveWithHost = false
  Nodes = (2) [(-1.72563e-31,-1.42109e-15,-7.77156e-16),(2420,-1.42109e-15,-7.77156e-16)]
  NodesOffset = 0
  Normal = (0,0,0)
  PerimeterLength = 5140
  Placement = pos=(10560,3475,11800) rot=(0,0,1;1.5708rad)
  PredefinedType = 0
  VerticalArea = 2056000
  Width = 150
FEATURE [Part::FeaturePython] Structure384  label="V15x40 V215"  # Arch/BIM 7 (typed FeaturePython)
  FaceMaker = 0
  Height = 400
  HorizontalArea = 207000
  IfcData = attributes={"GlobalId": {"name": "GlobalId", "type": "IfcGloballyUniqueId", "is_enum": false, "enum_values": []}, "Description": {"... (+475 chars omitted),+1 more (map truncated)
  IfcType = 7
  Length = 1380
  MoveBase = false
  MoveWithHost = false
  Nodes = (2) [(-1.72563e-31,-1.42109e-15,-7.77156e-16),(1380,-1.42109e-15,-7.77156e-16)]
  NodesOffset = 0
  Normal = (0,0,0)
  PerimeterLength = 3060
  Placement = pos=(10560,8445,11800) rot=(0,0,1;1.5708rad)
  PredefinedType = 0
  VerticalArea = 1224000
  Width = 150
FEATURE [Part::FeaturePython] Structure385  label="V15x40 V216"  # Arch/BIM 7 (typed FeaturePython)
  FaceMaker = 0
  Height = 400
  HorizontalArea = 207000
  IfcData = attributes={"GlobalId": {"name": "GlobalId", "type": "IfcGloballyUniqueId", "is_enum": false, "enum_values": []}, "Description": {"... (+475 chars omitted),+1 more (map truncated)
  IfcType = 7
  Length = 1380
  MoveBase = false
  MoveWithHost = false
  Nodes = (2) [(-1.72563e-31,-1.42109e-15,-7.77156e-16),(1380,-1.42109e-15,-7.77156e-16)]
  NodesOffset = 0
  Normal = (0,0,0)
  PerimeterLength = 3060
  Placement = pos=(12010,9825,11800) rot=(0,0,-1;1.5708rad)
  PredefinedType = 0
  VerticalArea = 1224000
  Width = 150
FEATURE [Part::FeaturePython] Structure386  label="V20x40 V148"  # Arch/BIM 7 (typed FeaturePython)
  FaceMaker = 0
  Height = 400
  HorizontalArea = 615000
  IfcData = attributes={"GlobalId": {"name": "GlobalId", "type": "IfcGloballyUniqueId", "is_enum": false, "enum_values": []}, "Description": {"... (+475 chars omitted),+1 more (map truncated)
  IfcType = 7
  Length = 3075
  MoveBase = false
  MoveWithHost = false
  Nodes = (2) [(-1.72563e-31,0,-7.77156e-16),(3075,0,-7.77156e-16)]
  NodesOffset = 0
  Normal = (0,0,0)
  PerimeterLength = 6550
  Placement = pos=(1930,3250,11800) rot=(0,0,-1;1.5708rad)
  PredefinedType = 0
  VerticalArea = 2.62e+06
  Width = 200
FEATURE [Part::FeaturePython] Structure387  label="V20x40 V149"  # Arch/BIM 7 (typed FeaturePython)
  FaceMaker = 0
  Height = 400
  HorizontalArea = 618000
  IfcData = attributes={"GlobalId": {"name": "GlobalId", "type": "IfcGloballyUniqueId", "is_enum": false, "enum_values": []}, "Description": {"... (+475 chars omitted),+1 more (map truncated)
  IfcType = 7
  Length = 3090
  MoveBase = false
  MoveWithHost = false
  Nodes = (2) [(-1.72563e-31,0,-7.77156e-16),(3090,0,-7.77156e-16)]
  NodesOffset = 0
  Normal = (0,0,0)
  PerimeterLength = 6580
  Placement = pos=(1930,6540,11800) rot=(0,0,-1;1.5708rad)
  PredefinedType = 0
  VerticalArea = 2.632e+06
  Width = 200
FEATURE [Part::FeaturePython] Structure388  label="V20x40 V150"  # Arch/BIM 7 (typed FeaturePython)
  FaceMaker = 0
  Height = 400
  HorizontalArea = 617000
  IfcData = attributes={"GlobalId": {"name": "GlobalId", "type": "IfcGloballyUniqueId", "is_enum": false, "enum_values": []}, "Description": {"... (+475 chars omitted),+1 more (map truncated)
  IfcType = 7
  Length = 3085
  MoveBase = false
  MoveWithHost = false
  Nodes = (2) [(-1.72563e-31,0,-7.77156e-16),(3085,0,-7.77156e-16)]
  NodesOffset = 0
  Normal = (0,0,0)
  PerimeterLength = 6570
  Placement = pos=(1930,9825,11800) rot=(0,0,-1;1.5708rad)
  PredefinedType = 0
  VerticalArea = 2.628e+06
  Width = 200
FEATURE [Part::FeaturePython] Structure389  label="V20x40 V151"  # Arch/BIM 7 (typed FeaturePython)
  FaceMaker = 0
  Height = 400
  HorizontalArea = 635000
  IfcData = attributes={"GlobalId": {"name": "GlobalId", "type": "IfcGloballyUniqueId", "is_enum": false, "enum_values": []}, "Description": {"... (+475 chars omitted),+1 more (map truncated)
  IfcType = 7
  Length = 3175
  MoveBase = false
  MoveWithHost = false
  Nodes = (2) [(-1.72563e-31,0,-7.77156e-16),(3175,0,-7.77156e-16)]
  NodesOffset = 0
  Normal = (0,0,0)
  PerimeterLength = 6750
  Placement = pos=(13780,175,11800) rot=(0,0,1;1.5708rad)
  PredefinedType = 0
  VerticalArea = 2.7e+06
  Width = 200
FEATURE [Part::FeaturePython] Structure390  label="V20x40 V152"  # Arch/BIM 7 (typed FeaturePython)
  FaceMaker = 0
  Height = 400
  HorizontalArea = 509000
  IfcData = attributes={"GlobalId": {"name": "GlobalId", "type": "IfcGloballyUniqueId", "is_enum": false, "enum_values": []}, "Description": {"... (+475 chars omitted),+1 more (map truncated)
  IfcType = 7
  Length = 2545
  MoveBase = false
  MoveWithHost = false
  Nodes = (2) [(-1.72563e-31,0,-7.77156e-16),(2545,0,-7.77156e-16)]
  NodesOffset = 0
  Normal = (0,0,0)
  PerimeterLength = 5490
  Placement = pos=(13780,3350,11800) rot=(0,0,1;1.5708rad)
  PredefinedType = 0
  VerticalArea = 2196000
  Width = 200
FEATURE [Part::FeaturePython] Structure391  label="V20x40 V153"  # Arch/BIM 7 (typed FeaturePython)
  FaceMaker = 0
  Height = 400
  HorizontalArea = 756000
  IfcData = attributes={"GlobalId": {"name": "GlobalId", "type": "IfcGloballyUniqueId", "is_enum": false, "enum_values": []}, "Description": {"... (+475 chars omitted),+1 more (map truncated)
  IfcType = 7
  Length = 3780
  MoveBase = false
  MoveWithHost = false
  Nodes = (2) [(-1.72563e-31,0,-7.77156e-16),(3780,0,-7.77156e-16)]
  NodesOffset = 0
  Normal = (0,0,0)
  PerimeterLength = 7960
  Placement = pos=(15210,6045,11800) rot=(0,0,1;1.5708rad)
  PredefinedType = 0
  VerticalArea = 3.184e+06
  Width = 200
FEATURE [App::GeometryPython] BuildingPart022  label="Vigas sobre P3"  # Arch/BIM 172 (typed FeaturePython)
  Area = 0
  Group = -> [Structure354,Structure355,Structure356,Structure357,Structure358,Structure359,Structure360,Structure361,Structure362,Structure363,Structure364,Structure365,Structure366,Structure367,Structure368,Structure369,Structure370,Structure371,Structure372,Structure373,Structure374,Structure375,Structure376,Structure377,Structure378,Structure379,Structure380,Structure381,Structure382,Structure383,+8 more]
  Height = 0
  HeightPropagate = true
  IfcData = attributes={"GlobalId": {"name": "GlobalId", "type": "IfcGloballyUniqueId", "is_enum": false, "enum_values": []}, "Description": {"... (+484 chars omitted),+1 more (map truncated)
  IfcType = 172
  LevelOffset = 0
  PredefinedType = 0
FEATURE [App::GeometryPython] BuildingPart019  label="Piso 3"  # Arch/BIM 172 (typed FeaturePython)
  Area = 24900000
  Group = -> [BuildingPart020,BuildingPart021,Wall004,BuildingPart022]
  Height = 0
  HeightPropagate = true
  IfcData = attributes={"GlobalId": {"name": "GlobalId", "type": "IfcGloballyUniqueId", "is_enum": false, "enum_values": []}, "Description": {"... (+484 chars omitted),+1 more (map truncated)
  IfcType = 172
  LevelOffset = 0
  Placement = pos=(0,0,9000) rot=(0,0,1;0rad)
  PredefinedType = 0
FEATURE [App::GeometryPython] BuildingPart024  label="Sobre Terraza"  # Arch/BIM 172 (typed FeaturePython)
  Area = 0
  Height = 0
  HeightPropagate = true
  IfcData = attributes={"GlobalId": {"name": "GlobalId", "type": "IfcGloballyUniqueId", "is_enum": false, "enum_values": []}, "Description": {"... (+484 chars omitted),+1 more (map truncated)
  IfcType = 172
  LevelOffset = 0
  PredefinedType = 0
FEATURE [Part::FeaturePython] Structure392  label="Column"  # Arch/BIM 24 (typed FeaturePython)
  FaceMaker = 0
  Height = 3000
  HorizontalArea = 22500
  IfcData = attributes={"GlobalId": {"name": "GlobalId", "type": "IfcGloballyUniqueId", "is_enum": false, "enum_values": []}, "Description": {"... (+438 chars omitted),+1 more (map truncated)
  IfcType = 24
  Length = 150
  MoveBase = false
  MoveWithHost = false
  Nodes = (2) [(2.77556e-16,7.57912e-16,0),(2.77556e-16,7.57912e-16,3000)]
  NodesOffset = 0
  Normal = (0,0,0)
  PerimeterLength = 600
  Placement = pos=(15210,9900,12000) rot=(0,0,1;0rad)
  PredefinedType = 0
  VerticalArea = 1800000
  Width = 150
FEATURE [Part::FeaturePython] Structure393  label="Column001"  # Arch/BIM 24 (typed FeaturePython)
  FaceMaker = 0
  Height = 3000
  HorizontalArea = 22500
  IfcData = attributes={"GlobalId": {"name": "GlobalId", "type": "IfcGloballyUniqueId", "is_enum": false, "enum_values": []}, "Description": {"... (+438 chars omitted),+1 more (map truncated)
  IfcType = 24
  Length = 150
  MoveBase = false
  MoveWithHost = false
  Nodes = (2) [(2.77556e-16,7.57912e-16,0),(2.77556e-16,7.57912e-16,3000)]
  NodesOffset = 0
  Normal = (0,0,0)
  PerimeterLength = 600
  Placement = pos=(10560,9900,12000) rot=(0,0,1;0rad)
  PredefinedType = 0
  VerticalArea = 1800000
  Width = 150
FEATURE [Part::FeaturePython] Structure394  label="Column002"  # Arch/BIM 24 (typed FeaturePython)
  FaceMaker = 0
  Height = 3000
  HorizontalArea = 22500
  IfcData = attributes={"GlobalId": {"name": "GlobalId", "type": "IfcGloballyUniqueId", "is_enum": false, "enum_values": []}, "Description": {"... (+438 chars omitted),+1 more (map truncated)
  IfcType = 24
  Length = 150
  MoveBase = false
  MoveWithHost = false
  Nodes = (2) [(2.77556e-16,7.57912e-16,0),(2.77556e-16,7.57912e-16,3000)]
  NodesOffset = 0
  Normal = (0,0,0)
  PerimeterLength = 600
  Placement = pos=(15210,5970,12000) rot=(0,0,1;0rad)
  PredefinedType = 0
  VerticalArea = 1800000
  Width = 150
FEATURE [Part::FeaturePython] Structure395  label="Column003"  # Arch/BIM 24 (typed FeaturePython)
  FaceMaker = 0
  Height = 3000
  HorizontalArea = 22500
  IfcData = attributes={"GlobalId": {"name": "GlobalId", "type": "IfcGloballyUniqueId", "is_enum": false, "enum_values": []}, "Description": {"... (+438 chars omitted),+1 more (map truncated)
  IfcType = 24
  Length = 150
  MoveBase = false
  MoveWithHost = false
  Nodes = (2) [(2.77556e-16,7.57912e-16,0),(2.77556e-16,7.57912e-16,3000)]
  NodesOffset = 0
  Normal = (0,0,0)
  PerimeterLength = 600
  Placement = pos=(10560,5970,12000) rot=(0,0,1;0rad)
  PredefinedType = 0
  VerticalArea = 1800000
  Width = 150
FEATURE [Part::FeaturePython] Structure396  label="Beam042"  # Arch/BIM 7 (typed FeaturePython)
  FaceMaker = 0
  Height = 300
  HorizontalArea = 675000
  IfcData = attributes={"GlobalId": {"name": "GlobalId", "type": "IfcGloballyUniqueId", "is_enum": false, "enum_values": []}, "Description": {"... (+475 chars omitted),+1 more (map truncated)
  IfcType = 7
  Length = 4500
  MoveBase = false
  MoveWithHost = false
  Nodes = (2) [(1.2326e-31,-7.57912e-16,5.55112e-16),(4500,-7.57912e-16,5.55112e-16)]
  NodesOffset = 0
  Normal = (0,0,0)
  PerimeterLength = 9300
  Placement = pos=(10635,9900,14850) rot=(0,0,1;0rad)
  PredefinedType = 0
  VerticalArea = 2790000
  Width = 150
FEATURE [Part::FeaturePython] Structure397  label="Beam043"  # Arch/BIM 7 (typed FeaturePython)
  FaceMaker = 0
  Height = 300
  HorizontalArea = 567000
  IfcData = attributes={"GlobalId": {"name": "GlobalId", "type": "IfcGloballyUniqueId", "is_enum": false, "enum_values": []}, "Description": {"... (+475 chars omitted),+1 more (map truncated)
  IfcType = 7
  Length = 3780
  MoveBase = false
  MoveWithHost = false
  Nodes = (2) [(1.2326e-31,-7.57912e-16,5.55112e-16),(3780,-7.57912e-16,5.55112e-16)]
  NodesOffset = 0
  Normal = (0,0,0)
  PerimeterLength = 7860
  Placement = pos=(15210,9825,14850) rot=(0,0,-1;1.5708rad)
  PredefinedType = 0
  VerticalArea = 2.358e+06
  Width = 150
FEATURE [Part::FeaturePython] Structure398  label="Beam044"  # Arch/BIM 7 (typed FeaturePython)
  FaceMaker = 0
  Height = 300
  HorizontalArea = 675000
  IfcData = attributes={"GlobalId": {"name": "GlobalId", "type": "IfcGloballyUniqueId", "is_enum": false, "enum_values": []}, "Description": {"... (+475 chars omitted),+1 more (map truncated)
  IfcType = 7
  Length = 4500
  MoveBase = false
  MoveWithHost = false
  Nodes = (2) [(1.2326e-31,-7.57912e-16,5.55112e-16),(4500,-7.57912e-16,5.55112e-16)]
  NodesOffset = 0
  Normal = (0,0,0)
  PerimeterLength = 9300
  Placement = pos=(15135,5970,14850) rot=(0,0,1;3.14159rad)
  PredefinedType = 0
  VerticalArea = 2790000
  Width = 150
FEATURE [Part::FeaturePython] Structure399  label="Beam045"  # Arch/BIM 7 (typed FeaturePython)
  FaceMaker = 0
  Height = 300
  HorizontalArea = 567000
  IfcData = attributes={"GlobalId": {"name": "GlobalId", "type": "IfcGloballyUniqueId", "is_enum": false, "enum_values": []}, "Description": {"... (+475 chars omitted),+1 more (map truncated)
  IfcType = 7
  Length = 3780
  MoveBase = false
  MoveWithHost = false
  Nodes = (2) [(1.2326e-31,-7.57912e-16,5.55112e-16),(3780,-7.57912e-16,5.55112e-16)]
  NodesOffset = 0
  Normal = (0,0,0)
  PerimeterLength = 7860
  Placement = pos=(10560,6045,14850) rot=(0,0,1;1.5708rad)
  PredefinedType = 0
  VerticalArea = 2.358e+06
  Width = 150
FEATURE [App::GeometryPython] BuildingPart025  label="Vigas sobre Terraza"  # Arch/BIM 172 (typed FeaturePython)
  Area = 0
  Group = -> [Structure396,Structure397,Structure398,Structure399]
  Height = 0
  HeightPropagate = true
  IfcData = attributes={"GlobalId": {"name": "GlobalId", "type": "IfcGloballyUniqueId", "is_enum": false, "enum_values": []}, "Description": {"... (+484 chars omitted),+1 more (map truncated)
  IfcType = 172
  LevelOffset = 0
  Placement = pos=(0,0,12000) rot=(0,0,1;0rad)
  PredefinedType = 0
FEATURE [App::GeometryPython] BuildingPart026  label="Columnas Terraza"  # Arch/BIM 172 (typed FeaturePython)
  Area = 0
  Group = -> [Structure392,Structure393,Structure394,Structure395]
  Height = 0
  HeightPropagate = true
  IfcData = attributes={"GlobalId": {"name": "GlobalId", "type": "IfcGloballyUniqueId", "is_enum": false, "enum_values": []}, "Description": {"... (+484 chars omitted),+1 more (map truncated)
  IfcType = 172
  LevelOffset = 0
  Placement = pos=(0,0,12000) rot=(0,0,1;0rad)
  PredefinedType = 0
FEATURE [Part::Part2DObjectPython] Rectangle021  # Draft 2D object (typed FeaturePython)
  Area = 1.701e+07
  ChamferSize = 0
  Columns = 1
  FilletRadius = 0
  Height = 3780
  Length = 4500
  MakeFace = true
  Placement = pos=(10635,6045,15000) rot=(0,0,1;0rad)
  Rows = 1
FEATURE [Part::FeaturePython] Structure400  label="Structure"  # Arch/BIM 172 (typed FeaturePython)
  Base = -> Rectangle021
  FaceMaker = 0
  Height = 150
  HorizontalArea = 1.701e+07
  IfcData = attributes={"GlobalId": {"name": "GlobalId", "type": "IfcGloballyUniqueId", "is_enum": false, "enum_values": []}, "Description": {"... (+484 chars omitted),+1 more (map truncated)
  IfcType = 172
  Length = 0
  MoveBase = false
  MoveWithHost = false
  Nodes = (2) [(12885,7935,15000),(12885,7935,14850)]
  NodesOffset = 0
  Normal = (0,0,-1)
  PerimeterLength = 16560
  PredefinedType = 0
  VerticalArea = 2484000
  Width = 150
FEATURE [App::GeometryPython] BuildingPart027  label="Losas sobre Terraza"  # Arch/BIM 172 (typed FeaturePython)
  Area = 0
  Group = -> [Structure400]
  Height = 0
  HeightPropagate = true
  IfcData = attributes={"GlobalId": {"name": "GlobalId", "type": "IfcGloballyUniqueId", "is_enum": false, "enum_values": []}, "Description": {"... (+484 chars omitted),+1 more (map truncated)
  IfcType = 172
  LevelOffset = 0
  Placement = pos=(0,0,12000) rot=(0,0,1;0rad)
  PredefinedType = 0
FEATURE [App::GeometryPython] BuildingPart023  label="Terraza"  # Arch/BIM 172 (typed FeaturePython)
  Area = 0
  Group = -> [BuildingPart026,BuildingPart025,BuildingPart027]
  Height = 0
  HeightPropagate = true
  IfcData = attributes={"GlobalId": {"name": "GlobalId", "type": "IfcGloballyUniqueId", "is_enum": false, "enum_values": []}, "Description": {"... (+484 chars omitted),+1 more (map truncated)
  IfcType = 172
  LevelOffset = 0
  Placement = pos=(0,0,12000) rot=(0,0,1;0rad)
  PredefinedType = 0
FEATURE [Part::FeaturePython] Axis004  label="Horizontal corta"  # WARN: FeaturePython — macro-defined, semantics opaque (R4)
  Angles = [0,0,0,0,0,0]
  Distances = [100,3250,2620,670,1730,1530]
  Length = 18000
  Placement = pos=(17000,1.077e-12,0) rot=(0,0,1;1.5708rad)
FEATURE [App::DocumentObjectGroup] Group  label="Rejillas"
  Group = -> [Axis002,Axis,Axis004]
FEATURE [App::MaterialObjectPython] Material  label="Hormigon Armado"  # material (typed FeaturePython)
  Description = HA
  Material = Description=HA,DiffuseColor=(0.8500000238418579, 0.8500000238418579, 0.8500000238418579),Name=Hormigon Armado,+2 more (map truncated)
  Transparency = 0
FEATURE [Part::FeaturePython] Structure  label="CAB PIL 1"  # Arch/BIM 77 (typed FeaturePython)
  Base = -> Rectangle002
  Description = Pilote rectangular
  FaceMaker = 0
  Height = 700
  HorizontalArea = 490000
  IfcData = attributes={"GlobalId": {"name": "GlobalId", "type": "IfcGloballyUniqueId", "is_enum": false, "enum_values": []}, "Description": {"... (+547 chars omitted),+1 more (map truncated)
  IfcType = 77
  Length = 0
  Material = -> Material
  MoveBase = false
  MoveWithHost = false
  Nodes = (2) [(15210,9900,0),(15210,9900,-700)]
  NodesOffset = 0
  Normal = (0,0,-1)
  PerimeterLength = 2800
  Placement = pos=(-13280,1.819e-12,-500) rot=(0,0,1;0rad)
  PredefinedType = 3
  Tag = B1
  VerticalArea = 1960000
  Width = 0
  expr: Height = <<Estructura>>.CabEsp
FEATURE [Part::FeaturePython] Structure001  label="PIL 1"  # Arch/BIM 96 (typed FeaturePython)
  Base = -> Circle
  ConstructionType = 0
  Description = Pilote circular
  FaceMaker = 0
  Height = 8000
  HorizontalArea = 196350
  IfcData = attributes={"GlobalId": {"name": "GlobalId", "type": "IfcGloballyUniqueId", "is_enum": false, "enum_values": []}, "Description": {"... (+752 chars omitted),+1 more (map truncated)
  IfcType = 96
  Length = 0
  Material = -> Material
  MoveBase = false
  MoveWithHost = false
  Nodes = (2) [(15210,9900,0),(15210,9900,-8000)]
  NodesOffset = 0
  Normal = (0,0,-1)
  PerimeterLength = 1570.8
  Placement = pos=(-13280,1.819e-12,-1200) rot=(0,0,1;0rad)
  PredefinedType = 5
  VerticalArea = 1.25664e+07
  Width = 100
  expr: Height = <<Estructura>>.PilProf
FEATURE [Part::FeaturePython] Structure002  label="CAB PIL 6"  # Arch/BIM 172 (typed FeaturePython)
  CloneOf = -> Structure
  FaceMaker = 0
  Height = 700
  HorizontalArea = 490000
  IfcData = attributes={"GlobalId": {"name": "GlobalId", "type": "IfcGloballyUniqueId", "is_enum": false, "enum_values": []}, "Description": {"... (+484 chars omitted),+1 more (map truncated)
  IfcType = 172
  Length = 0
  Material = -> Material
  MoveBase = false
  MoveWithHost = false
  Nodes = (2) [(15210,9900,0),(15210,9900,-700)]
  NodesOffset = 0
  Normal = (0,0,0)
  PerimeterLength = 2800
  Placement = pos=(-13280,-3260,-500) rot=(0,0,1;0rad)
  PredefinedType = 0
  VerticalArea = 1960000
  Width = 0
FEATURE [Part::FeaturePython] Structure003  label="PIL 6"  # Arch/BIM 172 (typed FeaturePython)
  CloneOf = -> Structure001
  FaceMaker = 0
  Height = 8000
  HorizontalArea = 196350
  IfcData = attributes={"GlobalId": {"name": "GlobalId", "type": "IfcGloballyUniqueId", "is_enum": false, "enum_values": []}, "Description": {"... (+484 chars omitted),+1 more (map truncated)
  IfcType = 172
  Length = 0
  Material = -> Material
  MoveBase = false
  MoveWithHost = false
  Nodes = (2) [(15210,9900,0),(15210,9900,-8000)]
  NodesOffset = 0
  Normal = (0,0,0)
  PerimeterLength = 1570.8
  Placement = pos=(-13280,-3260,-1200) rot=(0,0,1;0rad)
  PredefinedType = 0
  VerticalArea = 1.25664e+07
  Width = 100
FEATURE [Part::FeaturePython] Structure004  label="CAB PIL 11"  # Arch/BIM 172 (typed FeaturePython)
  CloneOf = -> Structure
  FaceMaker = 0
  Height = 700
  HorizontalArea = 490000
  IfcData = attributes={"GlobalId": {"name": "GlobalId", "type": "IfcGloballyUniqueId", "is_enum": false, "enum_values": []}, "Description": {"... (+484 chars omitted),+1 more (map truncated)
  IfcType = 172
  Length = 0
  Material = -> Material
  MoveBase = false
  MoveWithHost = false
  Nodes = (2) [(15210,9900,0),(15210,9900,-700)]
  NodesOffset = 0
  Normal = (0,0,0)
  PerimeterLength = 2800
  Placement = pos=(-13280,-6550,-500) rot=(0,0,1;0rad)
  PredefinedType = 0
  VerticalArea = 1960000
  Width = 0
FEATURE [Part::FeaturePython] Structure005  label="PIL 11"  # Arch/BIM 172 (typed FeaturePython)
  CloneOf = -> Structure001
  FaceMaker = 0
  Height = 8000
  HorizontalArea = 196350
  IfcData = attributes={"GlobalId": {"name": "GlobalId", "type": "IfcGloballyUniqueId", "is_enum": false, "enum_values": []}, "Description": {"... (+484 chars omitted),+1 more (map truncated)
  IfcType = 172
  Length = 0
  Material = -> Material
  MoveBase = false
  MoveWithHost = false
  Nodes = (2) [(15210,9900,0),(15210,9900,-8000)]
  NodesOffset = 0
  Normal = (0,0,0)
  PerimeterLength = 1570.8
  Placement = pos=(-13280,-6550,-1200) rot=(0,0,1;0rad)
  PredefinedType = 0
  VerticalArea = 1.25664e+07
  Width = 100
FEATURE [Part::FeaturePython] Structure006  label="CAB PIL 2"  # Arch/BIM 172 (typed FeaturePython)
  CloneOf = -> Structure
  FaceMaker = 0
  Height = 700
  HorizontalArea = 490000
  IfcData = attributes={"GlobalId": {"name": "GlobalId", "type": "IfcGloballyUniqueId", "is_enum": false, "enum_values": []}, "Description": {"... (+484 chars omitted),+1 more (map truncated)
  IfcType = 172
  Length = 0
  Material = -> Material
  MoveBase = false
  MoveWithHost = false
  Nodes = (2) [(15210,9900,0),(15210,9900,-700)]
  NodesOffset = 0
  Normal = (0,0,0)
  PerimeterLength = 2800
  Placement = pos=(-9050,0,-500) rot=(0,0,1;0rad)
  PredefinedType = 0
  VerticalArea = 1960000
  Width = 0
FEATURE [Part::FeaturePython] Structure007  label="PIL 2"  # Arch/BIM 172 (typed FeaturePython)
  CloneOf = -> Structure001
  FaceMaker = 0
  Height = 8000
  HorizontalArea = 196350
  IfcData = attributes={"GlobalId": {"name": "GlobalId", "type": "IfcGloballyUniqueId", "is_enum": false, "enum_values": []}, "Description": {"... (+484 chars omitted),+1 more (map truncated)
  IfcType = 172
  Length = 0
  Material = -> Material
  MoveBase = false
  MoveWithHost = false
  Nodes = (2) [(15210,9900,0),(15210,9900,-8000)]
  NodesOffset = 0
  Normal = (0,0,0)
  PerimeterLength = 1570.8
  Placement = pos=(-9050,0,-1200) rot=(0,0,1;0rad)
  PredefinedType = 0
  VerticalArea = 1.25664e+07
  Width = 100
FEATURE [Part::FeaturePython] Structure008  label="CAB PIL 3"  # Arch/BIM 172 (typed FeaturePython)
  CloneOf = -> Structure
  FaceMaker = 0
  Height = 700
  HorizontalArea = 490000
  IfcData = attributes={"GlobalId": {"name": "GlobalId", "type": "IfcGloballyUniqueId", "is_enum": false, "enum_values": []}, "Description": {"... (+484 chars omitted),+1 more (map truncated)
  IfcType = 172
  Length = 0
  Material = -> Material
  MoveBase = false
  MoveWithHost = false
  Nodes = (2) [(15210,9900,0),(15210,9900,-700)]
  NodesOffset = 0
  Normal = (0,0,0)
  PerimeterLength = 2800
  Placement = pos=(-6200,0,-500) rot=(0,0,1;0rad)
  PredefinedType = 0
  VerticalArea = 1960000
  Width = 0
FEATURE [Part::FeaturePython] Structure009  label="PIL 3"  # Arch/BIM 172 (typed FeaturePython)
  CloneOf = -> Structure001
  FaceMaker = 0
  Height = 8000
  HorizontalArea = 196350
  IfcData = attributes={"GlobalId": {"name": "GlobalId", "type": "IfcGloballyUniqueId", "is_enum": false, "enum_values": []}, "Description": {"... (+484 chars omitted),+1 more (map truncated)
  IfcType = 172
  Length = 0
  Material = -> Material
  MoveBase = false
  MoveWithHost = false
  Nodes = (2) [(15210,9900,0),(15210,9900,-8000)]
  NodesOffset = 0
  Normal = (0,0,0)
  PerimeterLength = 1570.8
  Placement = pos=(-6200,0,-1200) rot=(0,0,1;0rad)
  PredefinedType = 0
  VerticalArea = 1.25664e+07
  Width = 100
FEATURE [Part::FeaturePython] Structure010  label="CAB PIL 4"  # Arch/BIM 172 (typed FeaturePython)
  CloneOf = -> Structure
  FaceMaker = 0
  Height = 700
  HorizontalArea = 490000
  IfcData = attributes={"GlobalId": {"name": "GlobalId", "type": "IfcGloballyUniqueId", "is_enum": false, "enum_values": []}, "Description": {"... (+484 chars omitted),+1 more (map truncated)
  IfcType = 172
  Length = 0
  Material = -> Material
  MoveBase = false
  MoveWithHost = false
  Nodes = (2) [(15210,9900,0),(15210,9900,-700)]
  NodesOffset = 0
  Normal = (0,0,0)
  PerimeterLength = 2800
  Placement = pos=(-3200,0,-500) rot=(0,0,1;0rad)
  PredefinedType = 0
  VerticalArea = 1960000
  Width = 0
FEATURE [Part::FeaturePython] Structure011  label="PIL 4"  # Arch/BIM 172 (typed FeaturePython)
  CloneOf = -> Structure001
  FaceMaker = 0
  Height = 8000
  HorizontalArea = 196350
  IfcData = attributes={"GlobalId": {"name": "GlobalId", "type": "IfcGloballyUniqueId", "is_enum": false, "enum_values": []}, "Description": {"... (+484 chars omitted),+1 more (map truncated)
  IfcType = 172
  Length = 0
  Material = -> Material
  MoveBase = false
  MoveWithHost = false
  Nodes = (2) [(15210,9900,0),(15210,9900,-8000)]
  NodesOffset = 0
  Normal = (0,0,0)
  PerimeterLength = 1570.8
  Placement = pos=(-3200,0,-1200) rot=(0,0,1;0rad)
  PredefinedType = 0
  VerticalArea = 1.25664e+07
  Width = 100
FEATURE [Part::FeaturePython] Structure012  label="CAB PIL 5"  # Arch/BIM 172 (typed FeaturePython)
  CloneOf = -> Structure
  FaceMaker = 0
  Height = 700
  HorizontalArea = 490000
  IfcData = attributes={"GlobalId": {"name": "GlobalId", "type": "IfcGloballyUniqueId", "is_enum": false, "enum_values": []}, "Description": {"... (+484 chars omitted),+1 more (map truncated)
  IfcType = 172
  Length = 0
  Material = -> Material
  MoveBase = false
  MoveWithHost = false
  Nodes = (2) [(15210,9900,0),(15210,9900,-700)]
  NodesOffset = 0
  Normal = (0,0,0)
  PerimeterLength = 2800
  Placement = pos=(-9.09e-13,0,-500) rot=(0,0,1;0rad)
  PredefinedType = 0
  VerticalArea = 1960000
  Width = 0
FEATURE [Part::FeaturePython] Structure013  label="PIL 5"  # Arch/BIM 172 (typed FeaturePython)
  CloneOf = -> Structure001
  FaceMaker = 0
  Height = 8000
  HorizontalArea = 196350
  IfcData = attributes={"GlobalId": {"name": "GlobalId", "type": "IfcGloballyUniqueId", "is_enum": false, "enum_values": []}, "Description": {"... (+484 chars omitted),+1 more (map truncated)
  IfcType = 172
  Length = 0
  Material = -> Material
  MoveBase = false
  MoveWithHost = false
  Nodes = (2) [(15210,9900,0),(15210,9900,-8000)]
  NodesOffset = 0
  Normal = (0,0,0)
  PerimeterLength = 1570.8
  Placement = pos=(-9.09e-13,0,-1200) rot=(0,0,1;0rad)
  PredefinedType = 0
  VerticalArea = 1.25664e+07
  Width = 100
FEATURE [Part::FeaturePython] Structure014  label="CAB PIL 7"  # Arch/BIM 172 (typed FeaturePython)
  CloneOf = -> Structure
  FaceMaker = 0
  Height = 700
  HorizontalArea = 490000
  IfcData = attributes={"GlobalId": {"name": "GlobalId", "type": "IfcGloballyUniqueId", "is_enum": false, "enum_values": []}, "Description": {"... (+484 chars omitted),+1 more (map truncated)
  IfcType = 172
  Length = 0
  Material = -> Material
  MoveBase = false
  MoveWithHost = false
  Nodes = (2) [(15210,9900,0),(15210,9900,-700)]
  NodesOffset = 0
  Normal = (0,0,0)
  PerimeterLength = 2800
  Placement = pos=(-9050,-3260,-500) rot=(0,0,1;0rad)
  PredefinedType = 0
  VerticalArea = 1960000
  Width = 0
FEATURE [Part::FeaturePython] Structure015  label="PIL 7"  # Arch/BIM 172 (typed FeaturePython)
  CloneOf = -> Structure001
  FaceMaker = 0
  Height = 8000
  HorizontalArea = 196350
  IfcData = attributes={"GlobalId": {"name": "GlobalId", "type": "IfcGloballyUniqueId", "is_enum": false, "enum_values": []}, "Description": {"... (+484 chars omitted),+1 more (map truncated)
  IfcType = 172
  Length = 0
  Material = -> Material
  MoveBase = false
  MoveWithHost = false
  Nodes = (2) [(15210,9900,0),(15210,9900,-8000)]
  NodesOffset = 0
  Normal = (0,0,0)
  PerimeterLength = 1570.8
  Placement = pos=(-9050,-3260,-1200) rot=(0,0,1;0rad)
  PredefinedType = 0
  VerticalArea = 1.25664e+07
  Width = 100
FEATURE [Part::FeaturePython] Structure016  label="CAB PIL 8"  # Arch/BIM 172 (typed FeaturePython)
  CloneOf = -> Structure
  FaceMaker = 0
  Height = 700
  HorizontalArea = 490000
  IfcData = attributes={"GlobalId": {"name": "GlobalId", "type": "IfcGloballyUniqueId", "is_enum": false, "enum_values": []}, "Description": {"... (+484 chars omitted),+1 more (map truncated)
  IfcType = 172
  Length = 0
  Material = -> Material
  MoveBase = false
  MoveWithHost = false
  Nodes = (2) [(15210,9900,0),(15210,9900,-700)]
  NodesOffset = 0
  Normal = (0,0,0)
  PerimeterLength = 2800
  Placement = pos=(-6200,-3260,-500) rot=(0,0,1;0rad)
  PredefinedType = 0
  VerticalArea = 1960000
  Width = 0
FEATURE [Part::FeaturePython] Structure017  label="PIL 8"  # Arch/BIM 172 (typed FeaturePython)
  CloneOf = -> Structure001
  FaceMaker = 0
  Height = 8000
  HorizontalArea = 196350
  IfcData = attributes={"GlobalId": {"name": "GlobalId", "type": "IfcGloballyUniqueId", "is_enum": false, "enum_values": []}, "Description": {"... (+484 chars omitted),+1 more (map truncated)
  IfcType = 172
  Length = 0
  Material = -> Material
  MoveBase = false
  MoveWithHost = false
  Nodes = (2) [(15210,9900,0),(15210,9900,-8000)]
  NodesOffset = 0
  Normal = (0,0,0)
  PerimeterLength = 1570.8
  Placement = pos=(-6200,-3260,-1200) rot=(0,0,1;0rad)
  PredefinedType = 0
  VerticalArea = 1.25664e+07
  Width = 100
FEATURE [Part::FeaturePython] Structure018  label="CAB PIL 9"  # Arch/BIM 172 (typed FeaturePython)
  CloneOf = -> Structure
  FaceMaker = 0
  Height = 700
  HorizontalArea = 490000
  IfcData = attributes={"GlobalId": {"name": "GlobalId", "type": "IfcGloballyUniqueId", "is_enum": false, "enum_values": []}, "Description": {"... (+484 chars omitted),+1 more (map truncated)
  IfcType = 172
  Length = 0
  Material = -> Material
  MoveBase = false
  MoveWithHost = false
  Nodes = (2) [(15210,9900,0),(15210,9900,-700)]
  NodesOffset = 0
  Normal = (0,0,0)
  PerimeterLength = 2800
  Placement = pos=(-1430,-3930,-500) rot=(0,0,1;0rad)
  PredefinedType = 0
  VerticalArea = 1960000
  Width = 0
FEATURE [Part::FeaturePython] Structure019  label="PIL 9"  # Arch/BIM 172 (typed FeaturePython)
  CloneOf = -> Structure001
  FaceMaker = 0
  Height = 8000
  HorizontalArea = 196350
  IfcData = attributes={"GlobalId": {"name": "GlobalId", "type": "IfcGloballyUniqueId", "is_enum": false, "enum_values": []}, "Description": {"... (+484 chars omitted),+1 more (map truncated)
  IfcType = 172
  Length = 0
  Material = -> Material
  MoveBase = false
  MoveWithHost = false
  Nodes = (2) [(15210,9900,0),(15210,9900,-8000)]
  NodesOffset = 0
  Normal = (0,0,0)
  PerimeterLength = 1570.8
  Placement = pos=(-1430,-3930,-1200) rot=(0,0,1;0rad)
  PredefinedType = 0
  VerticalArea = 1.25664e+07
  Width = 100
FEATURE [Part::FeaturePython] Structure020  label="CAB PIL 10"  # Arch/BIM 172 (typed FeaturePython)
  CloneOf = -> Structure
  FaceMaker = 0
  Height = 700
  HorizontalArea = 490000
  IfcData = attributes={"GlobalId": {"name": "GlobalId", "type": "IfcGloballyUniqueId", "is_enum": false, "enum_values": []}, "Description": {"... (+484 chars omitted),+1 more (map truncated)
  IfcType = 172
  Length = 0
  Material = -> Material
  MoveBase = false
  MoveWithHost = false
  Nodes = (2) [(15210,9900,0),(15210,9900,-700)]
  NodesOffset = 0
  Normal = (0,0,0)
  PerimeterLength = 2800
  Placement = pos=(-9.09e-13,-3930,-500) rot=(0,0,1;0rad)
  PredefinedType = 0
  VerticalArea = 1960000
  Width = 0
FEATURE [Part::FeaturePython] Structure021  label="PIL 10"  # Arch/BIM 172 (typed FeaturePython)
  CloneOf = -> Structure001
  FaceMaker = 0
  Height = 8000
  HorizontalArea = 196350
  IfcData = attributes={"GlobalId": {"name": "GlobalId", "type": "IfcGloballyUniqueId", "is_enum": false, "enum_values": []}, "Description": {"... (+484 chars omitted),+1 more (map truncated)
  IfcType = 172
  Length = 0
  Material = -> Material
  MoveBase = false
  MoveWithHost = false
  Nodes = (2) [(15210,9900,0),(15210,9900,-8000)]
  NodesOffset = 0
  Normal = (0,0,0)
  PerimeterLength = 1570.8
  Placement = pos=(-9.09e-13,-3930,-1200) rot=(0,0,1;0rad)
  PredefinedType = 0
  VerticalArea = 1.25664e+07
  Width = 100
FEATURE [Part::FeaturePython] Structure022  label="CAB PIL 12"  # Arch/BIM 172 (typed FeaturePython)
  CloneOf = -> Structure
  FaceMaker = 0
  Height = 700
  HorizontalArea = 490000
  IfcData = attributes={"GlobalId": {"name": "GlobalId", "type": "IfcGloballyUniqueId", "is_enum": false, "enum_values": []}, "Description": {"... (+484 chars omitted),+1 more (map truncated)
  IfcType = 172
  Length = 0
  Material = -> Material
  MoveBase = false
  MoveWithHost = false
  Nodes = (2) [(15210,9900,0),(15210,9900,-700)]
  NodesOffset = 0
  Normal = (0,0,0)
  PerimeterLength = 2800
  Placement = pos=(-9050,-6550,-500) rot=(0,0,1;0rad)
  PredefinedType = 0
  VerticalArea = 1960000
  Width = 0
FEATURE [Part::FeaturePython] Structure023  label="PIL 12"  # Arch/BIM 172 (typed FeaturePython)
  CloneOf = -> Structure001
  FaceMaker = 0
  Height = 8000
  HorizontalArea = 196350
  IfcData = attributes={"GlobalId": {"name": "GlobalId", "type": "IfcGloballyUniqueId", "is_enum": false, "enum_values": []}, "Description": {"... (+484 chars omitted),+1 more (map truncated)
  IfcType = 172
  Length = 0
  Material = -> Material
  MoveBase = false
  MoveWithHost = false
  Nodes = (2) [(15210,9900,0),(15210,9900,-8000)]
  NodesOffset = 0
  Normal = (0,0,0)
  PerimeterLength = 1570.8
  Placement = pos=(-9050,-6550,-1200) rot=(0,0,1;0rad)
  PredefinedType = 0
  VerticalArea = 1.25664e+07
  Width = 100
FEATURE [Part::FeaturePython] Structure024  label="CAB PIL 13"  # Arch/BIM 172 (typed FeaturePython)
  CloneOf = -> Structure
  FaceMaker = 0
  Height = 700
  HorizontalArea = 490000
  IfcData = attributes={"GlobalId": {"name": "GlobalId", "type": "IfcGloballyUniqueId", "is_enum": false, "enum_values": []}, "Description": {"... (+484 chars omitted),+1 more (map truncated)
  IfcType = 172
  Length = 0
  Material = -> Material
  MoveBase = false
  MoveWithHost = false
  Nodes = (2) [(15210,9900,0),(15210,9900,-700)]
  NodesOffset = 0
  Normal = (0,0,0)
  PerimeterLength = 2800
  Placement = pos=(-6200,-6550,-500) rot=(0,0,1;0rad)
  PredefinedType = 0
  VerticalArea = 1960000
  Width = 0
FEATURE [Part::FeaturePython] Structure025  label="PIL 13"  # Arch/BIM 172 (typed FeaturePython)
  CloneOf = -> Structure001
  FaceMaker = 0
  Height = 8000
  HorizontalArea = 196350
  IfcData = attributes={"GlobalId": {"name": "GlobalId", "type": "IfcGloballyUniqueId", "is_enum": false, "enum_values": []}, "Description": {"... (+484 chars omitted),+1 more (map truncated)
  IfcType = 172
  Length = 0
  Material = -> Material
  MoveBase = false
  MoveWithHost = false
  Nodes = (2) [(15210,9900,0),(15210,9900,-8000)]
  NodesOffset = 0
  Normal = (0,0,0)
  PerimeterLength = 1570.8
  Placement = pos=(-6200,-6550,-1200) rot=(0,0,1;0rad)
  PredefinedType = 0
  VerticalArea = 1.25664e+07
  Width = 100
FEATURE [Part::FeaturePython] Structure026  label="CAB PIL 14"  # Arch/BIM 172 (typed FeaturePython)
  CloneOf = -> Structure
  FaceMaker = 0
  Height = 700
  HorizontalArea = 490000
  IfcData = attributes={"GlobalId": {"name": "GlobalId", "type": "IfcGloballyUniqueId", "is_enum": false, "enum_values": []}, "Description": {"... (+484 chars omitted),+1 more (map truncated)
  IfcType = 172
  Length = 0
  Material = -> Material
  MoveBase = false
  MoveWithHost = false
  Nodes = (2) [(15210,9900,0),(15210,9900,-700)]
  NodesOffset = 0
  Normal = (0,0,0)
  PerimeterLength = 2800
  Placement = pos=(-4650,-6550,-500) rot=(0,0,1;0rad)
  PredefinedType = 0
  VerticalArea = 1960000
  Width = 0
FEATURE [Part::FeaturePython] Structure027  label="PIL 14"  # Arch/BIM 172 (typed FeaturePython)
  CloneOf = -> Structure001
  FaceMaker = 0
  Height = 8000
  HorizontalArea = 196350
  IfcData = attributes={"GlobalId": {"name": "GlobalId", "type": "IfcGloballyUniqueId", "is_enum": false, "enum_values": []}, "Description": {"... (+484 chars omitted),+1 more (map truncated)
  IfcType = 172
  Length = 0
  Material = -> Material
  MoveBase = false
  MoveWithHost = false
  Nodes = (2) [(15210,9900,0),(15210,9900,-8000)]
  NodesOffset = 0
  Normal = (0,0,0)
  PerimeterLength = 1570.8
  Placement = pos=(-4650,-6550,-1200) rot=(0,0,1;0rad)
  PredefinedType = 0
  VerticalArea = 1.25664e+07
  Width = 100
FEATURE [Part::FeaturePython] Structure028  label="PIL 15"  # Arch/BIM 172 (typed FeaturePython)
  CloneOf = -> Structure001
  FaceMaker = 0
  Height = 8000
  HorizontalArea = 196350
  IfcData = attributes={"GlobalId": {"name": "GlobalId", "type": "IfcGloballyUniqueId", "is_enum": false, "enum_values": []}, "Description": {"... (+484 chars omitted),+1 more (map truncated)
  IfcType = 172
  Length = 0
  Material = -> Material
  MoveBase = false
  MoveWithHost = false
  Nodes = (2) [(15210,9900,0),(15210,9900,-8000)]
  NodesOffset = 0
  Normal = (0,0,0)
  PerimeterLength = 1570.8
  Placement = pos=(-1430,-6550,-1200) rot=(0,0,1;0rad)
  PredefinedType = 0
  VerticalArea = 1.25664e+07
  Width = 100
FEATURE [Part::FeaturePython] Structure029  label="CAB PIL 15"  # Arch/BIM 172 (typed FeaturePython)
  CloneOf = -> Structure
  FaceMaker = 0
  Height = 700
  HorizontalArea = 490000
  IfcData = attributes={"GlobalId": {"name": "GlobalId", "type": "IfcGloballyUniqueId", "is_enum": false, "enum_values": []}, "Description": {"... (+484 chars omitted),+1 more (map truncated)
  IfcType = 172
  Length = 0
  Material = -> Material
  MoveBase = false
  MoveWithHost = false
  Nodes = (2) [(15210,9900,0),(15210,9900,-700)]
  NodesOffset = 0
  Normal = (0,0,0)
  PerimeterLength = 2800
  Placement = pos=(-1430,-6550,-500) rot=(0,0,1;0rad)
  PredefinedType = 0
  VerticalArea = 1960000
  Width = 0
FEATURE [Part::FeaturePython] Structure030  label="CAB PIL 16"  # Arch/BIM 172 (typed FeaturePython)
  CloneOf = -> Structure
  FaceMaker = 0
  Height = 700
  HorizontalArea = 490000
  IfcData = attributes={"GlobalId": {"name": "GlobalId", "type": "IfcGloballyUniqueId", "is_enum": false, "enum_values": []}, "Description": {"... (+484 chars omitted),+1 more (map truncated)
  IfcType = 172
  Length = 0
  Material = -> Material
  MoveBase = false
  MoveWithHost = false
  Nodes = (2) [(15210,9900,0),(15210,9900,-700)]
  NodesOffset = 0
  Normal = (0,0,0)
  PerimeterLength = 2800
  Placement = pos=(-13280,-9800,-500) rot=(0,0,1;0rad)
  PredefinedType = 0
  VerticalArea = 1960000
  Width = 0
FEATURE [Part::FeaturePython] Structure031  label="PIL 16"  # Arch/BIM 172 (typed FeaturePython)
  CloneOf = -> Structure001
  FaceMaker = 0
  Height = 8000
  HorizontalArea = 196350
  IfcData = attributes={"GlobalId": {"name": "GlobalId", "type": "IfcGloballyUniqueId", "is_enum": false, "enum_values": []}, "Description": {"... (+484 chars omitted),+1 more (map truncated)
  IfcType = 172
  Length = 0
  Material = -> Material
  MoveBase = false
  MoveWithHost = false
  Nodes = (2) [(15210,9900,0),(15210,9900,-8000)]
  NodesOffset = 0
  Normal = (0,0,0)
  PerimeterLength = 1570.8
  Placement = pos=(-13280,-9800,-1200) rot=(0,0,1;0rad)
  PredefinedType = 0
  VerticalArea = 1.25664e+07
  Width = 100
FEATURE [Part::FeaturePython] Structure032  label="CAB PIL 17"  # Arch/BIM 172 (typed FeaturePython)
  CloneOf = -> Structure
  FaceMaker = 0
  Height = 700
  HorizontalArea = 490000
  IfcData = attributes={"GlobalId": {"name": "GlobalId", "type": "IfcGloballyUniqueId", "is_enum": false, "enum_values": []}, "Description": {"... (+484 chars omitted),+1 more (map truncated)
  IfcType = 172
  Length = 0
  Material = -> Material
  MoveBase = false
  MoveWithHost = false
  Nodes = (2) [(15210,9900,0),(15210,9900,-700)]
  NodesOffset = 0
  Normal = (0,0,0)
  PerimeterLength = 2800
  Placement = pos=(-9050,-9800,-500) rot=(0,0,1;0rad)
  PredefinedType = 0
  VerticalArea = 1960000
  Width = 0
FEATURE [Part::FeaturePython] Structure033  label="PIL 17"  # Arch/BIM 172 (typed FeaturePython)
  CloneOf = -> Structure001
  FaceMaker = 0
  Height = 8000
  HorizontalArea = 196350
  IfcData = attributes={"GlobalId": {"name": "GlobalId", "type": "IfcGloballyUniqueId", "is_enum": false, "enum_values": []}, "Description": {"... (+484 chars omitted),+1 more (map truncated)
  IfcType = 172
  Length = 0
  Material = -> Material
  MoveBase = false
  MoveWithHost = false
  Nodes = (2) [(15210,9900,0),(15210,9900,-8000)]
  NodesOffset = 0
  Normal = (0,0,0)
  PerimeterLength = 1570.8
  Placement = pos=(-9050,-9800,-1200) rot=(0,0,1;0rad)
  PredefinedType = 0
  VerticalArea = 1.25664e+07
  Width = 100
FEATURE [Part::FeaturePython] Structure034  label="CAB PIL 18"  # Arch/BIM 172 (typed FeaturePython)
  CloneOf = -> Structure
  FaceMaker = 0
  Height = 700
  HorizontalArea = 490000
  IfcData = attributes={"GlobalId": {"name": "GlobalId", "type": "IfcGloballyUniqueId", "is_enum": false, "enum_values": []}, "Description": {"... (+484 chars omitted),+1 more (map truncated)
  IfcType = 172
  Length = 0
  Material = -> Material
  MoveBase = false
  MoveWithHost = false
  Nodes = (2) [(15210,9900,0),(15210,9900,-700)]
  NodesOffset = 0
  Normal = (0,0,0)
  PerimeterLength = 2800
  Placement = pos=(-6200,-9800,-500) rot=(0,0,1;0rad)
  PredefinedType = 0
  VerticalArea = 1960000
  Width = 0
FEATURE [Part::FeaturePython] Structure035  label="PIL 18"  # Arch/BIM 172 (typed FeaturePython)
  CloneOf = -> Structure001
  FaceMaker = 0
  Height = 8000
  HorizontalArea = 196350
  IfcData = attributes={"GlobalId": {"name": "GlobalId", "type": "IfcGloballyUniqueId", "is_enum": false, "enum_values": []}, "Description": {"... (+484 chars omitted),+1 more (map truncated)
  IfcType = 172
  Length = 0
  Material = -> Material
  MoveBase = false
  MoveWithHost = false
  Nodes = (2) [(15210,9900,0),(15210,9900,-8000)]
  NodesOffset = 0
  Normal = (0,0,0)
  PerimeterLength = 1570.8
  Placement = pos=(-6200,-9800,-1200) rot=(0,0,1;0rad)
  PredefinedType = 0
  VerticalArea = 1.25664e+07
  Width = 100
FEATURE [Part::FeaturePython] Structure036  label="CAB PIL 19"  # Arch/BIM 172 (typed FeaturePython)
  CloneOf = -> Structure
  FaceMaker = 0
  Height = 700
  HorizontalArea = 490000
  IfcData = attributes={"GlobalId": {"name": "GlobalId", "type": "IfcGloballyUniqueId", "is_enum": false, "enum_values": []}, "Description": {"... (+484 chars omitted),+1 more (map truncated)
  IfcType = 172
  Length = 0
  Material = -> Material
  MoveBase = false
  MoveWithHost = false
  Nodes = (2) [(15210,9900,0),(15210,9900,-700)]
  NodesOffset = 0
  Normal = (0,0,0)
  PerimeterLength = 2800
  Placement = pos=(-4650,-9800,-500) rot=(0,0,1;0rad)
  PredefinedType = 0
  VerticalArea = 1960000
  Width = 0
FEATURE [Part::FeaturePython] Structure037  label="PIL 19"  # Arch/BIM 172 (typed FeaturePython)
  CloneOf = -> Structure001
  FaceMaker = 0
  Height = 8000
  HorizontalArea = 196350
  IfcData = attributes={"GlobalId": {"name": "GlobalId", "type": "IfcGloballyUniqueId", "is_enum": false, "enum_values": []}, "Description": {"... (+484 chars omitted),+1 more (map truncated)
  IfcType = 172
  Length = 0
  Material = -> Material
  MoveBase = false
  MoveWithHost = false
  Nodes = (2) [(15210,9900,0),(15210,9900,-8000)]
  NodesOffset = 0
  Normal = (0,0,0)
  PerimeterLength = 1570.8
  Placement = pos=(-4650,-9800,-1200) rot=(0,0,1;0rad)
  PredefinedType = 0
  VerticalArea = 1.25664e+07
  Width = 100
FEATURE [Part::FeaturePython] Structure038  label="CAB PIL 20"  # Arch/BIM 172 (typed FeaturePython)
  CloneOf = -> Structure
  FaceMaker = 0
  Height = 700
  HorizontalArea = 490000
  IfcData = attributes={"GlobalId": {"name": "GlobalId", "type": "IfcGloballyUniqueId", "is_enum": false, "enum_values": []}, "Description": {"... (+484 chars omitted),+1 more (map truncated)
  IfcType = 172
  Length = 0
  Material = -> Material
  MoveBase = false
  MoveWithHost = false
  Nodes = (2) [(15210,9900,0),(15210,9900,-700)]
  NodesOffset = 0
  Normal = (0,0,0)
  PerimeterLength = 2800
  Placement = pos=(-1430,-9800,-500) rot=(0,0,1;0rad)
  PredefinedType = 0
  VerticalArea = 1960000
  Width = 0
FEATURE [Part::FeaturePython] Structure039  label="PIL 20"  # Arch/BIM 172 (typed FeaturePython)
  CloneOf = -> Structure001
  FaceMaker = 0
  Height = 8000
  HorizontalArea = 196350
  IfcData = attributes={"GlobalId": {"name": "GlobalId", "type": "IfcGloballyUniqueId", "is_enum": false, "enum_values": []}, "Description": {"... (+484 chars omitted),+1 more (map truncated)
  IfcType = 172
  Length = 0
  Material = -> Material
  MoveBase = false
  MoveWithHost = false
  Nodes = (2) [(15210,9900,0),(15210,9900,-8000)]
  NodesOffset = 0
  Normal = (0,0,0)
  PerimeterLength = 1570.8
  Placement = pos=(-1430,-9800,-1200) rot=(0,0,1;0rad)
  PredefinedType = 0
  VerticalArea = 1.25664e+07
  Width = 100
FEATURE [Part::FeaturePython] Structure040  label="L01"  # Arch/BIM 172 (typed FeaturePython)
  FaceMaker = 0
  Height = 250
  HorizontalArea = 9230000
  IfcData = attributes={"GlobalId": {"name": "GlobalId", "type": "IfcGloballyUniqueId", "is_enum": false, "enum_values": []}, "Description": {"... (+484 chars omitted),+1 more (map truncated)
  IfcType = 172
  Length = 0
  Material = -> Material
  MoveBase = false
  MoveWithHost = false
  Nodes = (2) [(18300,6875,0),(18300,6875,-250)]
  NodesOffset = 0
  Normal = (0,0,-1)
  PerimeterLength = 12300
  Placement = pos=(-7015,295,-1000) rot=(0,0,1;0rad)
  PredefinedType = 0
  VerticalArea = 3075000
  Width = 100
FEATURE [Part::FeaturePython] Structure081  label="25x15 C1"  # Arch/BIM 24 (typed FeaturePython)
  FaceMaker = 0
  Height = 3500
  HorizontalArea = 37500
  IfcData = attributes={"GlobalId": {"name": "GlobalId", "type": "IfcGloballyUniqueId", "is_enum": false, "enum_values": []}, "Description": {"... (+438 chars omitted),+1 more (map truncated)
  IfcType = 24
  Length = 250
  Material = -> Material
  MoveBase = false
  MoveWithHost = false
  Nodes = (2) [(-1.05471e-15,1.36424e-15,0),(-1.05471e-15,1.36424e-15,3500)]
  NodesOffset = 0
  Normal = (0,0,0)
  PerimeterLength = 800
  Placement = pos=(1930,9900,-500) rot=(0,0,1;0rad)
  PredefinedType = 0
  VerticalArea = 2.8e+06
  Width = 150
FEATURE [Part::FeaturePython] Structure084  label="25x15 C004"  # Arch/BIM 172 (typed FeaturePython)
  CloneOf = -> Structure081
  FaceMaker = 0
  Height = 3500
  HorizontalArea = 37500
  IfcData = attributes={"GlobalId": {"name": "GlobalId", "type": "IfcGloballyUniqueId", "is_enum": false, "enum_values": []}, "Description": {"... (+484 chars omitted),+1 more (map truncated)
  IfcType = 172
  Length = 250
  Material = -> Material
  MoveBase = false
  MoveWithHost = false
  Nodes = (2) [(-1.05471e-15,1.36424e-15,0),(-1.05471e-15,1.36424e-15,3500)]
  NodesOffset = 0
  Normal = (0,0,0)
  PerimeterLength = 800
  Placement = pos=(1930,100,-500) rot=(0,0,1;0rad)
  PredefinedType = 0
  VerticalArea = 2.8e+06
  Width = 150
FEATURE [Part::FeaturePython] Structure085  label="25x20 C6"  # Arch/BIM 24 (typed FeaturePython)
  FaceMaker = 0
  Height = 3500
  HorizontalArea = 50000
  IfcData = attributes={"GlobalId": {"name": "GlobalId", "type": "IfcGloballyUniqueId", "is_enum": false, "enum_values": []}, "Description": {"... (+438 chars omitted),+1 more (map truncated)
  IfcType = 24
  Length = 250
  Material = -> Material
  MoveBase = false
  MoveWithHost = false
  Nodes = (2) [(-1.05471e-15,-1.81899e-15,0),(-1.05471e-15,-1.81899e-15,3500)]
  NodesOffset = 0
  Normal = (0,0,0)
  PerimeterLength = 900
  Placement = pos=(1930,6640,-500) rot=(0,0,1;0rad)
  PredefinedType = 0
  VerticalArea = 3.15e+06
  Width = 200
FEATURE [Part::FeaturePython] Structure086  label="25x20 C007"  # Arch/BIM 172 (typed FeaturePython)
  CloneOf = -> Structure085
  FaceMaker = 0
  Height = 3500
  HorizontalArea = 50000
  IfcData = attributes={"GlobalId": {"name": "GlobalId", "type": "IfcGloballyUniqueId", "is_enum": false, "enum_values": []}, "Description": {"... (+484 chars omitted),+1 more (map truncated)
  IfcType = 172
  Length = 250
  Material = -> Material
  MoveBase = false
  MoveWithHost = false
  Nodes = (2) [(-1.05471e-15,-1.81899e-15,0),(-1.05471e-15,-1.81899e-15,3500)]
  NodesOffset = 0
  Normal = (0,0,0)
  PerimeterLength = 900
  Placement = pos=(1930,3350,-500) rot=(0,0,1;0rad)
  PredefinedType = 0
  VerticalArea = 3.15e+06
  Width = 200
FEATURE [Part::FeaturePython] Structure088  label="25x15 C005"  # Arch/BIM 24 (typed FeaturePython)
  FaceMaker = 0
  Height = 3500
  HorizontalArea = 37500
  IfcData = attributes={"GlobalId": {"name": "GlobalId", "type": "IfcGloballyUniqueId", "is_enum": false, "enum_values": []}, "Description": {"... (+438 chars omitted),+1 more (map truncated)
  IfcType = 24
  Length = 250
  Material = -> Material
  MoveBase = false
  MoveWithHost = false
  Nodes = (2) [(-1.05471e-15,1.36424e-15,0),(-1.05471e-15,1.36424e-15,3500)]
  NodesOffset = 0
  Normal = (0,0,0)
  PerimeterLength = 800
  Placement = pos=(6160,6640,-500) rot=(0,0,1;0rad)
  PredefinedType = 0
  VerticalArea = 2.8e+06
  Width = 150
FEATURE [Part::FeaturePython] Structure089  label="25x15 C006"  # Arch/BIM 24 (typed FeaturePython)
  FaceMaker = 0
  Height = 3500
  HorizontalArea = 37500
  IfcData = attributes={"GlobalId": {"name": "GlobalId", "type": "IfcGloballyUniqueId", "is_enum": false, "enum_values": []}, "Description": {"... (+438 chars omitted),+1 more (map truncated)
  IfcType = 24
  Length = 250
  Material = -> Material
  MoveBase = false
  MoveWithHost = false
  Nodes = (2) [(-1.05471e-15,1.36424e-15,0),(-1.05471e-15,1.36424e-15,3500)]
  NodesOffset = 0
  Normal = (0,0,0)
  PerimeterLength = 800
  Placement = pos=(6160,3350,-500) rot=(0,0,1;0rad)
  PredefinedType = 0
  VerticalArea = 2.8e+06
  Width = 150
FEATURE [Part::FeaturePython] Structure090  label="25x15 C007"  # Arch/BIM 24 (typed FeaturePython)
  FaceMaker = 0
  Height = 3500
  HorizontalArea = 37500
  IfcData = attributes={"GlobalId": {"name": "GlobalId", "type": "IfcGloballyUniqueId", "is_enum": false, "enum_values": []}, "Description": {"... (+438 chars omitted),+1 more (map truncated)
  IfcType = 24
  Length = 250
  Material = -> Material
  MoveBase = false
  MoveWithHost = false
  Nodes = (2) [(-1.05471e-15,1.36424e-15,0),(-1.05471e-15,1.36424e-15,3500)]
  NodesOffset = 0
  Normal = (0,0,0)
  PerimeterLength = 800
  Placement = pos=(6160,100,-500) rot=(0,0,1;0rad)
  PredefinedType = 0
  VerticalArea = 2.8e+06
  Width = 150
FEATURE [Part::FeaturePython] Structure091  label="25x15 C008"  # Arch/BIM 24 (typed FeaturePython)
  FaceMaker = 0
  Height = 3500
  HorizontalArea = 37500
  IfcData = attributes={"GlobalId": {"name": "GlobalId", "type": "IfcGloballyUniqueId", "is_enum": false, "enum_values": []}, "Description": {"... (+438 chars omitted),+1 more (map truncated)
  IfcType = 24
  Length = 250
  Material = -> Material
  MoveBase = false
  MoveWithHost = false
  Nodes = (2) [(-1.05471e-15,1.36424e-15,0),(-1.05471e-15,1.36424e-15,3500)]
  NodesOffset = 0
  Normal = (0,0,0)
  PerimeterLength = 800
  Placement = pos=(9010,100,-500) rot=(0,0,1;0rad)
  PredefinedType = 0
  VerticalArea = 2.8e+06
  Width = 150
FEATURE [Part::FeaturePython] Structure092  label="25x15 C009"  # Arch/BIM 24 (typed FeaturePython)
  FaceMaker = 0
  Height = 3500
  HorizontalArea = 37500
  IfcData = attributes={"GlobalId": {"name": "GlobalId", "type": "IfcGloballyUniqueId", "is_enum": false, "enum_values": []}, "Description": {"... (+438 chars omitted),+1 more (map truncated)
  IfcType = 24
  Length = 250
  Material = -> Material
  MoveBase = false
  MoveWithHost = false
  Nodes = (2) [(-1.05471e-15,1.36424e-15,0),(-1.05471e-15,1.36424e-15,3500)]
  NodesOffset = 0
  Normal = (0,0,0)
  PerimeterLength = 800
  Placement = pos=(10560,100,-500) rot=(0,0,1;0rad)
  PredefinedType = 0
  VerticalArea = 2.8e+06
  Width = 150
FEATURE [Part::FeaturePython] Structure093  label="25x15 C010"  # Arch/BIM 24 (typed FeaturePython)
  FaceMaker = 0
  Height = 3500
  HorizontalArea = 37500
  IfcData = attributes={"GlobalId": {"name": "GlobalId", "type": "IfcGloballyUniqueId", "is_enum": false, "enum_values": []}, "Description": {"... (+438 chars omitted),+1 more (map truncated)
  IfcType = 24
  Length = 250
  Material = -> Material
  MoveBase = false
  MoveWithHost = false
  Nodes = (2) [(-1.05471e-15,1.36424e-15,0),(-1.05471e-15,1.36424e-15,3500)]
  NodesOffset = 0
  Normal = (0,0,0)
  PerimeterLength = 800
  Placement = pos=(13780,100,-500) rot=(0,0,1;0rad)
  PredefinedType = 0
  VerticalArea = 2.8e+06
  Width = 150
FEATURE [Part::FeaturePython] Structure097  label="25x15 C014"  # Arch/BIM 24 (typed FeaturePython)
  FaceMaker = 0
  Height = 3500
  HorizontalArea = 37500
  IfcData = attributes={"GlobalId": {"name": "GlobalId", "type": "IfcGloballyUniqueId", "is_enum": false, "enum_values": []}, "Description": {"... (+438 chars omitted),+1 more (map truncated)
  IfcType = 24
  Length = 250
  Material = -> Material
  MoveBase = false
  MoveWithHost = false
  Nodes = (2) [(-1.05471e-15,1.36424e-15,0),(-1.05471e-15,1.36424e-15,3500)]
  NodesOffset = 0
  Normal = (0,0,0)
  PerimeterLength = 800
  Placement = pos=(15210,5970,-500) rot=(0,0,1;0rad)
  PredefinedType = 0
  VerticalArea = 2.8e+06
  Width = 150
FEATURE [Part::FeaturePython] Structure098  label="25x15 C015"  # Arch/BIM 24 (typed FeaturePython)
  FaceMaker = 0
  Height = 3500
  HorizontalArea = 37500
  IfcData = attributes={"GlobalId": {"name": "GlobalId", "type": "IfcGloballyUniqueId", "is_enum": false, "enum_values": []}, "Description": {"... (+438 chars omitted),+1 more (map truncated)
  IfcType = 24
  Length = 250
  Material = -> Material
  MoveBase = false
  MoveWithHost = false
  Nodes = (2) [(-1.05471e-15,1.36424e-15,0),(-1.05471e-15,1.36424e-15,3500)]
  NodesOffset = 0
  Normal = (0,0,0)
  PerimeterLength = 800
  Placement = pos=(13780,5970,-500) rot=(0,0,1;0rad)
  PredefinedType = 0
  VerticalArea = 2.8e+06
  Width = 150
FEATURE [Part::FeaturePython] Wall  label="Tabique Ascensor"  # Arch/BIM 166 (typed FeaturePython)
  Align = 1
  Area = 8300000
  Base = -> Rectangle
  BlockHeight = 0
  BlockLength = 0
  CountBroken = 0
  CountEntire = 0
  Face = 0
  Height = 1000
  HorizontalArea = 1155000
  IfcData = attributes={"GlobalId": {"name": "GlobalId", "type": "IfcGloballyUniqueId", "is_enum": false, "enum_values": []}, "Description": {"... (+533 chars omitted),+1 more (map truncated)
  IfcType = 166
  Joint = 0
  Length = 8300
  MakeBlocks = false
  Material = -> Material
  MoveBase = false
  MoveWithHost = false
  Normal = (0,0,0)
  OffsetFirst = 0
  OffsetSecond = 0
  PerimeterLength = 8300
  Placement = pos=(0,0,-1000) rot=(0,0,1;0rad)
  PredefinedType = 0
  VerticalArea = 15400000
  Width = 150
FEATURE [App::GeometryPython] BuildingPart006  label="Pilotes"  # Arch/BIM 172 (typed FeaturePython)
  Area = 0
  Group = -> [Structure001,Structure021,Structure005,Structure023,Structure025,Structure027,Structure028,Structure031,Structure033,Structure035,Structure037,Structure007,Structure039,Structure009,Structure011,Structure013,Structure003,Structure015,Structure017,Structure019]
  Height = 0
  HeightPropagate = true
  IfcData = attributes={"GlobalId": {"name": "GlobalId", "type": "IfcGloballyUniqueId", "is_enum": false, "enum_values": []}, "Description": {"... (+484 chars omitted),+1 more (map truncated)
  IfcType = 172
  LevelOffset = 0
  Placement = pos=(0,0,500) rot=(0,0,1;0rad)
  PredefinedType = 0
FEATURE [App::GeometryPython] BuildingPart007  label="Cabezales Pilotes"  # Arch/BIM 172 (typed FeaturePython)
  Area = 0
  Group = -> [Structure,Structure020,Structure004,Structure022,Structure024,Structure026,Structure029,Structure030,Structure032,Structure034,Structure036,Structure006,Structure038,Structure008,Structure010,Structure012,Structure002,Structure014,Structure016,Structure018]
  Height = 0
  HeightPropagate = true
  IfcData = attributes={"GlobalId": {"name": "GlobalId", "type": "IfcGloballyUniqueId", "is_enum": false, "enum_values": []}, "Description": {"... (+484 chars omitted),+1 more (map truncated)
  IfcType = 172
  LevelOffset = 0
  Placement = pos=(0,0,500) rot=(0,0,1;0rad)
  PredefinedType = 0
FEATURE [App::GeometryPython] BuildingPart008  label="Losa fundacion"  # Arch/BIM 172 (typed FeaturePython)
  Area = 0
  Group = -> [Structure040]
  Height = 0
  HeightPropagate = true
  IfcData = attributes={"GlobalId": {"name": "GlobalId", "type": "IfcGloballyUniqueId", "is_enum": false, "enum_values": []}, "Description": {"... (+484 chars omitted),+1 more (map truncated)
  IfcType = 172
  LevelOffset = 0
  Placement = pos=(0,0,500) rot=(0,0,1;0rad)
  PredefinedType = 0
FEATURE [Part::FeaturePython] Structure099  label="25x15 C016"  # Arch/BIM 172 (typed FeaturePython)
  CloneOf = -> Structure081
  FaceMaker = 0
  Height = 3500
  HorizontalArea = 37500
  IfcData = attributes={"GlobalId": {"name": "GlobalId", "type": "IfcGloballyUniqueId", "is_enum": false, "enum_values": []}, "Description": {"... (+484 chars omitted),+1 more (map truncated)
  IfcType = 172
  Length = 250
  Material = -> Material
  MoveBase = false
  MoveWithHost = false
  Nodes = (2) [(-1.05471e-15,1.36424e-15,0),(-1.05471e-15,1.36424e-15,3500)]
  NodesOffset = 0
  Normal = (0,0,0)
  PerimeterLength = 800
  Placement = pos=(1930,9900,-500) rot=(0,0,1;0rad)
  PredefinedType = 0
  VerticalArea = 2.8e+06
  Width = 150
FEATURE [Part::FeaturePython] Structure100  label="25x15 C017"  # Arch/BIM 172 (typed FeaturePython)
  CloneOf = -> Structure081
  FaceMaker = 0
  Height = 3500
  HorizontalArea = 37500
  IfcData = attributes={"GlobalId": {"name": "GlobalId", "type": "IfcGloballyUniqueId", "is_enum": false, "enum_values": []}, "Description": {"... (+484 chars omitted),+1 more (map truncated)
  IfcType = 172
  Length = 250
  Material = -> Material
  MoveBase = false
  MoveWithHost = false
  Nodes = (2) [(-1.05471e-15,1.36424e-15,0),(-1.05471e-15,1.36424e-15,3500)]
  NodesOffset = 0
  Normal = (0,0,0)
  PerimeterLength = 800
  Placement = pos=(9010,6640,-500) rot=(0,0,1;1.5708rad)
  PredefinedType = 0
  VerticalArea = 2.8e+06
  Width = 150
FEATURE [Part::FeaturePython] Structure101  label="25x15 C018"  # Arch/BIM 172 (typed FeaturePython)
  CloneOf = -> Structure081
  FaceMaker = 0
  Height = 3500
  HorizontalArea = 37500
  IfcData = attributes={"GlobalId": {"name": "GlobalId", "type": "IfcGloballyUniqueId", "is_enum": false, "enum_values": []}, "Description": {"... (+484 chars omitted),+1 more (map truncated)
  IfcType = 172
  Length = 250
  Material = -> Material
  MoveBase = false
  MoveWithHost = false
  Nodes = (2) [(-1.05471e-15,1.36424e-15,0),(-1.05471e-15,1.36424e-15,3500)]
  NodesOffset = 0
  Normal = (0,0,0)
  PerimeterLength = 800
  Placement = pos=(9010,3350,-500) rot=(0,0,1;1.5708rad)
  PredefinedType = 0
  VerticalArea = 2.8e+06
  Width = 150
FEATURE [Part::FeaturePython] Structure102  label="25x15 C019"  # Arch/BIM 172 (typed FeaturePython)
  CloneOf = -> Structure081
  FaceMaker = 0
  Height = 3500
  HorizontalArea = 37500
  IfcData = attributes={"GlobalId": {"name": "GlobalId", "type": "IfcGloballyUniqueId", "is_enum": false, "enum_values": []}, "Description": {"... (+484 chars omitted),+1 more (map truncated)
  IfcType = 172
  Length = 250
  Material = -> Material
  MoveBase = false
  MoveWithHost = false
  Nodes = (2) [(-1.05471e-15,1.36424e-15,0),(-1.05471e-15,1.36424e-15,3500)]
  NodesOffset = 0
  Normal = (0,0,0)
  PerimeterLength = 800
  Placement = pos=(10560,3350,-500) rot=(0,0,1;1.5708rad)
  PredefinedType = 0
  VerticalArea = 2.8e+06
  Width = 150
FEATURE [Part::FeaturePython] Structure103  label="25x15 C020"  # Arch/BIM 172 (typed FeaturePython)
  CloneOf = -> Structure081
  FaceMaker = 0
  Height = 3500
  HorizontalArea = 37500
  IfcData = attributes={"GlobalId": {"name": "GlobalId", "type": "IfcGloballyUniqueId", "is_enum": false, "enum_values": []}, "Description": {"... (+484 chars omitted),+1 more (map truncated)
  IfcType = 172
  Length = 250
  Material = -> Material
  MoveBase = false
  MoveWithHost = false
  Nodes = (2) [(-1.05471e-15,1.36424e-15,0),(-1.05471e-15,1.36424e-15,3500)]
  NodesOffset = 0
  Normal = (0,0,0)
  PerimeterLength = 800
  Placement = pos=(13780,3350,-500) rot=(0,0,1;1.5708rad)
  PredefinedType = 0
  VerticalArea = 2.8e+06
  Width = 150
FEATURE [Part::FeaturePython] Structure104  label="25x15 C003"  # Arch/BIM 172 (typed FeaturePython)
  CloneOf = -> Structure081
  FaceMaker = 0
  Height = 3500
  HorizontalArea = 37500
  IfcData = attributes={"GlobalId": {"name": "GlobalId", "type": "IfcGloballyUniqueId", "is_enum": false, "enum_values": []}, "Description": {"... (+484 chars omitted),+1 more (map truncated)
  IfcType = 172
  Length = 250
  Material = -> Material
  MoveBase = false
  MoveWithHost = false
  Nodes = (2) [(-1.05471e-15,1.36424e-15,0),(-1.05471e-15,1.36424e-15,3500)]
  NodesOffset = 0
  Normal = (0,0,0)
  PerimeterLength = 800
  Placement = pos=(9010,9900,-500) rot=(0,0,1;0rad)
  PredefinedType = 0
  VerticalArea = 2.8e+06
  Width = 150
FEATURE [Part::FeaturePython] Structure105  label="25x15 C002"  # Arch/BIM 172 (typed FeaturePython)
  CloneOf = -> Structure081
  FaceMaker = 0
  Height = 3500
  HorizontalArea = 37500
  IfcData = attributes={"GlobalId": {"name": "GlobalId", "type": "IfcGloballyUniqueId", "is_enum": false, "enum_values": []}, "Description": {"... (+484 chars omitted),+1 more (map truncated)
  IfcType = 172
  Length = 250
  Material = -> Material
  MoveBase = false
  MoveWithHost = false
  Nodes = (2) [(-1.05471e-15,1.36424e-15,0),(-1.05471e-15,1.36424e-15,3500)]
  NodesOffset = 0
  Normal = (0,0,0)
  PerimeterLength = 800
  Placement = pos=(6160,9900,-500) rot=(0,0,1;0rad)
  PredefinedType = 0
  VerticalArea = 2.8e+06
  Width = 150
FEATURE [Part::FeaturePython] Structure106  label="25x15 C025"  # Arch/BIM 172 (typed FeaturePython)
  CloneOf = -> Structure081
  FaceMaker = 0
  Height = 3500
  HorizontalArea = 37500
  IfcData = attributes={"GlobalId": {"name": "GlobalId", "type": "IfcGloballyUniqueId", "is_enum": false, "enum_values": []}, "Description": {"... (+484 chars omitted),+1 more (map truncated)
  IfcType = 172
  Length = 250
  Material = -> Material
  MoveBase = false
  MoveWithHost = false
  Nodes = (2) [(-1.05471e-15,1.36424e-15,0),(-1.05471e-15,1.36424e-15,3500)]
  NodesOffset = 0
  Normal = (0,0,0)
  PerimeterLength = 800
  Placement = pos=(12010,9900,-500) rot=(0,0,1;0rad)
  PredefinedType = 0
  VerticalArea = 2.8e+06
  Width = 150
FEATURE [Part::FeaturePython] Structure107  label="25x15 C024"  # Arch/BIM 172 (typed FeaturePython)
  CloneOf = -> Structure081
  FaceMaker = 0
  Height = 3500
  HorizontalArea = 37500
  IfcData = attributes={"GlobalId": {"name": "GlobalId", "type": "IfcGloballyUniqueId", "is_enum": false, "enum_values": []}, "Description": {"... (+484 chars omitted),+1 more (map truncated)
  IfcType = 172
  Length = 250
  Material = -> Material
  MoveBase = false
  MoveWithHost = false
  Nodes = (2) [(-1.05471e-15,1.36424e-15,0),(-1.05471e-15,1.36424e-15,3500)]
  NodesOffset = 0
  Normal = (0,0,0)
  PerimeterLength = 800
  Placement = pos=(15210,9900,-500) rot=(0,0,1;0rad)
  PredefinedType = 0
  VerticalArea = 2.8e+06
  Width = 150
FEATURE [App::GeometryPython] BuildingPart004  label="Columnas"  # Arch/BIM 172 (typed FeaturePython)
  Area = 0
  Group = -> [Structure105,Structure104,Structure084,Structure088,Structure089,Structure090,Structure091,Structure092,Structure093,Structure097,Structure098,Structure099,Structure100,Structure101,Structure102,Structure103,Structure107,Structure106,Structure081,Structure086,Structure085]
  Height = 0
  HeightPropagate = true
  IfcData = attributes={"GlobalId": {"name": "GlobalId", "type": "IfcGloballyUniqueId", "is_enum": false, "enum_values": []}, "Description": {"... (+484 chars omitted),+1 more (map truncated)
  IfcType = 172
  LevelOffset = 0
  PredefinedType = 0
FEATURE [Part::FeaturePython] Wall001  label="Tabique Ascensor PB"  # Arch/BIM 166 (typed FeaturePython)
  Align = 1
  Area = 24900000
  Base = -> Rectangle003
  BlockHeight = 0
  BlockLength = 0
  CountBroken = 0
  CountEntire = 0
  Face = 0
  Height = 3000
  HorizontalArea = 1155000
  IfcData = attributes={"GlobalId": {"name": "GlobalId", "type": "IfcGloballyUniqueId", "is_enum": false, "enum_values": []}, "Description": {"... (+533 chars omitted),+1 more (map truncated)
  IfcType = 166
  Joint = 0
  Length = 8300
  MakeBlocks = false
  Material = -> Material
  MoveBase = false
  MoveWithHost = false
  Normal = (0,0,0)
  OffsetFirst = 0
  OffsetSecond = 0
  PerimeterLength = 8300
  PredefinedType = 0
  VerticalArea = 46200000
  Width = 150
FEATURE [Part::FeaturePython] Structure108  label="V20x40 V122"  # Arch/BIM 7 (typed FeaturePython)
  FaceMaker = 0
  Height = 400
  HorizontalArea = 617000
  IfcData = attributes={"GlobalId": {"name": "GlobalId", "type": "IfcGloballyUniqueId", "is_enum": false, "enum_values": []}, "Description": {"... (+475 chars omitted),+1 more (map truncated)
  IfcType = 7
  Length = 3085
  Material = -> Material
  MoveBase = false
  MoveWithHost = false
  Nodes = (2) [(-1.72563e-31,0,-7.77156e-16),(3085,0,-7.77156e-16)]
  NodesOffset = 0
  Normal = (0,0,0)
  PerimeterLength = 6570
  Placement = pos=(1930,9825,2800) rot=(0,0,-1;1.5708rad)
  PredefinedType = 0
  VerticalArea = 2.628e+06
  Width = 200
FEATURE [Part::FeaturePython] Structure109  label="V15x40 V101"  # Arch/BIM 7 (typed FeaturePython)
  FaceMaker = 0
  Height = 400
  HorizontalArea = 597000
  IfcData = attributes={"GlobalId": {"name": "GlobalId", "type": "IfcGloballyUniqueId", "is_enum": false, "enum_values": []}, "Description": {"... (+475 chars omitted),+1 more (map truncated)
  IfcType = 7
  Length = 3980
  Material = -> Material
  MoveBase = false
  MoveWithHost = false
  Nodes = (2) [(-1.72563e-31,-1.42109e-15,-7.77156e-16),(3980,-1.42109e-15,-7.77156e-16)]
  NodesOffset = 0
  Normal = (0,0,0)
  PerimeterLength = 8260
  Placement = pos=(2055,9900,2800) rot=(0,0,1;0rad)
  PredefinedType = 0
  VerticalArea = 3.304e+06
  Width = 150
FEATURE [Part::FeaturePython] Structure110  label="V20x40 V121"  # Arch/BIM 7 (typed FeaturePython)
  FaceMaker = 0
  Height = 400
  HorizontalArea = 618000
  IfcData = attributes={"GlobalId": {"name": "GlobalId", "type": "IfcGloballyUniqueId", "is_enum": false, "enum_values": []}, "Description": {"... (+475 chars omitted),+1 more (map truncated)
  IfcType = 7
  Length = 3090
  Material = -> Material
  MoveBase = false
  MoveWithHost = false
  Nodes = (2) [(-1.72563e-31,0,-7.77156e-16),(3090,0,-7.77156e-16)]
  NodesOffset = 0
  Normal = (0,0,0)
  PerimeterLength = 6580
  Placement = pos=(1930,6540,2800) rot=(0,0,-1;1.5708rad)
  PredefinedType = 0
  VerticalArea = 2.632e+06
  Width = 200
FEATURE [Part::FeaturePython] Structure111  label="V20x40 V120"  # Arch/BIM 7 (typed FeaturePython)
  FaceMaker = 0
  Height = 400
  HorizontalArea = 615000
  IfcData = attributes={"GlobalId": {"name": "GlobalId", "type": "IfcGloballyUniqueId", "is_enum": false, "enum_values": []}, "Description": {"... (+475 chars omitted),+1 more (map truncated)
  IfcType = 7
  Length = 3075
  Material = -> Material
  MoveBase = false
  MoveWithHost = false
  Nodes = (2) [(-1.72563e-31,0,-7.77156e-16),(3075,0,-7.77156e-16)]
  NodesOffset = 0
  Normal = (0,0,0)
  PerimeterLength = 6550
  Placement = pos=(1930,3250,2800) rot=(0,0,-1;1.5708rad)
  PredefinedType = 0
  VerticalArea = 2.62e+06
  Width = 200
FEATURE [Part::FeaturePython] Structure112  label="V15x40 V106"  # Arch/BIM 7 (typed FeaturePython)
  FaceMaker = 0
  Height = 400
  HorizontalArea = 597000
  IfcData = attributes={"GlobalId": {"name": "GlobalId", "type": "IfcGloballyUniqueId", "is_enum": false, "enum_values": []}, "Description": {"... (+475 chars omitted),+1 more (map truncated)
  IfcType = 7
  Length = 3980
  Material = -> Material
  MoveBase = false
  MoveWithHost = false
  Nodes = (2) [(-1.72563e-31,-1.42109e-15,-7.77156e-16),(3980,-1.42109e-15,-7.77156e-16)]
  NodesOffset = 0
  Normal = (0,0,0)
  PerimeterLength = 8260
  Placement = pos=(2055,6640,2800) rot=(0,0,1;0rad)
  PredefinedType = 0
  VerticalArea = 3.304e+06
  Width = 150
FEATURE [Part::FeaturePython] Structure113  label="V15x40 V111"  # Arch/BIM 7 (typed FeaturePython)
  FaceMaker = 0
  Height = 400
  HorizontalArea = 597000
  IfcData = attributes={"GlobalId": {"name": "GlobalId", "type": "IfcGloballyUniqueId", "is_enum": false, "enum_values": []}, "Description": {"... (+475 chars omitted),+1 more (map truncated)
  IfcType = 7
  Length = 3980
  Material = -> Material
  MoveBase = false
  MoveWithHost = false
  Nodes = (2) [(-1.72563e-31,-1.42109e-15,-7.77156e-16),(3980,-1.42109e-15,-7.77156e-16)]
  NodesOffset = 0
  Normal = (0,0,0)
  PerimeterLength = 8260
  Placement = pos=(2055,3350,2800) rot=(0,0,1;0rad)
  PredefinedType = 0
  VerticalArea = 3.304e+06
  Width = 150
FEATURE [Part::FeaturePython] Structure114  label="V15x40 V116"  # Arch/BIM 7 (typed FeaturePython)
  FaceMaker = 0
  Height = 400
  HorizontalArea = 597000
  IfcData = attributes={"GlobalId": {"name": "GlobalId", "type": "IfcGloballyUniqueId", "is_enum": false, "enum_values": []}, "Description": {"... (+475 chars omitted),+1 more (map truncated)
  IfcType = 7
  Length = 3980
  Material = -> Material
  MoveBase = false
  MoveWithHost = false
  Nodes = (2) [(-1.72563e-31,-1.42109e-15,-7.77156e-16),(3980,-1.42109e-15,-7.77156e-16)]
  NodesOffset = 0
  Normal = (0,0,0)
  PerimeterLength = 8260
  Placement = pos=(2055,100,2800) rot=(0,0,1;0rad)
  PredefinedType = 0
  VerticalArea = 3.304e+06
  Width = 150
FEATURE [Part::FeaturePython] Structure115  label="V15x40 V102"  # Arch/BIM 7 (typed FeaturePython)
  FaceMaker = 0
  Height = 400
  HorizontalArea = 390000
  IfcData = attributes={"GlobalId": {"name": "GlobalId", "type": "IfcGloballyUniqueId", "is_enum": false, "enum_values": []}, "Description": {"... (+475 chars omitted),+1 more (map truncated)
  IfcType = 7
  Length = 2600
  Material = -> Material
  MoveBase = false
  MoveWithHost = false
  Nodes = (2) [(-1.72563e-31,-1.42109e-15,-7.77156e-16),(2600,-1.42109e-15,-7.77156e-16)]
  NodesOffset = 0
  Normal = (0,0,0)
  PerimeterLength = 5500
  Placement = pos=(6285,9900,2800) rot=(0,0,1;0rad)
  PredefinedType = 0
  VerticalArea = 2200000
  Width = 150
FEATURE [Part::FeaturePython] Structure116  label="V15x40 V107"  # Arch/BIM 7 (typed FeaturePython)
  FaceMaker = 0
  Height = 400
  HorizontalArea = 397500
  IfcData = attributes={"GlobalId": {"name": "GlobalId", "type": "IfcGloballyUniqueId", "is_enum": false, "enum_values": []}, "Description": {"... (+475 chars omitted),+1 more (map truncated)
  IfcType = 7
  Length = 2650
  Material = -> Material
  MoveBase = false
  MoveWithHost = false
  Nodes = (2) [(-1.72563e-31,-1.42109e-15,-7.77156e-16),(2650,-1.42109e-15,-7.77156e-16)]
  NodesOffset = 0
  Normal = (0,0,0)
  PerimeterLength = 5600
  Placement = pos=(6285,6640,2800) rot=(0,0,1;0rad)
  PredefinedType = 0
  VerticalArea = 2240000
  Width = 150
FEATURE [Part::FeaturePython] Structure117  label="V15x40 V112"  # Arch/BIM 7 (typed FeaturePython)
  FaceMaker = 0
  Height = 400
  HorizontalArea = 397500
  IfcData = attributes={"GlobalId": {"name": "GlobalId", "type": "IfcGloballyUniqueId", "is_enum": false, "enum_values": []}, "Description": {"... (+475 chars omitted),+1 more (map truncated)
  IfcType = 7
  Length = 2650
  Material = -> Material
  MoveBase = false
  MoveWithHost = false
  Nodes = (2) [(-1.72563e-31,-1.42109e-15,-7.77156e-16),(2650,-1.42109e-15,-7.77156e-16)]
  NodesOffset = 0
  Normal = (0,0,0)
  PerimeterLength = 5600
  Placement = pos=(6285,3350,2800) rot=(0,0,1;0rad)
  PredefinedType = 0
  VerticalArea = 2240000
  Width = 150
FEATURE [Part::FeaturePython] Structure118  label="V15x40 V117"  # Arch/BIM 7 (typed FeaturePython)
  FaceMaker = 0
  Height = 400
  HorizontalArea = 390000
  IfcData = attributes={"GlobalId": {"name": "GlobalId", "type": "IfcGloballyUniqueId", "is_enum": false, "enum_values": []}, "Description": {"... (+475 chars omitted),+1 more (map truncated)
  IfcType = 7
  Length = 2600
  Material = -> Material
  MoveBase = false
  MoveWithHost = false
  Nodes = (2) [(-1.72563e-31,-1.42109e-15,-7.77156e-16),(2600,-1.42109e-15,-7.77156e-16)]
  NodesOffset = 0
  Normal = (0,0,0)
  PerimeterLength = 5500
  Placement = pos=(6285,100,2800) rot=(0,0,1;0rad)
  PredefinedType = 0
  VerticalArea = 2200000
  Width = 150
FEATURE [Part::FeaturePython] Structure119  label="V15x40 V103"  # Arch/BIM 7 (typed FeaturePython)
  FaceMaker = 0
  Height = 400
  HorizontalArea = 412500
  IfcData = attributes={"GlobalId": {"name": "GlobalId", "type": "IfcGloballyUniqueId", "is_enum": false, "enum_values": []}, "Description": {"... (+475 chars omitted),+1 more (map truncated)
  IfcType = 7
  Length = 2750
  Material = -> Material
  MoveBase = false
  MoveWithHost = false
  Nodes = (2) [(-1.72563e-31,-1.42109e-15,-7.77156e-16),(2750,-1.42109e-15,-7.77156e-16)]
  NodesOffset = 0
  Normal = (0,0,0)
  PerimeterLength = 5800
  Placement = pos=(9135,9900,2800) rot=(0,0,1;0rad)
  PredefinedType = 0
  VerticalArea = 2320000
  Width = 150
FEATURE [Part::FeaturePython] Structure120  label="V15x40 V104"  # Arch/BIM 7 (typed FeaturePython)
  FaceMaker = 0
  Height = 400
  HorizontalArea = 442500
  IfcData = attributes={"GlobalId": {"name": "GlobalId", "type": "IfcGloballyUniqueId", "is_enum": false, "enum_values": []}, "Description": {"... (+475 chars omitted),+1 more (map truncated)
  IfcType = 7
  Length = 2950
  Material = -> Material
  MoveBase = false
  MoveWithHost = false
  Nodes = (2) [(-1.72563e-31,-1.42109e-15,-7.77156e-16),(2950,-1.42109e-15,-7.77156e-16)]
  NodesOffset = 0
  Normal = (0,0,0)
  PerimeterLength = 6200
  Placement = pos=(12135,9900,2800) rot=(0,0,1;0rad)
  PredefinedType = 0
  VerticalArea = 2.48e+06
  Width = 150
FEATURE [Part::FeaturePython] Structure121  label="V15x40 V108"  # Arch/BIM 7 (typed FeaturePython)
  FaceMaker = 0
  Height = 400
  HorizontalArea = 210000
  IfcData = attributes={"GlobalId": {"name": "GlobalId", "type": "IfcGloballyUniqueId", "is_enum": false, "enum_values": []}, "Description": {"... (+475 chars omitted),+1 more (map truncated)
  IfcType = 7
  Length = 1400
  Material = -> Material
  MoveBase = false
  MoveWithHost = false
  Nodes = (2) [(-1.72563e-31,-1.42109e-15,-7.77156e-16),(1400,-1.42109e-15,-7.77156e-16)]
  NodesOffset = 0
  Normal = (0,0,0)
  PerimeterLength = 3100
  Placement = pos=(9085,6640,2800) rot=(0,0,1;0rad)
  PredefinedType = 0
  VerticalArea = 1240000
  Width = 150
FEATURE [Part::FeaturePython] Structure122  label="V15x40 V113"  # Arch/BIM 7 (typed FeaturePython)
  FaceMaker = 0
  Height = 400
  HorizontalArea = 210000
  IfcData = attributes={"GlobalId": {"name": "GlobalId", "type": "IfcGloballyUniqueId", "is_enum": false, "enum_values": []}, "Description": {"... (+475 chars omitted),+1 more (map truncated)
  IfcType = 7
  Length = 1400
  Material = -> Material
  MoveBase = false
  MoveWithHost = false
  Nodes = (2) [(-1.72563e-31,-1.42109e-15,-7.77156e-16),(1400,-1.42109e-15,-7.77156e-16)]
  NodesOffset = 0
  Normal = (0,0,0)
  PerimeterLength = 3100
  Placement = pos=(9085,3350,2800) rot=(0,0,1;0rad)
  PredefinedType = 0
  VerticalArea = 1240000
  Width = 150
FEATURE [Part::FeaturePython] Structure123  label="V15x40 V118"  # Arch/BIM 7 (typed FeaturePython)
  FaceMaker = 0
  Height = 400
  HorizontalArea = 195000
  IfcData = attributes={"GlobalId": {"name": "GlobalId", "type": "IfcGloballyUniqueId", "is_enum": false, "enum_values": []}, "Description": {"... (+475 chars omitted),+1 more (map truncated)
  IfcType = 7
  Length = 1300
  Material = -> Material
  MoveBase = false
  MoveWithHost = false
  Nodes = (2) [(-1.72563e-31,-1.42109e-15,-7.77156e-16),(1300,-1.42109e-15,-7.77156e-16)]
  NodesOffset = 0
  Normal = (0,0,0)
  PerimeterLength = 2900
  Placement = pos=(9135,100,2800) rot=(0,0,1;0rad)
  PredefinedType = 0
  VerticalArea = 1160000
  Width = 150
FEATURE [Part::FeaturePython] Structure124  label="V15x40 V119"  # Arch/BIM 7 (typed FeaturePython)
  FaceMaker = 0
  Height = 400
  HorizontalArea = 445500
  IfcData = attributes={"GlobalId": {"name": "GlobalId", "type": "IfcGloballyUniqueId", "is_enum": false, "enum_values": []}, "Description": {"... (+475 chars omitted),+1 more (map truncated)
  IfcType = 7
  Length = 2970
  Material = -> Material
  MoveBase = false
  MoveWithHost = false
  Nodes = (2) [(-1.72563e-31,-1.42109e-15,-7.77156e-16),(2970,-1.42109e-15,-7.77156e-16)]
  NodesOffset = 0
  Normal = (0,0,0)
  PerimeterLength = 6240
  Placement = pos=(10685,100,2800) rot=(0,0,1;0rad)
  PredefinedType = 0
  VerticalArea = 2.496e+06
  Width = 150
FEATURE [Part::FeaturePython] Structure125  label="V15x40 V115"  # Arch/BIM 7 (typed FeaturePython)
  FaceMaker = 0
  Height = 400
  HorizontalArea = 460500
  IfcData = attributes={"GlobalId": {"name": "GlobalId", "type": "IfcGloballyUniqueId", "is_enum": false, "enum_values": []}, "Description": {"... (+475 chars omitted),+1 more (map truncated)
  IfcType = 7
  Length = 3070
  Material = -> Material
  MoveBase = false
  MoveWithHost = false
  Nodes = (2) [(-1.72563e-31,-1.42109e-15,-7.77156e-16),(3070,-1.42109e-15,-7.77156e-16)]
  NodesOffset = 0
  Normal = (0,0,0)
  PerimeterLength = 6440
  Placement = pos=(10635,3350,2800) rot=(0,0,1;0rad)
  PredefinedType = 0
  VerticalArea = 2.576e+06
  Width = 150
FEATURE [Part::FeaturePython] Structure126  label="V20x40 V133"  # Arch/BIM 7 (typed FeaturePython)
  FaceMaker = 0
  Height = 400
  HorizontalArea = 635000
  IfcData = attributes={"GlobalId": {"name": "GlobalId", "type": "IfcGloballyUniqueId", "is_enum": false, "enum_values": []}, "Description": {"... (+475 chars omitted),+1 more (map truncated)
  IfcType = 7
  Length = 3175
  Material = -> Material
  MoveBase = false
  MoveWithHost = false
  Nodes = (2) [(-1.72563e-31,0,-7.77156e-16),(3175,0,-7.77156e-16)]
  NodesOffset = 0
  Normal = (0,0,0)
  PerimeterLength = 6750
  Placement = pos=(13780,175,2800) rot=(0,0,1;1.5708rad)
  PredefinedType = 0
  VerticalArea = 2.7e+06
  Width = 200
FEATURE [Part::FeaturePython] Structure127  label="V20x40 V134"  # Arch/BIM 7 (typed FeaturePython)
  FaceMaker = 0
  Height = 400
  HorizontalArea = 509000
  IfcData = attributes={"GlobalId": {"name": "GlobalId", "type": "IfcGloballyUniqueId", "is_enum": false, "enum_values": []}, "Description": {"... (+475 chars omitted),+1 more (map truncated)
  IfcType = 7
  Length = 2545
  Material = -> Material
  MoveBase = false
  MoveWithHost = false
  Nodes = (2) [(-1.72563e-31,0,-7.77156e-16),(2545,0,-7.77156e-16)]
  NodesOffset = 0
  Normal = (0,0,0)
  PerimeterLength = 5490
  Placement = pos=(13780,3350,2800) rot=(0,0,1;1.5708rad)
  PredefinedType = 0
  VerticalArea = 2196000
  Width = 200
FEATURE [Part::FeaturePython] Structure128  label="V20x40 V135"  # Arch/BIM 7 (typed FeaturePython)
  FaceMaker = 0
  Height = 400
  HorizontalArea = 756000
  IfcData = attributes={"GlobalId": {"name": "GlobalId", "type": "IfcGloballyUniqueId", "is_enum": false, "enum_values": []}, "Description": {"... (+475 chars omitted),+1 more (map truncated)
  IfcType = 7
  Length = 3780
  Material = -> Material
  MoveBase = false
  MoveWithHost = false
  Nodes = (2) [(-1.72563e-31,0,-7.77156e-16),(3780,0,-7.77156e-16)]
  NodesOffset = 0
  Normal = (0,0,0)
  PerimeterLength = 7960
  Placement = pos=(15210,6045,2800) rot=(0,0,1;1.5708rad)
  PredefinedType = 0
  VerticalArea = 3.184e+06
  Width = 200
FEATURE [Part::FeaturePython] Structure129  label="V15x40 V109"  # Arch/BIM 7 (typed FeaturePython)
  FaceMaker = 0
  Height = 400
  HorizontalArea = 235500
  IfcData = attributes={"GlobalId": {"name": "GlobalId", "type": "IfcGloballyUniqueId", "is_enum": false, "enum_values": []}, "Description": {"... (+475 chars omitted),+1 more (map truncated)
  IfcType = 7
  Length = 1570
  Material = -> Material
  MoveBase = false
  MoveWithHost = false
  Nodes = (2) [(-1.72563e-31,-1.42109e-15,-7.77156e-16),(1570,-1.42109e-15,-7.77156e-16)]
  NodesOffset = 0
  Normal = (0,0,0)
  PerimeterLength = 3440
  Placement = pos=(13655,5970,2800) rot=(0,0,1;3.14159rad)
  PredefinedType = 0
  VerticalArea = 1.376e+06
  Width = 150
FEATURE [Part::FeaturePython] Structure130  label="V15x40 V110"  # Arch/BIM 7 (typed FeaturePython)
  FaceMaker = 0
  Height = 400
  HorizontalArea = 177000
  IfcData = attributes={"GlobalId": {"name": "GlobalId", "type": "IfcGloballyUniqueId", "is_enum": false, "enum_values": []}, "Description": {"... (+475 chars omitted),+1 more (map truncated)
  IfcType = 7
  Length = 1180
  Material = -> Material
  MoveBase = false
  MoveWithHost = false
  Nodes = (2) [(-1.72563e-31,-1.42109e-15,-7.77156e-16),(1180,-1.42109e-15,-7.77156e-16)]
  NodesOffset = 0
  Normal = (0,0,0)
  PerimeterLength = 2660
  Placement = pos=(13905,5970,2800) rot=(0,0,1;0rad)
  PredefinedType = 0
  VerticalArea = 1064000
  Width = 150
FEATURE [Part::FeaturePython] Structure131  label="V15x40 V125"  # Arch/BIM 7 (typed FeaturePython)
  FaceMaker = 0
  Height = 400
  HorizontalArea = 466500
  IfcData = attributes={"GlobalId": {"name": "GlobalId", "type": "IfcGloballyUniqueId", "is_enum": false, "enum_values": []}, "Description": {"... (+475 chars omitted),+1 more (map truncated)
  IfcType = 7
  Length = 3110
  Material = -> Material
  MoveBase = false
  MoveWithHost = false
  Nodes = (2) [(-1.72563e-31,-1.42109e-15,-7.77156e-16),(3110,-1.42109e-15,-7.77156e-16)]
  NodesOffset = 0
  Normal = (0,0,0)
  PerimeterLength = 6520
  Placement = pos=(6160,9825,2800) rot=(0,0,-1;1.5708rad)
  PredefinedType = 0
  VerticalArea = 2.608e+06
  Width = 150
FEATURE [Part::FeaturePython] Structure132  label="V15x40 V124"  # Arch/BIM 7 (typed FeaturePython)
  FaceMaker = 0
  Height = 400
  HorizontalArea = 471000
  IfcData = attributes={"GlobalId": {"name": "GlobalId", "type": "IfcGloballyUniqueId", "is_enum": false, "enum_values": []}, "Description": {"... (+475 chars omitted),+1 more (map truncated)
  IfcType = 7
  Length = 3140
  Material = -> Material
  MoveBase = false
  MoveWithHost = false
  Nodes = (2) [(-1.72563e-31,-1.42109e-15,-7.77156e-16),(3140,-1.42109e-15,-7.77156e-16)]
  NodesOffset = 0
  Normal = (0,0,0)
  PerimeterLength = 6580
  Placement = pos=(6160,6565,2800) rot=(0,0,-1;1.5708rad)
  PredefinedType = 0
  VerticalArea = 2.632e+06
  Width = 150
FEATURE [Part::FeaturePython] Structure133  label="V15x40 V123"  # Arch/BIM 7 (typed FeaturePython)
  FaceMaker = 0
  Height = 400
  HorizontalArea = 465000
  IfcData = attributes={"GlobalId": {"name": "GlobalId", "type": "IfcGloballyUniqueId", "is_enum": false, "enum_values": []}, "Description": {"... (+475 chars omitted),+1 more (map truncated)
  IfcType = 7
  Length = 3100
  Material = -> Material
  MoveBase = false
  MoveWithHost = false
  Nodes = (2) [(-1.72563e-31,-1.42109e-15,-7.77156e-16),(3100,-1.42109e-15,-7.77156e-16)]
  NodesOffset = 0
  Normal = (0,0,0)
  PerimeterLength = 6500
  Placement = pos=(6160,3275,2800) rot=(0,0,-1;1.5708rad)
  PredefinedType = 0
  VerticalArea = 2.6e+06
  Width = 150
FEATURE [Part::FeaturePython] Structure134  label="V15x40 V128"  # Arch/BIM 7 (typed FeaturePython)
  FaceMaker = 0
  Height = 400
  HorizontalArea = 459000
  IfcData = attributes={"GlobalId": {"name": "GlobalId", "type": "IfcGloballyUniqueId", "is_enum": false, "enum_values": []}, "Description": {"... (+475 chars omitted),+1 more (map truncated)
  IfcType = 7
  Length = 3060
  Material = -> Material
  MoveBase = false
  MoveWithHost = false
  Nodes = (2) [(-1.72563e-31,-1.42109e-15,-7.77156e-16),(3060,-1.42109e-15,-7.77156e-16)]
  NodesOffset = 0
  Normal = (0,0,0)
  PerimeterLength = 6420
  Placement = pos=(9010,9825,2800) rot=(0,0,-1;1.5708rad)
  PredefinedType = 0
  VerticalArea = 2.568e+06
  Width = 150
FEATURE [Part::FeaturePython] Structure135  label="V15x40 V127"  # Arch/BIM 7 (typed FeaturePython)
  FaceMaker = 0
  Height = 400
  HorizontalArea = 456000
  IfcData = attributes={"GlobalId": {"name": "GlobalId", "type": "IfcGloballyUniqueId", "is_enum": false, "enum_values": []}, "Description": {"... (+475 chars omitted),+1 more (map truncated)
  IfcType = 7
  Length = 3040
  Material = -> Material
  MoveBase = false
  MoveWithHost = false
  Nodes = (2) [(-1.72563e-31,-1.42109e-15,-7.77156e-16),(3040,-1.42109e-15,-7.77156e-16)]
  NodesOffset = 0
  Normal = (0,0,0)
  PerimeterLength = 6380
  Placement = pos=(9010,6515,2800) rot=(0,0,-1;1.5708rad)
  PredefinedType = 0
  VerticalArea = 2.552e+06
  Width = 150
FEATURE [Part::FeaturePython] Structure136  label="V15x40 V126"  # Arch/BIM 7 (typed FeaturePython)
  FaceMaker = 0
  Height = 400
  HorizontalArea = 457500
  IfcData = attributes={"GlobalId": {"name": "GlobalId", "type": "IfcGloballyUniqueId", "is_enum": false, "enum_values": []}, "Description": {"... (+475 chars omitted),+1 more (map truncated)
  IfcType = 7
  Length = 3050
  Material = -> Material
  MoveBase = false
  MoveWithHost = false
  Nodes = (2) [(-1.72563e-31,-1.42109e-15,-7.77156e-16),(3050,-1.42109e-15,-7.77156e-16)]
  NodesOffset = 0
  Normal = (0,0,0)
  PerimeterLength = 6400
  Placement = pos=(9010,3225,2800) rot=(0,0,-1;1.5708rad)
  PredefinedType = 0
  VerticalArea = 2.56e+06
  Width = 150
FEATURE [Part::FeaturePython] Structure137  label="V15x40 V132"  # Arch/BIM 7 (typed FeaturePython)
  FaceMaker = 0
  Height = 400
  HorizontalArea = 207000
  IfcData = attributes={"GlobalId": {"name": "GlobalId", "type": "IfcGloballyUniqueId", "is_enum": false, "enum_values": []}, "Description": {"... (+475 chars omitted),+1 more (map truncated)
  IfcType = 7
  Length = 1380
  Material = -> Material
  MoveBase = false
  MoveWithHost = false
  Nodes = (2) [(-1.72563e-31,-1.42109e-15,-7.77156e-16),(1380,-1.42109e-15,-7.77156e-16)]
  NodesOffset = 0
  Normal = (0,0,0)
  PerimeterLength = 3060
  Placement = pos=(12010,9825,2800) rot=(0,0,-1;1.5708rad)
  PredefinedType = 0
  VerticalArea = 1224000
  Width = 150
FEATURE [Part::FeaturePython] Structure138  label="V15x40 V131"  # Arch/BIM 7 (typed FeaturePython)
  FaceMaker = 0
  Height = 400
  HorizontalArea = 207000
  IfcData = attributes={"GlobalId": {"name": "GlobalId", "type": "IfcGloballyUniqueId", "is_enum": false, "enum_values": []}, "Description": {"... (+475 chars omitted),+1 more (map truncated)
  IfcType = 7
  Length = 1380
  Material = -> Material
  MoveBase = false
  MoveWithHost = false
  Nodes = (2) [(-1.72563e-31,-1.42109e-15,-7.77156e-16),(1380,-1.42109e-15,-7.77156e-16)]
  NodesOffset = 0
  Normal = (0,0,0)
  PerimeterLength = 3060
  Placement = pos=(10560,8445,2800) rot=(0,0,1;1.5708rad)
  PredefinedType = 0
  VerticalArea = 1224000
  Width = 150
FEATURE [Part::FeaturePython] Structure139  label="V15x40 V130"  # Arch/BIM 7 (typed FeaturePython)
  FaceMaker = 0
  Height = 400
  HorizontalArea = 363000
  IfcData = attributes={"GlobalId": {"name": "GlobalId", "type": "IfcGloballyUniqueId", "is_enum": false, "enum_values": []}, "Description": {"... (+475 chars omitted),+1 more (map truncated)
  IfcType = 7
  Length = 2420
  Material = -> Material
  MoveBase = false
  MoveWithHost = false
  Nodes = (2) [(-1.72563e-31,-1.42109e-15,-7.77156e-16),(2420,-1.42109e-15,-7.77156e-16)]
  NodesOffset = 0
  Normal = (0,0,0)
  PerimeterLength = 5140
  Placement = pos=(10560,3475,2800) rot=(0,0,1;1.5708rad)
  PredefinedType = 0
  VerticalArea = 2056000
  Width = 150
FEATURE [Part::FeaturePython] Structure140  label="V15x40 V129"  # Arch/BIM 7 (typed FeaturePython)
  FaceMaker = 0
  Height = 400
  HorizontalArea = 457500
  IfcData = attributes={"GlobalId": {"name": "GlobalId", "type": "IfcGloballyUniqueId", "is_enum": false, "enum_values": []}, "Description": {"... (+475 chars omitted),+1 more (map truncated)
  IfcType = 7
  Length = 3050
  Material = -> Material
  MoveBase = false
  MoveWithHost = false
  Nodes = (2) [(-1.72563e-31,-1.42109e-15,-7.77156e-16),(3050,-1.42109e-15,-7.77156e-16)]
  NodesOffset = 0
  Normal = (0,0,0)
  PerimeterLength = 6400
  Placement = pos=(10560,3225,2800) rot=(0,0,-1;1.5708rad)
  PredefinedType = 0
  VerticalArea = 2.56e+06
  Width = 150
FEATURE [Part::FeaturePython] Structure141  label="V15x40 V105"  # Arch/BIM 7 (typed FeaturePython)
  FaceMaker = 0
  Height = 400
  HorizontalArea = 453750
  IfcData = attributes={"GlobalId": {"name": "GlobalId", "type": "IfcGloballyUniqueId", "is_enum": false, "enum_values": []}, "Description": {"... (+475 chars omitted),+1 more (map truncated)
  IfcType = 7
  Length = 3025
  Material = -> Material
  MoveBase = false
  MoveWithHost = false
  Nodes = (2) [(-1.72563e-31,-1.42109e-15,-7.77156e-16),(3025,-1.42109e-15,-7.77156e-16)]
  NodesOffset = 0
  Normal = (0,0,0)
  PerimeterLength = 6350
  Placement = pos=(12085,8370,2800) rot=(0,0,1;0rad)
  PredefinedType = 0
  VerticalArea = 2.54e+06
  Width = 150
FEATURE [Part::FeaturePython] Structure197  label="L101"  # Arch/BIM 172 (typed FeaturePython)
  Base = -> Rectangle004
  FaceMaker = 0
  Height = 150
  HorizontalArea = 12611050
  IfcData = attributes={"GlobalId": {"name": "GlobalId", "type": "IfcGloballyUniqueId", "is_enum": false, "enum_values": []}, "Description": {"... (+484 chars omitted),+1 more (map truncated)
  IfcType = 172
  Length = 0
  Material = -> Material
  MoveBase = false
  MoveWithHost = false
  Nodes = (2) [(4057.5,8270,3000),(4057.5,8270,2850)]
  NodesOffset = 0
  Normal = (0,0,-1)
  PerimeterLength = 14330
  PredefinedType = 0
  VerticalArea = 2149500
  Width = 150
FEATURE [Part::FeaturePython] Structure198  label="L107"  # Arch/BIM 172 (typed FeaturePython)
  Base = -> Rectangle005
  FaceMaker = 0
  Height = 150
  HorizontalArea = 12732700
  IfcData = attributes={"GlobalId": {"name": "GlobalId", "type": "IfcGloballyUniqueId", "is_enum": false, "enum_values": []}, "Description": {"... (+484 chars omitted),+1 more (map truncated)
  IfcType = 172
  Length = 0
  Material = -> Material
  MoveBase = false
  MoveWithHost = false
  Nodes = (2) [(4057.5,4995,3000),(4057.5,4995,2850)]
  NodesOffset = 0
  Normal = (0,0,-1)
  PerimeterLength = 14390
  PredefinedType = 0
  VerticalArea = 2158500
  Width = 150
FEATURE [Part::FeaturePython] Structure199  label="L113"  # Arch/BIM 172 (typed FeaturePython)
  Base = -> Rectangle006
  FaceMaker = 0
  Height = 150
  HorizontalArea = 1.25705e+07
  IfcData = attributes={"GlobalId": {"name": "GlobalId", "type": "IfcGloballyUniqueId", "is_enum": false, "enum_values": []}, "Description": {"... (+484 chars omitted),+1 more (map truncated)
  IfcType = 172
  Length = 0
  Material = -> Material
  MoveBase = false
  MoveWithHost = false
  Nodes = (2) [(4057.5,1725,3000),(4057.5,1725,2850)]
  NodesOffset = 0
  Normal = (0,0,-1)
  PerimeterLength = 14310
  PredefinedType = 0
  VerticalArea = 2146500
  Width = 150
FEATURE [Part::FeaturePython] Structure200  label="V15x40 V102a"  # Arch/BIM 7 (typed FeaturePython)
  FaceMaker = 0
  Height = 400
  HorizontalArea = 405000
  IfcData = attributes={"GlobalId": {"name": "GlobalId", "type": "IfcGloballyUniqueId", "is_enum": false, "enum_values": []}, "Description": {"... (+475 chars omitted),+1 more (map truncated)
  IfcType = 7
  Length = 2700
  Material = -> Material
  MoveBase = false
  MoveWithHost = false
  Nodes = (2) [(-1.72563e-31,-1.42109e-15,-7.77156e-16),(2700,-1.42109e-15,-7.77156e-16)]
  NodesOffset = 0
  Normal = (0,0,0)
  PerimeterLength = 5700
  Placement = pos=(8935,8295,2800) rot=(0,0,1;3.14159rad)
  PredefinedType = 0
  VerticalArea = 2.28e+06
  Width = 150
FEATURE [Part::FeaturePython] Structure201  label="V15x40 V107a"  # Arch/BIM 7 (typed FeaturePython)
  FaceMaker = 0
  Height = 400
  HorizontalArea = 405000
  IfcData = attributes={"GlobalId": {"name": "GlobalId", "type": "IfcGloballyUniqueId", "is_enum": false, "enum_values": []}, "Description": {"... (+475 chars omitted),+1 more (map truncated)
  IfcType = 7
  Length = 2700
  Material = -> Material
  MoveBase = false
  MoveWithHost = false
  Nodes = (2) [(-1.72563e-31,-1.42109e-15,-7.77156e-16),(2700,-1.42109e-15,-7.77156e-16)]
  NodesOffset = 0
  Normal = (0,0,0)
  PerimeterLength = 5700
  Placement = pos=(8935,4995,2800) rot=(0,0,1;3.14159rad)
  PredefinedType = 0
  VerticalArea = 2.28e+06
  Width = 150
FEATURE [Part::FeaturePython] Structure202  label="V15x40 V112a"  # Arch/BIM 7 (typed FeaturePython)
  FaceMaker = 0
  Height = 400
  HorizontalArea = 405000
  IfcData = attributes={"GlobalId": {"name": "GlobalId", "type": "IfcGloballyUniqueId", "is_enum": false, "enum_values": []}, "Description": {"... (+475 chars omitted),+1 more (map truncated)
  IfcType = 7
  Length = 2700
  Material = -> Material
  MoveBase = false
  MoveWithHost = false
  Nodes = (2) [(-1.72563e-31,-1.42109e-15,-7.77156e-16),(2700,-1.42109e-15,-7.77156e-16)]
  NodesOffset = 0
  Normal = (0,0,0)
  PerimeterLength = 5700
  Placement = pos=(8935,1700,2800) rot=(0,0,1;3.14159rad)
  PredefinedType = 0
  VerticalArea = 2.28e+06
  Width = 150
FEATURE [Part::FeaturePython] Structure204  label="V15x40 V130a"  # Arch/BIM 7 (typed FeaturePython)
  FaceMaker = 0
  Height = 400
  HorizontalArea = 370500
  IfcData = attributes={"GlobalId": {"name": "GlobalId", "type": "IfcGloballyUniqueId", "is_enum": false, "enum_values": []}, "Description": {"... (+475 chars omitted),+1 more (map truncated)
  IfcType = 7
  Length = 2470
  Material = -> Material
  MoveBase = false
  MoveWithHost = false
  Nodes = (2) [(-1.72563e-31,-1.42109e-15,-7.77156e-16),(2470,-1.42109e-15,-7.77156e-16)]
  NodesOffset = 0
  Normal = (0,0,0)
  PerimeterLength = 5240
  Placement = pos=(12010,3425,2800) rot=(0,0,1;1.5708rad)
  PredefinedType = 0
  VerticalArea = 2096000
  Width = 150
FEATURE [App::GeometryPython] BuildingPart009  label="Vigas sobre PB"  # Arch/BIM 172 (typed FeaturePython)
  Area = 0
  Group = -> [Structure109,Structure115,Structure200,Structure119,Structure120,Structure141,Structure112,Structure116,Structure201,Structure121,Structure129,Structure130,Structure113,Structure117,Structure202,Structure122,Structure125,Structure114,Structure118,Structure123,Structure124,Structure133,Structure132,Structure131,Structure136,Structure135,Structure134,Structure140,Structure139,Structure204,+8 more]
  Height = 0
  HeightPropagate = true
  IfcData = attributes={"GlobalId": {"name": "GlobalId", "type": "IfcGloballyUniqueId", "is_enum": false, "enum_values": []}, "Description": {"... (+484 chars omitted),+1 more (map truncated)
  IfcType = 172
  LevelOffset = 0
  PredefinedType = 0
FEATURE [Part::FeaturePython] Structure205  label="L102"  # Arch/BIM 172 (typed FeaturePython)
  Base = -> Rectangle014
  FaceMaker = 0
  Height = 150
  HorizontalArea = 3928500
  IfcData = attributes={"GlobalId": {"name": "GlobalId", "type": "IfcGloballyUniqueId", "is_enum": false, "enum_values": []}, "Description": {"... (+484 chars omitted),+1 more (map truncated)
  IfcType = 172
  Length = 0
  Material = -> Material
  MoveBase = false
  MoveWithHost = false
  Nodes = (2) [(7585,9097.5,3000),(7585,9097.5,2850)]
  NodesOffset = 0
  Normal = (0,0,-1)
  PerimeterLength = 8310
  PredefinedType = 0
  VerticalArea = 1246500
  Width = 150
FEATURE [Part::FeaturePython] Structure206  label="L103"  # Arch/BIM 172 (typed FeaturePython)
  Base = -> Wire
  FaceMaker = 0
  Height = 150
  HorizontalArea = 3.9285e+06
  IfcData = attributes={"GlobalId": {"name": "GlobalId", "type": "IfcGloballyUniqueId", "is_enum": false, "enum_values": []}, "Description": {"... (+484 chars omitted),+1 more (map truncated)
  IfcType = 172
  Length = 0
  Material = -> Material
  MoveBase = false
  MoveWithHost = false
  Nodes = (2) [(7543.76,7449.37,3000),(7543.76,7449.37,2850)]
  NodesOffset = 0
  Normal = (0,0,-1)
  PerimeterLength = 8410
  Placement = pos=(0,0,-150) rot=(0,0,1;0rad)
  PredefinedType = 0
  VerticalArea = 1261500
  Width = 150
FEATURE [Part::FeaturePython] Structure207  label="L108"  # Arch/BIM 172 (typed FeaturePython)
  Base = -> Wire001
  FaceMaker = 0
  Height = 150
  HorizontalArea = 3.90134e+06
  IfcData = attributes={"GlobalId": {"name": "GlobalId", "type": "IfcGloballyUniqueId", "is_enum": false, "enum_values": []}, "Description": {"... (+484 chars omitted),+1 more (map truncated)
  IfcType = 172
  Length = 0
  Material = -> Material
  MoveBase = false
  MoveWithHost = false
  Nodes = (2) [(7543.46,5835.61,3000),(7543.46,5835.61,2850)]
  NodesOffset = 0
  Normal = (0,0,-1)
  PerimeterLength = 8389.89
  Placement = pos=(0,0,-150) rot=(0,0,1;0rad)
  PredefinedType = 0
  VerticalArea = 1.25848e+06
  Width = 150
FEATURE [Part::FeaturePython] Structure208  label="L109"  # Arch/BIM 172 (typed FeaturePython)
  Base = -> Rectangle015
  FaceMaker = 0
  Height = 150
  HorizontalArea = 4.0365e+06
  IfcData = attributes={"GlobalId": {"name": "GlobalId", "type": "IfcGloballyUniqueId", "is_enum": false, "enum_values": []}, "Description": {"... (+484 chars omitted),+1 more (map truncated)
  IfcType = 172
  Length = 0
  Material = -> Material
  MoveBase = false
  MoveWithHost = false
  Nodes = (2) [(7585,4172.5,3000),(7585,4172.5,2850)]
  NodesOffset = 0
  Normal = (0,0,-1)
  PerimeterLength = 8390
  PredefinedType = 0
  VerticalArea = 1258500
  Width = 150
FEATURE [Part::FeaturePython] Structure209  label="L114"  # Arch/BIM 172 (typed FeaturePython)
  Base = -> Wire002
  FaceMaker = 0
  Height = 150
  HorizontalArea = 3.91484e+06
  IfcData = attributes={"GlobalId": {"name": "GlobalId", "type": "IfcGloballyUniqueId", "is_enum": false, "enum_values": []}, "Description": {"... (+484 chars omitted),+1 more (map truncated)
  IfcType = 172
  Length = 0
  Material = -> Material
  MoveBase = false
  MoveWithHost = false
  Nodes = (2) [(7543.6,2543.13,3000),(7543.6,2543.13,2850)]
  NodesOffset = 0
  Normal = (0,0,-1)
  PerimeterLength = 8399.89
  Placement = pos=(0,0,-150) rot=(0,0,1;0rad)
  PredefinedType = 0
  VerticalArea = 1.25998e+06
  Width = 150
FEATURE [Part::FeaturePython] Structure210  label="L115"  # Arch/BIM 172 (typed FeaturePython)
  Base = -> Rectangle016
  FaceMaker = 0
  Height = 150
  HorizontalArea = 3.915e+06
  IfcData = attributes={"GlobalId": {"name": "GlobalId", "type": "IfcGloballyUniqueId", "is_enum": false, "enum_values": []}, "Description": {"... (+484 chars omitted),+1 more (map truncated)
  IfcType = 172
  Length = 0
  Material = -> Material
  MoveBase = false
  MoveWithHost = false
  Nodes = (2) [(7585,900,3000),(7585,900,2850)]
  NodesOffset = 0
  Normal = (0,0,-1)
  PerimeterLength = 8300
  PredefinedType = 0
  VerticalArea = 1.245e+06
  Width = 150
FEATURE [Part::FeaturePython] Structure211  label="L104"  # Arch/BIM 172 (typed FeaturePython)
  Base = -> Rectangle008
  FaceMaker = 0
  Height = 150
  HorizontalArea = 4354000
  IfcData = attributes={"GlobalId": {"name": "GlobalId", "type": "IfcGloballyUniqueId", "is_enum": false, "enum_values": []}, "Description": {"... (+484 chars omitted),+1 more (map truncated)
  IfcType = 172
  Length = 0
  Material = -> Material
  MoveBase = false
  MoveWithHost = false
  Nodes = (2) [(9785,8270,3000),(9785,8270,2850)]
  NodesOffset = 0
  Normal = (0,0,-1)
  PerimeterLength = 9020
  PredefinedType = 0
  VerticalArea = 1353000
  Width = 150
FEATURE [Part::FeaturePython] Structure212  label="L110"  # Arch/BIM 172 (typed FeaturePython)
  Base = -> Rectangle011
  FaceMaker = 0
  Height = 150
  HorizontalArea = 4396000
  IfcData = attributes={"GlobalId": {"name": "GlobalId", "type": "IfcGloballyUniqueId", "is_enum": false, "enum_values": []}, "Description": {"... (+484 chars omitted),+1 more (map truncated)
  IfcType = 172
  Length = 0
  Material = -> Material
  MoveBase = false
  MoveWithHost = false
  Nodes = (2) [(9785,4995,3000),(9785,4995,2850)]
  NodesOffset = 0
  Normal = (0,0,-1)
  PerimeterLength = 9080
  PredefinedType = 0
  VerticalArea = 1362000
  Width = 150
FEATURE [Part::FeaturePython] Structure213  label="L116"  # Arch/BIM 172 (typed FeaturePython)
  Base = -> Rectangle013
  FaceMaker = 0
  Height = 150
  HorizontalArea = 4.34e+06
  IfcData = attributes={"GlobalId": {"name": "GlobalId", "type": "IfcGloballyUniqueId", "is_enum": false, "enum_values": []}, "Description": {"... (+484 chars omitted),+1 more (map truncated)
  IfcType = 172
  Length = 0
  Material = -> Material
  MoveBase = false
  MoveWithHost = false
  Nodes = (2) [(9785,1725,3000),(9785,1725,2850)]
  NodesOffset = 0
  Normal = (0,0,-1)
  PerimeterLength = 9000
  PredefinedType = 0
  VerticalArea = 1350000
  Width = 150
FEATURE [Part::FeaturePython] Structure214  label="L105"  # Arch/BIM 172 (typed FeaturePython)
  Base = -> Rectangle009
  FaceMaker = 0
  Height = 150
  HorizontalArea = 1.794e+06
  IfcData = attributes={"GlobalId": {"name": "GlobalId", "type": "IfcGloballyUniqueId", "is_enum": false, "enum_values": []}, "Description": {"... (+484 chars omitted),+1 more (map truncated)
  IfcType = 172
  Length = 0
  Material = -> Material
  MoveBase = false
  MoveWithHost = false
  Nodes = (2) [(11285,9135,3000),(11285,9135,2850)]
  NodesOffset = 0
  Normal = (0,0,-1)
  PerimeterLength = 5360
  PredefinedType = 0
  VerticalArea = 804000
  Width = 150
FEATURE [Part::FeaturePython] Structure215  label="L111"  # Arch/BIM 172 (typed FeaturePython)
  Base = -> Rectangle018
  FaceMaker = 0
  Height = 150
  HorizontalArea = 3.211e+06
  IfcData = attributes={"GlobalId": {"name": "GlobalId", "type": "IfcGloballyUniqueId", "is_enum": false, "enum_values": []}, "Description": {"... (+484 chars omitted),+1 more (map truncated)
  IfcType = 172
  Length = 0
  Material = -> Material
  MoveBase = false
  MoveWithHost = false
  Nodes = (2) [(11285,4660,3000),(11285,4660,2850)]
  NodesOffset = 0
  Normal = (0,0,-1)
  PerimeterLength = 7540
  PredefinedType = 0
  VerticalArea = 1.131e+06
  Width = 150
FEATURE [Part::FeaturePython] Structure216  label="L117"  # Arch/BIM 172 (typed FeaturePython)
  Base = -> Rectangle020
  FaceMaker = 0
  Height = 150
  HorizontalArea = 9439500
  IfcData = attributes={"GlobalId": {"name": "GlobalId", "type": "IfcGloballyUniqueId", "is_enum": false, "enum_values": []}, "Description": {"... (+484 chars omitted),+1 more (map truncated)
  IfcType = 172
  Length = 0
  Material = -> Material
  MoveBase = false
  MoveWithHost = false
  Nodes = (2) [(12157.5,1725,3000),(12157.5,1725,2850)]
  NodesOffset = 0
  Normal = (0,0,-1)
  PerimeterLength = 12290
  PredefinedType = 0
  VerticalArea = 1843500
  Width = 150
FEATURE [Part::FeaturePython] Structure217  label="L112"  # Arch/BIM 172 (typed FeaturePython)
  Base = -> Rectangle019
  FaceMaker = 0
  Height = 150
  HorizontalArea = 3.93965e+06
  IfcData = attributes={"GlobalId": {"name": "GlobalId", "type": "IfcGloballyUniqueId", "is_enum": false, "enum_values": []}, "Description": {"... (+484 chars omitted),+1 more (map truncated)
  IfcType = 172
  Length = 0
  Material = -> Material
  MoveBase = false
  MoveWithHost = false
  Nodes = (2) [(12882.5,4660,3000),(12882.5,4660,2850)]
  NodesOffset = 0
  Normal = (0,0,-1)
  PerimeterLength = 8130
  Placement = pos=(0,0,-150) rot=(0,0,1;0rad)
  PredefinedType = 0
  VerticalArea = 1.2195e+06
  Width = 150
FEATURE [Part::FeaturePython] Structure218  label="L106"  # Arch/BIM 172 (typed FeaturePython)
  Base = -> Rectangle017
  FaceMaker = 0
  Height = 150
  HorizontalArea = 4174500
  IfcData = attributes={"GlobalId": {"name": "GlobalId", "type": "IfcGloballyUniqueId", "is_enum": false, "enum_values": []}, "Description": {"... (+484 chars omitted),+1 more (map truncated)
  IfcType = 172
  Length = 0
  Material = -> Material
  MoveBase = false
  MoveWithHost = false
  Nodes = (2) [(13597.5,9135,3000),(13597.5,9135,2850)]
  NodesOffset = 0
  Normal = (0,0,-1)
  PerimeterLength = 8810
  PredefinedType = 0
  VerticalArea = 1321500
  Width = 150
FEATURE [App::GeometryPython] BuildingPart014  label="Losas sobre PB"  # Arch/BIM 172 (typed FeaturePython)
  Area = 0
  Group = -> [Structure197,Structure205,Structure206,Structure211,Structure214,Structure218,Structure198,Structure207,Structure208,Structure212,Structure215,Structure217,Structure199,Structure209,Structure210,Structure213,Structure216]
  Height = 0
  HeightPropagate = true
  IfcData = attributes={"GlobalId": {"name": "GlobalId", "type": "IfcGloballyUniqueId", "is_enum": false, "enum_values": []}, "Description": {"... (+484 chars omitted),+1 more (map truncated)
  IfcType = 172
  LevelOffset = 0
  PredefinedType = 0
FEATURE [App::GeometryPython] BuildingPart001  label="Nivel 0"  # Arch/BIM 172 (typed FeaturePython)
  Area = 24900000
  Group = -> [BuildingPart004,BuildingPart014,Wall001,BuildingPart009]
  Height = 0
  HeightPropagate = true
  IfcData = attributes={"GlobalId": {"name": "GlobalId", "type": "IfcGloballyUniqueId", "is_enum": false, "enum_values": []}, "Description": {"... (+484 chars omitted),+1 more (map truncated)
  IfcType = 172
  LevelOffset = 0
  PredefinedType = 0
FEATURE [App::DocumentObjectGroupPython] MaterialContainer  label="Materials"  # scripted group (container) (typed FeaturePython)
  Group = -> [Material]
FEATURE [Part::FeaturePython] Structure401  label="Beam046"  # Arch/BIM 7 (typed FeaturePython)
  FaceMaker = 0
  Height = 300
  HorizontalArea = 337500
  IfcData = attributes={"GlobalId": {"name": "GlobalId", "type": "IfcGloballyUniqueId", "is_enum": false, "enum_values": []}, "Description": {"... (+475 chars omitted),+1 more (map truncated)
  IfcType = 7
  Length = 1125
  Material = -> Material
  MoveBase = false
  MoveWithHost = false
  Nodes = (2) [(1.2326e-31,-1.51582e-15,5.55112e-16),(1125,-1.51582e-15,5.55112e-16)]
  NodesOffset = 0
  Normal = (0,0,0)
  PerimeterLength = 2850
  Placement = pos=(9360,6640,-650) rot=(0,0,1;0rad)
  PredefinedType = 0
  VerticalArea = 855000
  Width = 300
FEATURE [App::GeometryPython] BuildingPart005  label="Vigas riostras"  # Arch/BIM 172 (typed FeaturePython)
  Area = 0
  Group = -> [Beam,Beam001,Structure041,Structure042,Structure043,Structure044,Structure045,Structure046,Structure048,Structure049,Structure053,Structure056,Structure059,Structure060,Structure061,Structure064,Structure065,Structure066,Structure067,Structure068,Structure069,Structure070,Structure071,Structure072,Structure073,Structure074,Structure075,Structure076,Structure077,Structure078,Structure079,+2 more]
  Height = 0
  HeightPropagate = true
  IfcData = attributes={"GlobalId": {"name": "GlobalId", "type": "IfcGloballyUniqueId", "is_enum": false, "enum_values": []}, "Description": {"... (+484 chars omitted),+1 more (map truncated)
  IfcType = 172
  LevelOffset = 0
  Placement = pos=(0,0,500) rot=(0,0,1;0rad)
  PredefinedType = 0
FEATURE [App::GeometryPython] BuildingPart002  label="Fundaciones"  # Arch/BIM 172 (typed FeaturePython)
  Area = 8300000
  Group = -> [BuildingPart005,BuildingPart006,BuildingPart007,BuildingPart008,Wall]
  Height = 0
  HeightPropagate = true
  IfcData = attributes={"GlobalId": {"name": "GlobalId", "type": "IfcGloballyUniqueId", "is_enum": false, "enum_values": []}, "Description": {"... (+484 chars omitted),+1 more (map truncated)
  IfcType = 172
  LevelOffset = 0
  PredefinedType = 0
FEATURE [App::GeometryPython] BuildingPart  label="Building"  # Arch/BIM 10 (typed FeaturePython)
  Area = 107900000
  BuildingType = 0
  CompositionType = 0
  ElevationOfRefHeight = 0
  ElevationOfTerrain = 0
  Group = -> [BuildingPart002,BuildingPart001,BuildingPart003,BuildingPart010,BuildingPart019,BuildingPart023,BuildingPart024]
  Height = 0
  HeightPropagate = true
  IfcData = attributes={"GlobalId": {"name": "GlobalId", "type": "IfcGloballyUniqueId", "is_enum": false, "enum_values": []}, "Description": {"... (+1010 chars omitted),+1 more (map truncated)
  IfcType = 10
  LevelOffset = 0
  LongName = Building
FEATURE [TechDraw::DrawSVGTemplate] Template008
  EditableTexts = Cliente 1=UNIVERSO BIM,Comprobado por=GORO,Dibujado por=GORO,Escala=-,Fecha=2021/01,Nombre plano 1=PORTADA,Numero Proyecto=21005,Numero plano=ES-001,+2 more (map truncated)
  Height = 297
  Orientation = 1
  Width = 420
FEATURE [TechDraw::DrawViewPart] View  label="VIEW-Vista Portada"
  Caption = VISTA DEL PROYECTO
  CoarseView = false
  Direction = (0.473,-0.767,0.435)
  Focus = 200
  HardHidden = false
  IsoCount = 0
  IsoHidden = false
  IsoVisible = false
  LockPosition = true
  Perspective = true
  Rotation = 0
  Scale = 0.007
  ScaleType = 0
  SeamHidden = false
  SeamVisible = true
  SmoothHidden = false
  SmoothVisible = true
  Source = -> [BuildingPart]
  X = 317.281
  XDirection = (0.844,0.536,0.027)
  Y = 166.952
FEATURE [TechDraw::DrawViewAnnotation] Annotation
  Font = Arial
  LineSpace = 80
  LockPosition = false
  MaxWidth = -1
  Rotation = 0
  ScaleType = 0
  Text = LISTA DE PLANOS
  TextSize = 5
  TextStyle = 0
  X = 60.7425
  Y = 271.395
FEATURE [TechDraw::DrawPage] Page008  label="ES-001-PORTADA"
  KeepUpdated = true
  NextBalloonIndex = 1
  ProjectionType = 0
  Template = -> Template008
  Views = -> [View,Annotation]
FEATURE [TechDraw::DrawSVGTemplate] Template
  EditableTexts = Cliente 1=UNIVERSO BIM,Comprobado por=GORO,Dibujado por=GORO,Escala=1:50,Fecha=2021/01,Nombre plano 1=ESTRUCTURA CIMIENTOS,Numero Proyecto=21005,+3 more (map truncated)
  Height = 297
  Orientation = 1
  Width = 420
FEATURE [TechDraw::DrawViewPart] View002  label="FRONTAL GRAL"
  CoarseView = false
  Direction = (0,-1,0)
  Focus = 100
  HardHidden = false
  IsoCount = 0
  IsoHidden = false
  IsoVisible = false
  LockPosition = false
  Perspective = false
  Rotation = 0
  Scale = 0.02
  ScaleType = 0
  SeamHidden = false
  SeamVisible = true
  SmoothHidden = false
  SmoothVisible = true
  Source = -> [BuildingPart]
  X = -192.574
  XDirection = (1,0,0)
  Y = 131.87
FEATURE [TechDraw::DrawSVGTemplate] Template010
  EditableTexts = Cliente 1=LINEA 1,Cliente 2=LINEA 2,Comprobado por=Comp por,Dibujado por=Dibujado por,Escala=Escala,Fecha=Fecha,Nombre plano 1=LINEA 1,+6 more (map truncated)
  Height = 297
  Orientation = 1
  Width = 420
FEATURE [TechDraw::DrawViewPart] View003
  CoarseView = false
  Direction = (0,-1,0)
  Focus = 100
  HardHidden = false
  IsoCount = 0
  IsoHidden = false
  IsoVisible = false
  LockPosition = false
  Perspective = false
  Rotation = 0
  Scale = 0.02
  ScaleType = 0
  SeamHidden = false
  SeamVisible = true
  SmoothHidden = false
  SmoothVisible = true
  Source = -> [BuildingPart]
  X = -198.186
  XDirection = (1,0,0)
  Y = 135.252
FEATURE [TechDraw::DrawViewSection] SectionView  label="FUND PLANTA"
  BaseView = -> View002
  Caption = PLANTA FUNDACIONES
  CoarseView = false
  CutSurfaceDisplay = 1
  Direction = (0,0,1)
  FileGeomPattern = <path>
  FileHatchPattern = <path>
  Focus = 100
  FuseBeforeCut = false
  HardHidden = false
  HatchScale = 1
  IsoCount = 0
  IsoHidden = false
  IsoVisible = false
  LockPosition = true
  NameGeomPattern = Diamond
  Perspective = false
  Rotation = 0
  Scale = 0.02
  ScaleType = 0
  SeamHidden = false
  SeamVisible = true
  SectionDirection = 3
  SectionNormal = (0,0,1)
  SectionOrigin = (8570,5000,-300)
  SmoothHidden = false
  SmoothVisible = true
  Source = -> [BuildingPart]
  X = 222.873
  XDirection = (1,0,0)
  Y = 166.982
FEATURE [TechDraw::DrawViewDimension] Dimension008
  Arbitrary = false
  ArbitraryTolerances = false
  EqualTolerance = false
  FormatSpec = %.2f
  FormatSpecOverTolerance = %+.2f
  FormatSpecUnderTolerance = %+.2f
  Inverted = false
  LockPosition = false
  MeasureType = 1
  OverTolerance = 0
  References2D = -> [SectionView]
  Rotation = 0
  ScaleType = 0
  TheoreticalExact = false
  Type = 1
  UnderTolerance = 0
  X = 68.8
  Y = 112
FEATURE [TechDraw::DrawViewDimension] Dimension005
  Arbitrary = false
  ArbitraryTolerances = false
  EqualTolerance = false
  FormatSpec = %.2f
  FormatSpecOverTolerance = %+.2f
  FormatSpecUnderTolerance = %+.2f
  Inverted = false
  LockPosition = false
  MeasureType = 1
  OverTolerance = 0
  References2D = -> [SectionView]
  Rotation = 0
  ScaleType = 0
  TheoreticalExact = false
  Type = 1
  UnderTolerance = 0
  X = -19.7
  Y = 112
FEATURE [TechDraw::DrawViewDimension] Dimension007
  Arbitrary = false
  ArbitraryTolerances = false
  EqualTolerance = false
  FormatSpec = %.2f
  FormatSpecOverTolerance = %+.2f
  FormatSpecUnderTolerance = %+.2f
  Inverted = false
  LockPosition = false
  MeasureType = 1
  OverTolerance = 0
  References2D = -> [SectionView]
  Rotation = 0
  ScaleType = 0
  TheoreticalExact = false
  Type = 1
  UnderTolerance = 0
  X = 38.8
  Y = 112
FEATURE [TechDraw::DrawViewDimension] Dimension004
  Arbitrary = false
  ArbitraryTolerances = false
  EqualTolerance = false
  FormatSpec = %.2f
  FormatSpecOverTolerance = %+.2f
  FormatSpecUnderTolerance = %+.2f
  Inverted = false
  LockPosition = false
  MeasureType = 1
  OverTolerance = 0
  References2D = -> [SectionView]
  Rotation = 0
  ScaleType = 0
  TheoreticalExact = false
  Type = 1
  UnderTolerance = 0
  X = -48.2
  Y = 112
FEATURE [TechDraw::DrawViewDimension] Dimension003
  Arbitrary = false
  ArbitraryTolerances = false
  EqualTolerance = false
  FormatSpec = %.2f
  FormatSpecOverTolerance = %+.2f
  FormatSpecUnderTolerance = %+.2f
  Inverted = false
  LockPosition = false
  MeasureType = 1
  OverTolerance = 0
  References2D = -> [SectionView]
  Rotation = 0
  ScaleType = 0
  TheoreticalExact = false
  Type = 1
  UnderTolerance = 0
  X = -90.4298
  Y = 112
FEATURE [TechDraw::DrawViewDimension] Dimension006
  Arbitrary = false
  ArbitraryTolerances = false
  EqualTolerance = false
  FormatSpec = %.2f
  FormatSpecOverTolerance = %+.2f
  FormatSpecUnderTolerance = %+.2f
  Inverted = false
  LockPosition = false
  MeasureType = 1
  OverTolerance = 0
  References2D = -> [SectionView]
  Rotation = 0
  ScaleType = 0
  TheoreticalExact = false
  Type = 1
  UnderTolerance = 0
  X = 8.88381
  Y = 112
FEATURE [TechDraw::DrawViewDimension] Dimension010
  Arbitrary = false
  ArbitraryTolerances = false
  EqualTolerance = false
  FormatSpec = %.2f
  FormatSpecOverTolerance = %+.2f
  FormatSpecUnderTolerance = %+.2f
  Inverted = false
  LockPosition = false
  MeasureType = 1
  OverTolerance = 0
  References2D = -> [SectionView]
  Rotation = 0
  ScaleType = 0
  TheoreticalExact = false
  Type = 1
  UnderTolerance = 0
  X = 132.8
  Y = 112
FEATURE [TechDraw::DrawViewDimension] Dimension009
  Arbitrary = false
  ArbitraryTolerances = false
  EqualTolerance = false
  FormatSpec = %.2f
  FormatSpecOverTolerance = %+.2f
  FormatSpecUnderTolerance = %+.2f
  Inverted = false
  LockPosition = false
  MeasureType = 1
  OverTolerance = 0
  References2D = -> [SectionView]
  Rotation = 0
  ScaleType = 0
  TheoreticalExact = false
  Type = 1
  UnderTolerance = 0
  X = 100.8
  Y = 112
FEATURE [TechDraw::DrawViewDimension] Dimension012
  Arbitrary = false
  ArbitraryTolerances = false
  EqualTolerance = false
  FormatSpec = %.2f
  FormatSpecOverTolerance = %+.2f
  FormatSpecUnderTolerance = %+.2f
  Inverted = false
  LockPosition = false
  MeasureType = 1
  OverTolerance = 0
  References2D = -> [SectionView]
  Rotation = 0
  ScaleType = 0
  TheoreticalExact = false
  Type = 2
  UnderTolerance = 0
  X = -150
  Y = 98.3065
FEATURE [TechDraw::DrawViewDimension] Dimension013
  Arbitrary = false
  ArbitraryTolerances = false
  EqualTolerance = false
  FormatSpec = %.2f
  FormatSpecOverTolerance = %+.2f
  FormatSpecUnderTolerance = %+.2f
  Inverted = false
  LockPosition = false
  MeasureType = 1
  OverTolerance = 0
  References2D = -> [SectionView]
  Rotation = 0
  ScaleType = 0
  TheoreticalExact = false
  Type = 2
  UnderTolerance = 0
  X = -150
  Y = 66.7297
FEATURE [TechDraw::DrawViewDimension] Dimension014
  Arbitrary = false
  ArbitraryTolerances = false
  EqualTolerance = false
  FormatSpec = %.2f
  FormatSpecOverTolerance = %+.2f
  FormatSpecUnderTolerance = %+.2f
  Inverted = false
  LockPosition = false
  MeasureType = 1
  OverTolerance = 0
  References2D = -> [SectionView]
  Rotation = 0
  ScaleType = 0
  TheoreticalExact = false
  Type = 2
  UnderTolerance = 0
  X = -150
  Y = 32.8
FEATURE [TechDraw::DrawViewDimension] Dimension015
  Arbitrary = false
  ArbitraryTolerances = false
  EqualTolerance = false
  FormatSpec = %.2f
  FormatSpecOverTolerance = %+.2f
  FormatSpecUnderTolerance = %+.2f
  Inverted = false
  LockPosition = false
  MeasureType = 1
  OverTolerance = 0
  References2D = -> [SectionView]
  Rotation = 0
  ScaleType = 0
  TheoreticalExact = false
  Type = 2
  UnderTolerance = 0
  X = -150
  Y = -0.1
FEATURE [TechDraw::DrawViewDimension] Dimension016
  Arbitrary = false
  ArbitraryTolerances = false
  EqualTolerance = false
  FormatSpec = %.2f
  FormatSpecOverTolerance = %+.2f
  FormatSpecUnderTolerance = %+.2f
  Inverted = false
  LockPosition = false
  MeasureType = 1
  OverTolerance = 0
  References2D = -> [SectionView]
  Rotation = 0
  ScaleType = 0
  TheoreticalExact = false
  Type = 2
  UnderTolerance = 0
  X = -150
  Y = -33
FEATURE [TechDraw::DrawViewDimension] Dimension017
  Arbitrary = false
  ArbitraryTolerances = false
  EqualTolerance = false
  FormatSpec = %.2f
  FormatSpecOverTolerance = %+.2f
  FormatSpecUnderTolerance = %+.2f
  Inverted = false
  LockPosition = false
  MeasureType = 1
  OverTolerance = 0
  References2D = -> [SectionView]
  Rotation = 0
  ScaleType = 0
  TheoreticalExact = false
  Type = 2
  UnderTolerance = 0
  X = -150
  Y = -65.5
FEATURE [TechDraw::DrawViewDimension] Dimension018
  Arbitrary = false
  ArbitraryTolerances = false
  EqualTolerance = false
  FormatSpec = %.2f
  FormatSpecOverTolerance = %+.2f
  FormatSpecUnderTolerance = %+.2f
  Inverted = false
  LockPosition = false
  MeasureType = 1
  OverTolerance = 0
  References2D = -> [SectionView]
  Rotation = 0
  ScaleType = 0
  TheoreticalExact = false
  Type = 2
  UnderTolerance = 0
  X = -150
  Y = -97.4094
FEATURE [Part::Part2DObjectPython] Line  # Draft 2D object (typed FeaturePython)
  Area = 0
  ChamferSize = 0
  Closed = false
  End = (8635,7770,3000)
  FilletRadius = 0
  Length = 450
  MakeFace = true
  Placement = pos=(8635,8220,3000) rot=(0,0,1;0rad)
  Points = (2) [(0,0,0),(0,-450,0)]
  Start = (8635,8220,3000)
  Subdivisions = 0
FEATURE [Part::Part2DObjectPython] Line001  # Draft 2D object (typed FeaturePython)
  Area = 0
  ChamferSize = 0
  Closed = false
  End = (8935,7770,3000)
  FilletRadius = 0
  Length = 300
  MakeFace = true
  Placement = pos=(8635,7770,3000) rot=(0,0,1;0rad)
  Points = (2) [(0,0,0),(300,0,0)]
  Start = (8635,7770,3000)
  Subdivisions = 0
FEATURE [Part::Part2DObjectPython] Line002  # Draft 2D object (typed FeaturePython)
  Area = 0
  ChamferSize = 0
  Closed = false
  End = (8635,5070.11,3000)
  FilletRadius = 0
  Length = 450
  MakeFace = true
  Placement = pos=(8635,5520.11,3000) rot=(0,0,1;0rad)
  Points = (2) [(0,0,0),(0,-450,0)]
  Start = (8635,5520.11,3000)
  Subdivisions = 0
FEATURE [Part::Part2DObjectPython] Line003  # Draft 2D object (typed FeaturePython)
  Area = 0
  ChamferSize = 0
  Closed = false
  End = (8935,5520.11,3000)
  FilletRadius = 0
  Length = 300
  MakeFace = true
  Placement = pos=(8635,5520.11,3000) rot=(0,0,1;0rad)
  Points = (2) [(0,0,0),(300,0,0)]
  Start = (8635,5520.11,3000)
  Subdivisions = 0
FEATURE [Part::Part2DObjectPython] Line004  # Draft 2D object (typed FeaturePython)
  Area = 0
  ChamferSize = 0
  Closed = false
  End = (8935,2225.11,3000)
  FilletRadius = 0
  Length = 300
  MakeFace = true
  Placement = pos=(8635,2225.11,3000) rot=(0,0,1;0rad)
  Points = (2) [(0,0,0),(300,0,0)]
  Start = (8635,2225.11,3000)
  Subdivisions = 0
FEATURE [Part::Part2DObjectPython] Line005  # Draft 2D object (typed FeaturePython)
  Area = 0
  ChamferSize = 0
  Closed = false
  End = (8635,1775.11,3000)
  FilletRadius = 0
  Length = 450
  MakeFace = true
  Placement = pos=(8635,2225.11,3000) rot=(0,0,1;0rad)
  Points = (2) [(0,0,0),(0,-450,0)]
  Start = (8635,2225.11,3000)
  Subdivisions = 0
FEATURE [Part::Part2DObjectPython] Line006  # Draft 2D object (typed FeaturePython)
  Area = 0
  ChamferSize = 0
  Closed = false
  End = (8935,8220,3000)
  FilletRadius = 0
  Length = 540.833
  MakeFace = true
  Placement = pos=(8635,7770,3000) rot=(0,0,1;0rad)
  Points = (2) [(0,0,0),(300,450,0)]
  Start = (8635,7770,3000)
  Subdivisions = 0
FEATURE [Part::Part2DObjectPython] Line007  # Draft 2D object (typed FeaturePython)
  Area = 0
  ChamferSize = 0
  Closed = false
  End = (8935,7770,3000)
  FilletRadius = 0
  Length = 540.833
  MakeFace = true
  Placement = pos=(8635,8220,3000) rot=(0,0,1;0rad)
  Points = (2) [(0,0,0),(300,-450,0)]
  Start = (8635,8220,3000)
  Subdivisions = 0
FEATURE [Part::Part2DObjectPython] Line008  # Draft 2D object (typed FeaturePython)
  Area = 0
  ChamferSize = 0
  Closed = false
  End = (8935,5070,3000)
  FilletRadius = 0
  Length = 540.921
  MakeFace = true
  Placement = pos=(8635,5520.11,3000) rot=(0,0,1;0rad)
  Points = (2) [(0,0,0),(300,-450.106,0)]
  Start = (8635,5520.11,3000)
  Subdivisions = 0
FEATURE [Part::Part2DObjectPython] Line009  # Draft 2D object (typed FeaturePython)
  Area = 0
  ChamferSize = 0
  Closed = false
  End = (8935,5520.11,3000)
  FilletRadius = 0
  Length = 540.833
  MakeFace = true
  Placement = pos=(8635,5070.11,3000) rot=(0,0,1;0rad)
  Points = (2) [(0,0,0),(300,450,0)]
  Start = (8635,5070.11,3000)
  Subdivisions = 0
FEATURE [Part::Part2DObjectPython] Line010  # Draft 2D object (typed FeaturePython)
  Area = 0
  ChamferSize = 0
  Closed = false
  End = (8935,2225.11,3000)
  FilletRadius = 0
  Length = 540.833
  MakeFace = true
  Placement = pos=(8635,1775.11,3000) rot=(0,0,1;0rad)
  Points = (2) [(0,0,0),(300,450,0)]
  Start = (8635,1775.11,3000)
  Subdivisions = 0
FEATURE [Part::Part2DObjectPython] Line011  # Draft 2D object (typed FeaturePython)
  Area = 0
  ChamferSize = 0
  Closed = false
  End = (8935,1775,3000)
  FilletRadius = 0
  Length = 540.921
  MakeFace = true
  Placement = pos=(8635,2225.11,3000) rot=(0,0,1;0rad)
  Points = (2) [(0,0,0),(300,-450.106,0)]
  Start = (8635,2225.11,3000)
  Subdivisions = 0
FEATURE [App::DocumentObjectGroup] Group004  label="2D-Nivel 0"
  Group = -> [Line,Line001,Line002,Line003,Line004,Line005,Line006,Line007,Line008,Line009,Line010,Line011]
FEATURE [App::DocumentObjectGroup] Group003  label="Anotaciones"
  Group = -> [Group004,Group,Rectangle001]
FEATURE [TechDraw::DrawViewDimension] Dimension
  Arbitrary = false
  ArbitraryTolerances = false
  EqualTolerance = false
  FormatSpec = %.2f
  FormatSpecOverTolerance = %+.2f
  FormatSpecUnderTolerance = %+.2f
  Inverted = false
  LockPosition = false
  MeasureType = 1
  OverTolerance = 0
  References2D = -> [SectionView]
  Rotation = 0
  ScaleType = 0
  TheoreticalExact = false
  Type = 1
  UnderTolerance = 0
  X = -132.8
  Y = 112
FEATURE [TechDraw::DrawPage] Page  label="ES-002-ESTRUCTURA CIMIENTOS"
  KeepUpdated = true
  NextBalloonIndex = 1
  ProjectionType = 0
  Template = -> Template
  Views = -> [View002,SectionView,Dimension003,Dimension004,Dimension005,Dimension006,Dimension007,Dimension008,Dimension009,Dimension010,Dimension012,Dimension013,Dimension014,Dimension015,Dimension016,Dimension017,Dimension018,Dimension]
FEATURE [TechDraw::DrawViewSection] SectionView001  label="Section  - "
  BaseView = -> View003
  CoarseView = false
  CutSurfaceDisplay = 1
  Direction = (0,0,-1)
  FileGeomPattern = <path>
  FileHatchPattern = <path>
  Focus = 100
  FuseBeforeCut = false
  HardHidden = false
  HatchScale = 1
  IsoCount = 0
  IsoHidden = false
  IsoVisible = false
  LockPosition = false
  NameGeomPattern = Diamond
  Perspective = false
  Rotation = 0
  Scale = 0.02
  ScaleType = 0
  SeamHidden = false
  SeamVisible = true
  SectionDirection = 2
  SectionNormal = (0,0,-1)
  SectionOrigin = (8570,5000,1800)
  SmoothHidden = false
  SmoothVisible = true
  Source = -> [BuildingPart001]
  X = 213.491
  XDirection = (1,0,0)
  Y = 170.552
FEATURE [TechDraw::DrawPage] Page010  label="03b-EST s/PB"
  KeepUpdated = true
  NextBalloonIndex = 1
  ProjectionType = 0
  Template = -> Template010
  Views = -> [View003,SectionView001]
FEATURE [App::GeometryPython] BuildingPart029  label="PLANOS"  # Arch/BIM 172 (typed FeaturePython)
  Area = 0
  Group = -> [Page008,Page,Page010]
  Height = 0
  HeightPropagate = true
  IfcData = attributes={"GlobalId": {"name": "GlobalId", "type": "IfcGloballyUniqueId", "is_enum": false, "enum_values": []}, "Description": {"... (+484 chars omitted),+1 more (map truncated)
  IfcType = 172
  LevelOffset = 0
  Placement = pos=(0,0,-300) rot=(0,0,1;0rad)
  PredefinedType = 0
note: 4 file-system paths scrubbed to <path> (originals preserved in the JSON sidecar)
